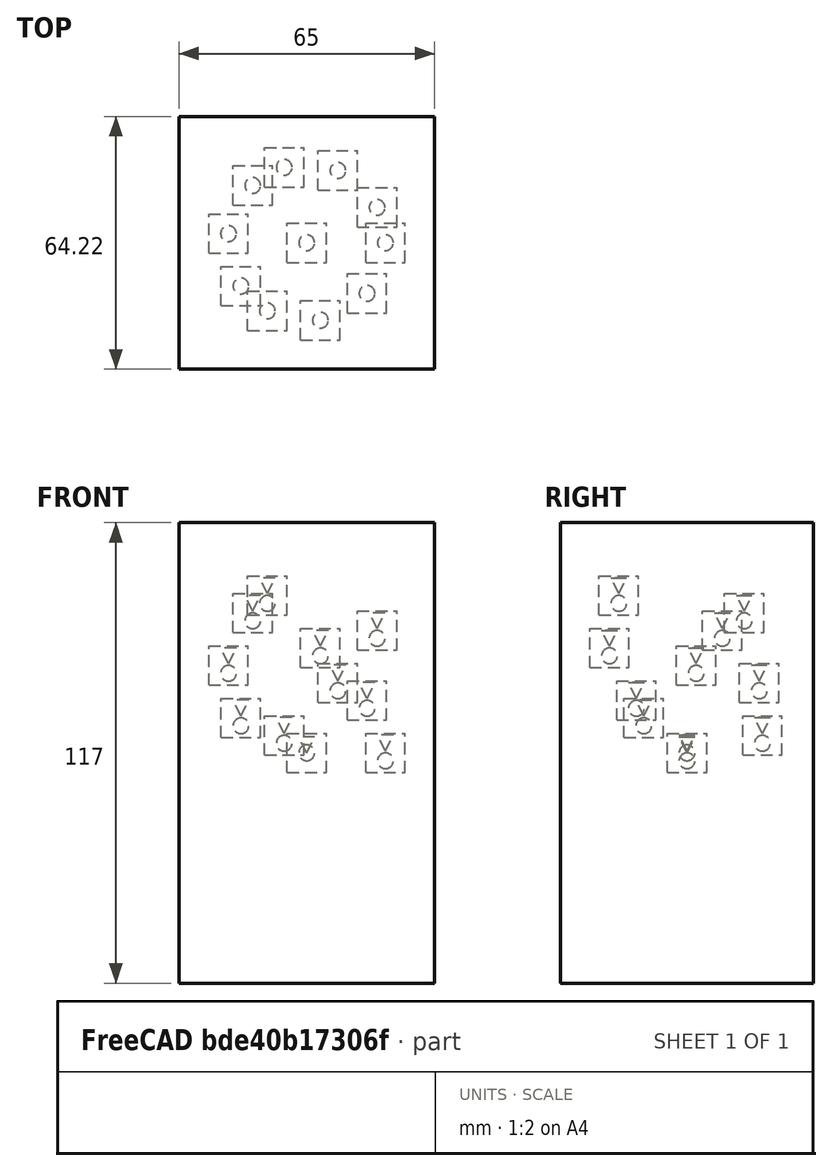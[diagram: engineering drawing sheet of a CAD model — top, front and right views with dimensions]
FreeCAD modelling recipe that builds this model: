
FCSTD DOCUMENT  (FreeCAD 1.0R39109 (Git))
Label: pathArray-of-part
License: All rights reserved
objects: App::DocumentObjectGroupPython×1251, App::Part×5, Part::FeaturePython×4, Part::Helix×1, Part::Cone×1
note: 6 computed .brp shape members not serialized (recipe doc carries the construction recipe); baked Part::Feature solids carry a one-line shape summary decoded from their .brp

FEATURE [App::DocumentObjectGroupPython] HALFPI  # scripted group (container) (typed FeaturePython)
  name = HALFPI
  value = pi/2.
FEATURE [App::DocumentObjectGroupPython] PI  # scripted group (container) (typed FeaturePython)
  name = PI
  value = 1.*pi
FEATURE [App::DocumentObjectGroupPython] TWOPI  # scripted group (container) (typed FeaturePython)
  name = TWOPI
  value = 2.*pi
FEATURE [App::DocumentObjectGroupPython] Constants  # scripted group (container) (typed FeaturePython)
  Group = -> [HALFPI,PI,TWOPI]
FEATURE [App::DocumentObjectGroupPython] Variables  # scripted group (container) (typed FeaturePython)
FEATURE [App::DocumentObjectGroupPython] Quantities  # scripted group (container) (typed FeaturePython)
FEATURE [App::DocumentObjectGroupPython] Isotopes  # scripted group (container) (typed FeaturePython)
FEATURE [App::DocumentObjectGroupPython] Elements  # scripted group (container) (typed FeaturePython)
FEATURE [App::DocumentObjectGroupPython] Matrix  # scripted group (container) (typed FeaturePython)
FEATURE [App::DocumentObjectGroupPython] Surfaces  # scripted group (container) (typed FeaturePython)
FEATURE [App::DocumentObjectGroupPython] Opticals  # scripted group (container) (typed FeaturePython)
  Group = -> [Matrix,Surfaces]
FEATURE [App::DocumentObjectGroupPython] G4Isotopes  # scripted group (container) (typed FeaturePython)
FEATURE [App::DocumentObjectGroupPython] H_element  # scripted group (container) (typed FeaturePython)
  Z = 1
  atom_value = 1.008
  formula = H
  name = H_element
FEATURE [App::DocumentObjectGroupPython] He_element  # scripted group (container) (typed FeaturePython)
  Z = 2
  atom_value = 4.0026
  formula = He
  name = He_element
FEATURE [App::DocumentObjectGroupPython] Li_element  # scripted group (container) (typed FeaturePython)
  Z = 3
  atom_value = 6.94
  formula = Li
  name = Li_element
FEATURE [App::DocumentObjectGroupPython] Be_element  # scripted group (container) (typed FeaturePython)
  Z = 4
  atom_value = 9.01218
  formula = Be
  name = Be_element
FEATURE [App::DocumentObjectGroupPython] B_element  # scripted group (container) (typed FeaturePython)
  Z = 5
  atom_value = 10.81
  formula = B
  name = B_element
FEATURE [App::DocumentObjectGroupPython] C_element  # scripted group (container) (typed FeaturePython)
  Z = 6
  atom_value = 12.011
  formula = C
  name = C_element
FEATURE [App::DocumentObjectGroupPython] N_element  # scripted group (container) (typed FeaturePython)
  Z = 7
  atom_value = 14.007
  formula = N
  name = N_element
FEATURE [App::DocumentObjectGroupPython] O_element  # scripted group (container) (typed FeaturePython)
  Z = 8
  atom_value = 15.999
  formula = O
  name = O_element
FEATURE [App::DocumentObjectGroupPython] F_element  # scripted group (container) (typed FeaturePython)
  Z = 9
  atom_value = 18.9984
  formula = F
  name = F_element
FEATURE [App::DocumentObjectGroupPython] Ne_element  # scripted group (container) (typed FeaturePython)
  Z = 10
  atom_value = 20.1797
  formula = Ne
  name = Ne_element
FEATURE [App::DocumentObjectGroupPython] Na_element  # scripted group (container) (typed FeaturePython)
  Z = 11
  atom_value = 22.9898
  formula = Na
  name = Na_element
FEATURE [App::DocumentObjectGroupPython] Mg_element  # scripted group (container) (typed FeaturePython)
  Z = 12
  atom_value = 24.305
  formula = Mg
  name = Mg_element
FEATURE [App::DocumentObjectGroupPython] Al_element  # scripted group (container) (typed FeaturePython)
  Z = 13
  atom_value = 26.9815
  formula = Al
  name = Al_element
FEATURE [App::DocumentObjectGroupPython] Si_element  # scripted group (container) (typed FeaturePython)
  Z = 14
  atom_value = 28.085
  formula = Si
  name = Si_element
FEATURE [App::DocumentObjectGroupPython] P_element  # scripted group (container) (typed FeaturePython)
  Z = 15
  atom_value = 30.9738
  formula = P
  name = P_element
FEATURE [App::DocumentObjectGroupPython] S_element  # scripted group (container) (typed FeaturePython)
  Z = 16
  atom_value = 32.06
  formula = S
  name = S_element
FEATURE [App::DocumentObjectGroupPython] Cl_element  # scripted group (container) (typed FeaturePython)
  Z = 17
  atom_value = 35.45
  formula = Cl
  name = Cl_element
FEATURE [App::DocumentObjectGroupPython] Ar_element  # scripted group (container) (typed FeaturePython)
  Z = 18
  atom_value = 39.95
  formula = Ar
  name = Ar_element
FEATURE [App::DocumentObjectGroupPython] K_element  # scripted group (container) (typed FeaturePython)
  Z = 19
  atom_value = 39.0983
  formula = K
  name = K_element
FEATURE [App::DocumentObjectGroupPython] Ca_element  # scripted group (container) (typed FeaturePython)
  Z = 20
  atom_value = 40.078
  formula = Ca
  name = Ca_element
FEATURE [App::DocumentObjectGroupPython] Sc_element  # scripted group (container) (typed FeaturePython)
  Z = 21
  atom_value = 44.9559
  formula = Sc
  name = Sc_element
FEATURE [App::DocumentObjectGroupPython] Ti_element  # scripted group (container) (typed FeaturePython)
  Z = 22
  atom_value = 47.867
  formula = Ti
  name = Ti_element
FEATURE [App::DocumentObjectGroupPython] V_element  # scripted group (container) (typed FeaturePython)
  Z = 23
  atom_value = 50.9415
  formula = V
  name = V_element
FEATURE [App::DocumentObjectGroupPython] Cr_element  # scripted group (container) (typed FeaturePython)
  Z = 24
  atom_value = 51.9961
  formula = Cr
  name = Cr_element
FEATURE [App::DocumentObjectGroupPython] Mn_element  # scripted group (container) (typed FeaturePython)
  Z = 25
  atom_value = 54.938
  formula = Mn
  name = Mn_element
FEATURE [App::DocumentObjectGroupPython] Fe_element  # scripted group (container) (typed FeaturePython)
  Z = 26
  atom_value = 55.845
  formula = Fe
  name = Fe_element
FEATURE [App::DocumentObjectGroupPython] Co_element  # scripted group (container) (typed FeaturePython)
  Z = 27
  atom_value = 58.9332
  formula = Co
  name = Co_element
FEATURE [App::DocumentObjectGroupPython] Ni_element  # scripted group (container) (typed FeaturePython)
  Z = 28
  atom_value = 58.6934
  formula = Ni
  name = Ni_element
FEATURE [App::DocumentObjectGroupPython] Cu_element  # scripted group (container) (typed FeaturePython)
  Z = 29
  atom_value = 63.546
  formula = Cu
  name = Cu_element
FEATURE [App::DocumentObjectGroupPython] Zn_element  # scripted group (container) (typed FeaturePython)
  Z = 30
  atom_value = 65.38
  formula = Zn
  name = Zn_element
FEATURE [App::DocumentObjectGroupPython] Ga_element  # scripted group (container) (typed FeaturePython)
  Z = 31
  atom_value = 69.723
  formula = Ga
  name = Ga_element
FEATURE [App::DocumentObjectGroupPython] Ge_element  # scripted group (container) (typed FeaturePython)
  Z = 32
  atom_value = 72.63
  formula = Ge
  name = Ge_element
FEATURE [App::DocumentObjectGroupPython] As_element  # scripted group (container) (typed FeaturePython)
  Z = 33
  atom_value = 74.9216
  formula = As
  name = As_element
FEATURE [App::DocumentObjectGroupPython] Se_element  # scripted group (container) (typed FeaturePython)
  Z = 34
  atom_value = 78.971
  formula = Se
  name = Se_element
FEATURE [App::DocumentObjectGroupPython] Br_element  # scripted group (container) (typed FeaturePython)
  Z = 35
  atom_value = 79.904
  formula = Br
  name = Br_element
FEATURE [App::DocumentObjectGroupPython] Kr_element  # scripted group (container) (typed FeaturePython)
  Z = 36
  atom_value = 83.798
  formula = Kr
  name = Kr_element
FEATURE [App::DocumentObjectGroupPython] Rb_element  # scripted group (container) (typed FeaturePython)
  Z = 37
  atom_value = 85.4678
  formula = Rb
  name = Rb_element
FEATURE [App::DocumentObjectGroupPython] Sr_element  # scripted group (container) (typed FeaturePython)
  Z = 38
  atom_value = 87.62
  formula = Sr
  name = Sr_element
FEATURE [App::DocumentObjectGroupPython] Y_element  # scripted group (container) (typed FeaturePython)
  Z = 39
  atom_value = 88.9058
  formula = Y
  name = Y_element
FEATURE [App::DocumentObjectGroupPython] Zr_element  # scripted group (container) (typed FeaturePython)
  Z = 40
  atom_value = 91.224
  formula = Zr
  name = Zr_element
FEATURE [App::DocumentObjectGroupPython] Nb_element  # scripted group (container) (typed FeaturePython)
  Z = 41
  atom_value = 92.9064
  formula = Nb
  name = Nb_element
FEATURE [App::DocumentObjectGroupPython] Mo_element  # scripted group (container) (typed FeaturePython)
  Z = 42
  atom_value = 95.95
  formula = Mo
  name = Mo_element
FEATURE [App::DocumentObjectGroupPython] Tc_element  # scripted group (container) (typed FeaturePython)
  Z = 43
  atom_value = 97
  formula = Tc
  name = Tc_element
FEATURE [App::DocumentObjectGroupPython] Ru_element  # scripted group (container) (typed FeaturePython)
  Z = 44
  atom_value = 101.07
  formula = Ru
  name = Ru_element
FEATURE [App::DocumentObjectGroupPython] Rh_element  # scripted group (container) (typed FeaturePython)
  Z = 45
  atom_value = 102.905
  formula = Rh
  name = Rh_element
FEATURE [App::DocumentObjectGroupPython] Pd_element  # scripted group (container) (typed FeaturePython)
  Z = 46
  atom_value = 106.42
  formula = Pd
  name = Pd_element
FEATURE [App::DocumentObjectGroupPython] Ag_element  # scripted group (container) (typed FeaturePython)
  Z = 47
  atom_value = 107.868
  formula = Ag
  name = Ag_element
FEATURE [App::DocumentObjectGroupPython] Cd_element  # scripted group (container) (typed FeaturePython)
  Z = 48
  atom_value = 112.414
  formula = Cd
  name = Cd_element
FEATURE [App::DocumentObjectGroupPython] In_element  # scripted group (container) (typed FeaturePython)
  Z = 49
  atom_value = 114.818
  formula = In
  name = In_element
FEATURE [App::DocumentObjectGroupPython] Sn_element  # scripted group (container) (typed FeaturePython)
  Z = 50
  atom_value = 118.71
  formula = Sn
  name = Sn_element
FEATURE [App::DocumentObjectGroupPython] Sb_element  # scripted group (container) (typed FeaturePython)
  Z = 51
  atom_value = 121.76
  formula = Sb
  name = Sb_element
FEATURE [App::DocumentObjectGroupPython] Te_element  # scripted group (container) (typed FeaturePython)
  Z = 52
  atom_value = 127.6
  formula = Te
  name = Te_element
FEATURE [App::DocumentObjectGroupPython] I_element  # scripted group (container) (typed FeaturePython)
  Z = 53
  atom_value = 126.904
  formula = I
  name = I_element
FEATURE [App::DocumentObjectGroupPython] Xe_element  # scripted group (container) (typed FeaturePython)
  Z = 54
  atom_value = 131.293
  formula = Xe
  name = Xe_element
FEATURE [App::DocumentObjectGroupPython] Cs_element  # scripted group (container) (typed FeaturePython)
  Z = 55
  atom_value = 132.905
  formula = Cs
  name = Cs_element
FEATURE [App::DocumentObjectGroupPython] Ba_element  # scripted group (container) (typed FeaturePython)
  Z = 56
  atom_value = 137.327
  formula = Ba
  name = Ba_element
FEATURE [App::DocumentObjectGroupPython] La_element  # scripted group (container) (typed FeaturePython)
  Z = 57
  atom_value = 138.905
  formula = La
  name = La_element
FEATURE [App::DocumentObjectGroupPython] Ce_element  # scripted group (container) (typed FeaturePython)
  Z = 58
  atom_value = 140.116
  formula = Ce
  name = Ce_element
FEATURE [App::DocumentObjectGroupPython] Pr_element  # scripted group (container) (typed FeaturePython)
  Z = 59
  atom_value = 140.908
  formula = Pr
  name = Pr_element
FEATURE [App::DocumentObjectGroupPython] Nd_element  # scripted group (container) (typed FeaturePython)
  Z = 60
  atom_value = 144.242
  formula = Nd
  name = Nd_element
FEATURE [App::DocumentObjectGroupPython] Pm_element  # scripted group (container) (typed FeaturePython)
  Z = 61
  atom_value = 145
  formula = Pm
  name = Pm_element
FEATURE [App::DocumentObjectGroupPython] Sm_element  # scripted group (container) (typed FeaturePython)
  Z = 62
  atom_value = 150.36
  formula = Sm
  name = Sm_element
FEATURE [App::DocumentObjectGroupPython] Eu_element  # scripted group (container) (typed FeaturePython)
  Z = 63
  atom_value = 151.964
  formula = Eu
  name = Eu_element
FEATURE [App::DocumentObjectGroupPython] Gd_element  # scripted group (container) (typed FeaturePython)
  Z = 64
  atom_value = 157.25
  formula = Gd
  name = Gd_element
FEATURE [App::DocumentObjectGroupPython] Tb_element  # scripted group (container) (typed FeaturePython)
  Z = 65
  atom_value = 158.925
  formula = Tb
  name = Tb_element
FEATURE [App::DocumentObjectGroupPython] Dy_element  # scripted group (container) (typed FeaturePython)
  Z = 66
  atom_value = 162.5
  formula = Dy
  name = Dy_element
FEATURE [App::DocumentObjectGroupPython] Ho_element  # scripted group (container) (typed FeaturePython)
  Z = 67
  atom_value = 164.93
  formula = Ho
  name = Ho_element
FEATURE [App::DocumentObjectGroupPython] Er_element  # scripted group (container) (typed FeaturePython)
  Z = 68
  atom_value = 167.259
  formula = Er
  name = Er_element
FEATURE [App::DocumentObjectGroupPython] Tm_element  # scripted group (container) (typed FeaturePython)
  Z = 69
  atom_value = 168.934
  formula = Tm
  name = Tm_element
FEATURE [App::DocumentObjectGroupPython] Yb_element  # scripted group (container) (typed FeaturePython)
  Z = 70
  atom_value = 173.045
  formula = Yb
  name = Yb_element
FEATURE [App::DocumentObjectGroupPython] Lu_element  # scripted group (container) (typed FeaturePython)
  Z = 71
  atom_value = 174.967
  formula = Lu
  name = Lu_element
FEATURE [App::DocumentObjectGroupPython] Hf_element  # scripted group (container) (typed FeaturePython)
  Z = 72
  atom_value = 178.49
  formula = Hf
  name = Hf_element
FEATURE [App::DocumentObjectGroupPython] Ta_element  # scripted group (container) (typed FeaturePython)
  Z = 73
  atom_value = 180.948
  formula = Ta
  name = Ta_element
FEATURE [App::DocumentObjectGroupPython] W_element  # scripted group (container) (typed FeaturePython)
  Z = 74
  atom_value = 183.84
  formula = W
  name = W_element
FEATURE [App::DocumentObjectGroupPython] Re_element  # scripted group (container) (typed FeaturePython)
  Z = 75
  atom_value = 186.207
  formula = Re
  name = Re_element
FEATURE [App::DocumentObjectGroupPython] Os_element  # scripted group (container) (typed FeaturePython)
  Z = 76
  atom_value = 190.23
  formula = Os
  name = Os_element
FEATURE [App::DocumentObjectGroupPython] Ir_element  # scripted group (container) (typed FeaturePython)
  Z = 77
  atom_value = 192.217
  formula = Ir
  name = Ir_element
FEATURE [App::DocumentObjectGroupPython] Pt_element  # scripted group (container) (typed FeaturePython)
  Z = 78
  atom_value = 195.084
  formula = Pt
  name = Pt_element
FEATURE [App::DocumentObjectGroupPython] Au_element  # scripted group (container) (typed FeaturePython)
  Z = 79
  atom_value = 196.967
  formula = Au
  name = Au_element
FEATURE [App::DocumentObjectGroupPython] Hg_element  # scripted group (container) (typed FeaturePython)
  Z = 80
  atom_value = 200.592
  formula = Hg
  name = Hg_element
FEATURE [App::DocumentObjectGroupPython] Tl_element  # scripted group (container) (typed FeaturePython)
  Z = 81
  atom_value = 204.38
  formula = Tl
  name = Tl_element
FEATURE [App::DocumentObjectGroupPython] Pb_element  # scripted group (container) (typed FeaturePython)
  Z = 82
  atom_value = 207.2
  formula = Pb
  name = Pb_element
FEATURE [App::DocumentObjectGroupPython] Bi_element  # scripted group (container) (typed FeaturePython)
  Z = 83
  atom_value = 208.98
  formula = Bi
  name = Bi_element
FEATURE [App::DocumentObjectGroupPython] Po_element  # scripted group (container) (typed FeaturePython)
  Z = 84
  atom_value = 209
  formula = Po
  name = Po_element
FEATURE [App::DocumentObjectGroupPython] At_element  # scripted group (container) (typed FeaturePython)
  Z = 85
  atom_value = 210
  formula = At
  name = At_element
FEATURE [App::DocumentObjectGroupPython] Rn_element  # scripted group (container) (typed FeaturePython)
  Z = 86
  atom_value = 222
  formula = Rn
  name = Rn_element
FEATURE [App::DocumentObjectGroupPython] Fr_element  # scripted group (container) (typed FeaturePython)
  Z = 87
  atom_value = 223
  formula = Fr
  name = Fr_element
FEATURE [App::DocumentObjectGroupPython] Ra_element  # scripted group (container) (typed FeaturePython)
  Z = 88
  atom_value = 226
  formula = Ra
  name = Ra_element
FEATURE [App::DocumentObjectGroupPython] Ac_element  # scripted group (container) (typed FeaturePython)
  Z = 89
  atom_value = 227
  formula = Ac
  name = Ac_element
FEATURE [App::DocumentObjectGroupPython] Th_element  # scripted group (container) (typed FeaturePython)
  Z = 90
  atom_value = 232.038
  formula = Th
  name = Th_element
FEATURE [App::DocumentObjectGroupPython] Pa_element  # scripted group (container) (typed FeaturePython)
  Z = 91
  atom_value = 231.036
  formula = Pa
  name = Pa_element
FEATURE [App::DocumentObjectGroupPython] U_element  # scripted group (container) (typed FeaturePython)
  Z = 92
  atom_value = 238.029
  formula = U
  name = U_element
FEATURE [App::DocumentObjectGroupPython] Np_element  # scripted group (container) (typed FeaturePython)
  Z = 93
  atom_value = 237
  formula = Np
  name = Np_element
FEATURE [App::DocumentObjectGroupPython] Pu_element  # scripted group (container) (typed FeaturePython)
  Z = 94
  atom_value = 244
  formula = Pu
  name = Pu_element
FEATURE [App::DocumentObjectGroupPython] Am_element  # scripted group (container) (typed FeaturePython)
  Z = 95
  atom_value = 243
  formula = Am
  name = Am_element
FEATURE [App::DocumentObjectGroupPython] Cm_element  # scripted group (container) (typed FeaturePython)
  Z = 96
  atom_value = 247
  formula = Cm
  name = Cm_element
FEATURE [App::DocumentObjectGroupPython] Bk_element  # scripted group (container) (typed FeaturePython)
  Z = 97
  atom_value = 247
  formula = Bk
  name = Bk_element
FEATURE [App::DocumentObjectGroupPython] Cf_element  # scripted group (container) (typed FeaturePython)
  Z = 98
  atom_value = 251
  formula = Cf
  name = Cf_element
FEATURE [App::DocumentObjectGroupPython] G4Elements  # scripted group (container) (typed FeaturePython)
  Group = -> [H_element,He_element,Li_element,Be_element,B_element,C_element,N_element,O_element,F_element,Ne_element,Na_element,Mg_element,Al_element,Si_element,P_element,S_element,Cl_element,Ar_element,K_element,Ca_element,Sc_element,Ti_element,V_element,Cr_element,Mn_element,Fe_element,Co_element,Ni_element,Cu_element,Zn_element,Ga_element,Ge_element,As_element,Se_element,Br_element,Kr_element,Rb_element,+61 more]
FEATURE [App::DocumentObjectGroupPython] H_element001  label="H_element : 0.101"  # scripted group (container) (typed FeaturePython)
  n = 0.101327
FEATURE [App::DocumentObjectGroupPython] C_element001  label="C_element : 0.775"  # scripted group (container) (typed FeaturePython)
  n = 0.7755
FEATURE [App::DocumentObjectGroupPython] N_element001  label="N_element : 0.035"  # scripted group (container) (typed FeaturePython)
  n = 0.035057
FEATURE [App::DocumentObjectGroupPython] O_element001  label="O_element : 0.052"  # scripted group (container) (typed FeaturePython)
  n = 0.0523159
FEATURE [App::DocumentObjectGroupPython] F_element001  label="F_element : 0.017"  # scripted group (container) (typed FeaturePython)
  n = 0.017422
FEATURE [App::DocumentObjectGroupPython] Ca_element001  label="Ca_element : 0.018"  # scripted group (container) (typed FeaturePython)
  n = 0.018378
FEATURE [App::DocumentObjectGroupPython] G4_A_150_TISSUE  label="G4_A-150_TISSUE"  # scripted group (container) (typed FeaturePython)
  Dunit = g/cm3
  Dvalue = 1.127
  Group = -> [H_element001,C_element001,N_element001,O_element001,F_element001,Ca_element001]
  conduct = 2
  density = 1
  expand = 3
  formula = G4_A-150_TISSUE
  name = G4_A-150_TISSUE
  specific = 4
FEATURE [App::DocumentObjectGroupPython] C_element002  label="C_element : 3"  # scripted group (container) (typed FeaturePython)
  n = 3
  ref = C_element
FEATURE [App::DocumentObjectGroupPython] H_element002  label="H_element : 6"  # scripted group (container) (typed FeaturePython)
  n = 6
  ref = H_element
FEATURE [App::DocumentObjectGroupPython] O_element002  label="O_element : 1"  # scripted group (container) (typed FeaturePython)
  n = 1
  ref = O_element
FEATURE [App::DocumentObjectGroupPython] G4_ACETONE  # scripted group (container) (typed FeaturePython)
  Dunit = g/cm3
  Dvalue = 0.7899
  Group = -> [C_element002,H_element002,O_element002]
  conduct = 2
  density = 1
  expand = 3
  formula = G4_ACETONE
  name = G4_ACETONE
  specific = 4
FEATURE [App::DocumentObjectGroupPython] C_element003  label="C_element : 2"  # scripted group (container) (typed FeaturePython)
  n = 2
  ref = C_element
FEATURE [App::DocumentObjectGroupPython] H_element003  label="H_element : 2"  # scripted group (container) (typed FeaturePython)
  n = 2
  ref = H_element
FEATURE [App::DocumentObjectGroupPython] G4_ACETYLENE  # scripted group (container) (typed FeaturePython)
  Dunit = g/cm3
  Dvalue = 0.0010967
  Group = -> [C_element003,H_element003]
  conduct = 2
  density = 1
  expand = 3
  formula = G4_ACETYLENE
  name = G4_ACETYLENE
  specific = 4
FEATURE [App::DocumentObjectGroupPython] C_element004  label="C_element : 5"  # scripted group (container) (typed FeaturePython)
  n = 5
  ref = C_element
FEATURE [App::DocumentObjectGroupPython] H_element004  label="H_element : 5"  # scripted group (container) (typed FeaturePython)
  n = 5
  ref = H_element
FEATURE [App::DocumentObjectGroupPython] N_element002  label="N_element : 5"  # scripted group (container) (typed FeaturePython)
  n = 5
  ref = N_element
FEATURE [App::DocumentObjectGroupPython] G4_ADENINE  # scripted group (container) (typed FeaturePython)
  Dunit = g/cm3
  Dvalue = 1.6
  Group = -> [C_element004,H_element004,N_element002]
  conduct = 2
  density = 1
  expand = 3
  formula = G4_ADENINE
  name = G4_ADENINE
  specific = 4
FEATURE [App::DocumentObjectGroupPython] H_element005  label="H_element : 0.114"  # scripted group (container) (typed FeaturePython)
  n = 0.114
FEATURE [App::DocumentObjectGroupPython] C_element005  label="C_element : 0.598"  # scripted group (container) (typed FeaturePython)
  n = 0.598
FEATURE [App::DocumentObjectGroupPython] N_element003  label="N_element : 0.007"  # scripted group (container) (typed FeaturePython)
  n = 0.007
FEATURE [App::DocumentObjectGroupPython] O_element003  label="O_element : 0.278"  # scripted group (container) (typed FeaturePython)
  n = 0.278
FEATURE [App::DocumentObjectGroupPython] Na_element001  label="Na_element : 0.001"  # scripted group (container) (typed FeaturePython)
  n = 0.001
FEATURE [App::DocumentObjectGroupPython] S_element001  label="S_element : 0.001"  # scripted group (container) (typed FeaturePython)
  n = 0.001
FEATURE [App::DocumentObjectGroupPython] Cl_element001  label="Cl_element : 0.001"  # scripted group (container) (typed FeaturePython)
  n = 0.001
FEATURE [App::DocumentObjectGroupPython] G4_ADIPOSE_TISSUE_ICRP  # scripted group (container) (typed FeaturePython)
  Dunit = g/cm3
  Dvalue = 0.95
  Group = -> [H_element005,C_element005,N_element003,O_element003,Na_element001,S_element001,Cl_element001]
  conduct = 2
  density = 1
  expand = 3
  formula = G4_ADIPOSE_TISSUE_ICRP
  name = G4_ADIPOSE_TISSUE_ICRP
  specific = 4
FEATURE [App::DocumentObjectGroupPython] C_element006  label="C_element : 0.000"  # scripted group (container) (typed FeaturePython)
  n = 0.000124
FEATURE [App::DocumentObjectGroupPython] N_element004  label="N_element : 0.755"  # scripted group (container) (typed FeaturePython)
  n = 0.755268
FEATURE [App::DocumentObjectGroupPython] O_element004  label="O_element : 0.232"  # scripted group (container) (typed FeaturePython)
  n = 0.231781
FEATURE [App::DocumentObjectGroupPython] Ar_element001  label="Ar_element : 0.013"  # scripted group (container) (typed FeaturePython)
  n = 0.012827
FEATURE [App::DocumentObjectGroupPython] G4_AIR  # scripted group (container) (typed FeaturePython)
  Dunit = g/cm3
  Dvalue = 0.00120479
  Group = -> [C_element006,N_element004,O_element004,Ar_element001]
  conduct = 2
  density = 1
  expand = 3
  formula = G4_AIR
  name = G4_AIR
  specific = 4
FEATURE [App::DocumentObjectGroupPython] C_element007  label="C_element : 006"  # scripted group (container) (typed FeaturePython)
  n = 3
  ref = C_element
FEATURE [App::DocumentObjectGroupPython] H_element006  label="H_element : 7"  # scripted group (container) (typed FeaturePython)
  n = 7
  ref = H_element
FEATURE [App::DocumentObjectGroupPython] N_element005  label="N_element : 1"  # scripted group (container) (typed FeaturePython)
  n = 1
  ref = N_element
FEATURE [App::DocumentObjectGroupPython] O_element005  label="O_element : 2"  # scripted group (container) (typed FeaturePython)
  n = 2
  ref = O_element
FEATURE [App::DocumentObjectGroupPython] G4_ALANINE  # scripted group (container) (typed FeaturePython)
  Dunit = g/cm3
  Dvalue = 1.42
  Group = -> [C_element007,H_element006,N_element005,O_element005]
  conduct = 2
  density = 1
  expand = 3
  formula = G4_ALANINE
  name = G4_ALANINE
  specific = 4
FEATURE [App::DocumentObjectGroupPython] Al_element001  label="Al_element : 2"  # scripted group (container) (typed FeaturePython)
  n = 2
  ref = Al_element
FEATURE [App::DocumentObjectGroupPython] O_element006  label="O_element : 3"  # scripted group (container) (typed FeaturePython)
  n = 3
  ref = O_element
FEATURE [App::DocumentObjectGroupPython] G4_ALUMINUM_OXIDE  # scripted group (container) (typed FeaturePython)
  Dunit = g/cm3
  Dvalue = 3.97
  Group = -> [Al_element001,O_element006]
  conduct = 2
  density = 1
  expand = 3
  formula = G4_ALUMINUM_OXIDE
  name = G4_ALUMINUM_OXIDE
  specific = 4
FEATURE [App::DocumentObjectGroupPython] H_element007  label="H_element : 0.106"  # scripted group (container) (typed FeaturePython)
  n = 0.10593
FEATURE [App::DocumentObjectGroupPython] C_element008  label="C_element : 0.789"  # scripted group (container) (typed FeaturePython)
  n = 0.788974
FEATURE [App::DocumentObjectGroupPython] O_element007  label="O_element : 0.105"  # scripted group (container) (typed FeaturePython)
  n = 0.105096
FEATURE [App::DocumentObjectGroupPython] G4_AMBER  # scripted group (container) (typed FeaturePython)
  Dunit = g/cm3
  Dvalue = 1.1
  Group = -> [H_element007,C_element008,O_element007]
  conduct = 2
  density = 1
  expand = 3
  formula = G4_AMBER
  name = G4_AMBER
  specific = 4
FEATURE [App::DocumentObjectGroupPython] N_element006  label="N_element : 006"  # scripted group (container) (typed FeaturePython)
  n = 1
  ref = N_element
FEATURE [App::DocumentObjectGroupPython] H_element008  label="H_element : 3"  # scripted group (container) (typed FeaturePython)
  n = 3
  ref = H_element
FEATURE [App::DocumentObjectGroupPython] G4_AMMONIA  # scripted group (container) (typed FeaturePython)
  Dunit = g/cm3
  Dvalue = 0.000826019
  Group = -> [N_element006,H_element008]
  conduct = 2
  density = 1
  expand = 3
  formula = G4_AMMONIA
  name = G4_AMMONIA
  specific = 4
FEATURE [App::DocumentObjectGroupPython] C_element009  label="C_element : 6"  # scripted group (container) (typed FeaturePython)
  n = 6
  ref = C_element
FEATURE [App::DocumentObjectGroupPython] H_element009  label="H_element : 008"  # scripted group (container) (typed FeaturePython)
  n = 7
  ref = H_element
FEATURE [App::DocumentObjectGroupPython] N_element007  label="N_element : 007"  # scripted group (container) (typed FeaturePython)
  n = 1
  ref = N_element
FEATURE [App::DocumentObjectGroupPython] G4_ANILINE  # scripted group (container) (typed FeaturePython)
  Dunit = g/cm3
  Dvalue = 1.0235
  Group = -> [C_element009,H_element009,N_element007]
  conduct = 2
  density = 1
  expand = 3
  formula = G4_ANILINE
  name = G4_ANILINE
  specific = 4
FEATURE [App::DocumentObjectGroupPython] C_element010  label="C_element : 14"  # scripted group (container) (typed FeaturePython)
  n = 14
  ref = C_element
FEATURE [App::DocumentObjectGroupPython] H_element010  label="H_element : 10"  # scripted group (container) (typed FeaturePython)
  n = 10
  ref = H_element
FEATURE [App::DocumentObjectGroupPython] G4_ANTHRACENE  # scripted group (container) (typed FeaturePython)
  Dunit = g/cm3
  Dvalue = 1.283
  Group = -> [C_element010,H_element010]
  conduct = 2
  density = 1
  expand = 3
  formula = G4_ANTHRACENE
  name = G4_ANTHRACENE
  specific = 4
FEATURE [App::DocumentObjectGroupPython] H_element011  label="H_element : 0.065"  # scripted group (container) (typed FeaturePython)
  n = 0.0654709
FEATURE [App::DocumentObjectGroupPython] C_element011  label="C_element : 0.537"  # scripted group (container) (typed FeaturePython)
  n = 0.536944
FEATURE [App::DocumentObjectGroupPython] N_element008  label="N_element : 0.021"  # scripted group (container) (typed FeaturePython)
  n = 0.0215
FEATURE [App::DocumentObjectGroupPython] O_element008  label="O_element : 0.032"  # scripted group (container) (typed FeaturePython)
  n = 0.032085
FEATURE [App::DocumentObjectGroupPython] F_element002  label="F_element : 0.167"  # scripted group (container) (typed FeaturePython)
  n = 0.167411
FEATURE [App::DocumentObjectGroupPython] Ca_element002  label="Ca_element : 0.177"  # scripted group (container) (typed FeaturePython)
  n = 0.176589
FEATURE [App::DocumentObjectGroupPython] G4_B_100_BONE  label="G4_B-100_BONE"  # scripted group (container) (typed FeaturePython)
  Dunit = g/cm3
  Dvalue = 1.45
  Group = -> [H_element011,C_element011,N_element008,O_element008,F_element002,Ca_element002]
  conduct = 2
  density = 1
  expand = 3
  formula = G4_B-100_BONE
  name = G4_B-100_BONE
  specific = 4
FEATURE [App::DocumentObjectGroupPython] H_element012  label="H_element : 0.057"  # scripted group (container) (typed FeaturePython)
  n = 0.057441
FEATURE [App::DocumentObjectGroupPython] C_element012  label="C_element : 0.790"  # scripted group (container) (typed FeaturePython)
  n = 0.774591
FEATURE [App::DocumentObjectGroupPython] O_element009  label="O_element : 0.168"  # scripted group (container) (typed FeaturePython)
  n = 0.167968
FEATURE [App::DocumentObjectGroupPython] G4_BAKELITE  # scripted group (container) (typed FeaturePython)
  Dunit = g/cm3
  Dvalue = 1.25
  Group = -> [H_element012,C_element012,O_element009]
  conduct = 2
  density = 1
  expand = 3
  formula = G4_BAKELITE
  name = G4_BAKELITE
  specific = 4
FEATURE [App::DocumentObjectGroupPython] Ba_element001  label="Ba_element : 1"  # scripted group (container) (typed FeaturePython)
  n = 1
  ref = Ba_element
FEATURE [App::DocumentObjectGroupPython] F_element003  label="F_element : 2"  # scripted group (container) (typed FeaturePython)
  n = 2
  ref = F_element
FEATURE [App::DocumentObjectGroupPython] G4_BARIUM_FLUORIDE  # scripted group (container) (typed FeaturePython)
  Dunit = g/cm3
  Dvalue = 4.89
  Group = -> [Ba_element001,F_element003]
  conduct = 2
  density = 1
  expand = 3
  formula = G4_BARIUM_FLUORIDE
  name = G4_BARIUM_FLUORIDE
  specific = 4
FEATURE [App::DocumentObjectGroupPython] Ba_element002  label="Ba_element : 002"  # scripted group (container) (typed FeaturePython)
  n = 1
  ref = Ba_element
FEATURE [App::DocumentObjectGroupPython] S_element002  label="S_element : 1"  # scripted group (container) (typed FeaturePython)
  n = 1
  ref = S_element
FEATURE [App::DocumentObjectGroupPython] O_element010  label="O_element : 4"  # scripted group (container) (typed FeaturePython)
  n = 4
  ref = O_element
FEATURE [App::DocumentObjectGroupPython] G4_BARIUM_SULFATE  # scripted group (container) (typed FeaturePython)
  Dunit = g/cm3
  Dvalue = 4.5
  Group = -> [Ba_element002,S_element002,O_element010]
  conduct = 2
  density = 1
  expand = 3
  formula = G4_BARIUM_SULFATE
  name = G4_BARIUM_SULFATE
  specific = 4
FEATURE [App::DocumentObjectGroupPython] C_element013  label="C_element : 007"  # scripted group (container) (typed FeaturePython)
  n = 6
  ref = C_element
FEATURE [App::DocumentObjectGroupPython] H_element013  label="H_element : 009"  # scripted group (container) (typed FeaturePython)
  n = 6
  ref = H_element
FEATURE [App::DocumentObjectGroupPython] G4_BENZENE  # scripted group (container) (typed FeaturePython)
  Dunit = g/cm3
  Dvalue = 0.87865
  Group = -> [C_element013,H_element013]
  conduct = 2
  density = 1
  expand = 3
  formula = G4_BENZENE
  name = G4_BENZENE
  specific = 4
FEATURE [App::DocumentObjectGroupPython] Be_element001  label="Be_element : 1"  # scripted group (container) (typed FeaturePython)
  n = 1
  ref = Be_element
FEATURE [App::DocumentObjectGroupPython] O_element011  label="O_element : 005"  # scripted group (container) (typed FeaturePython)
  n = 1
  ref = O_element
FEATURE [App::DocumentObjectGroupPython] G4_BERYLLIUM_OXIDE  # scripted group (container) (typed FeaturePython)
  Dunit = g/cm3
  Dvalue = 3.01
  Group = -> [Be_element001,O_element011]
  conduct = 2
  density = 1
  expand = 3
  formula = G4_BERYLLIUM_OXIDE
  name = G4_BERYLLIUM_OXIDE
  specific = 4
FEATURE [App::DocumentObjectGroupPython] Bi_element001  label="Bi_element : 4"  # scripted group (container) (typed FeaturePython)
  n = 4
  ref = Bi_element
FEATURE [App::DocumentObjectGroupPython] Ge_element001  label="Ge_element : 3"  # scripted group (container) (typed FeaturePython)
  n = 3
  ref = Ge_element
FEATURE [App::DocumentObjectGroupPython] O_element012  label="O_element : 12"  # scripted group (container) (typed FeaturePython)
  n = 12
  ref = O_element
FEATURE [App::DocumentObjectGroupPython] G4_BGO  # scripted group (container) (typed FeaturePython)
  Dunit = g/cm3
  Dvalue = 7.13
  Group = -> [Bi_element001,Ge_element001,O_element012]
  conduct = 2
  density = 1
  expand = 3
  formula = G4_BGO
  name = G4_BGO
  specific = 4
FEATURE [App::DocumentObjectGroupPython] H_element014  label="H_element : 0.102"  # scripted group (container) (typed FeaturePython)
  n = 0.102
FEATURE [App::DocumentObjectGroupPython] C_element014  label="C_element : 0.110"  # scripted group (container) (typed FeaturePython)
  n = 0.11
FEATURE [App::DocumentObjectGroupPython] N_element009  label="N_element : 0.033"  # scripted group (container) (typed FeaturePython)
  n = 0.033
FEATURE [App::DocumentObjectGroupPython] O_element013  label="O_element : 0.745"  # scripted group (container) (typed FeaturePython)
  n = 0.745
FEATURE [App::DocumentObjectGroupPython] Na_element002  label="Na_element : 0.002"  # scripted group (container) (typed FeaturePython)
  n = 0.001
FEATURE [App::DocumentObjectGroupPython] P_element001  label="P_element : 0.001"  # scripted group (container) (typed FeaturePython)
  n = 0.001
FEATURE [App::DocumentObjectGroupPython] S_element003  label="S_element : 0.002"  # scripted group (container) (typed FeaturePython)
  n = 0.002
FEATURE [App::DocumentObjectGroupPython] Cl_element002  label="Cl_element : 0.003"  # scripted group (container) (typed FeaturePython)
  n = 0.003
FEATURE [App::DocumentObjectGroupPython] K_element001  label="K_element : 0.002"  # scripted group (container) (typed FeaturePython)
  n = 0.002
FEATURE [App::DocumentObjectGroupPython] Fe_element001  label="Fe_element : 0.001"  # scripted group (container) (typed FeaturePython)
  n = 0.001
FEATURE [App::DocumentObjectGroupPython] G4_BLOOD_ICRP  # scripted group (container) (typed FeaturePython)
  Dunit = g/cm3
  Dvalue = 1.06
  Group = -> [H_element014,C_element014,N_element009,O_element013,Na_element002,P_element001,S_element003,Cl_element002,K_element001,Fe_element001]
  conduct = 2
  density = 1
  expand = 3
  formula = G4_BLOOD_ICRP
  name = G4_BLOOD_ICRP
  specific = 4
FEATURE [App::DocumentObjectGroupPython] H_element015  label="H_element : 0.064"  # scripted group (container) (typed FeaturePython)
  n = 0.064
FEATURE [App::DocumentObjectGroupPython] C_element015  label="C_element : 0.278"  # scripted group (container) (typed FeaturePython)
  n = 0.278
FEATURE [App::DocumentObjectGroupPython] N_element010  label="N_element : 0.027"  # scripted group (container) (typed FeaturePython)
  n = 0.027
FEATURE [App::DocumentObjectGroupPython] O_element014  label="O_element : 0.410"  # scripted group (container) (typed FeaturePython)
  n = 0.41
FEATURE [App::DocumentObjectGroupPython] Mg_element001  label="Mg_element : 0.002"  # scripted group (container) (typed FeaturePython)
  n = 0.002
FEATURE [App::DocumentObjectGroupPython] P_element002  label="P_element : 0.070"  # scripted group (container) (typed FeaturePython)
  n = 0.07
FEATURE [App::DocumentObjectGroupPython] S_element004  label="S_element : 0.003"  # scripted group (container) (typed FeaturePython)
  n = 0.002
FEATURE [App::DocumentObjectGroupPython] Ca_element003  label="Ca_element : 0.147"  # scripted group (container) (typed FeaturePython)
  n = 0.147
FEATURE [App::DocumentObjectGroupPython] G4_BONE_COMPACT_ICRU  # scripted group (container) (typed FeaturePython)
  Dunit = g/cm3
  Dvalue = 1.85
  Group = -> [H_element015,C_element015,N_element010,O_element014,Mg_element001,P_element002,S_element004,Ca_element003]
  conduct = 2
  density = 1
  expand = 3
  formula = G4_BONE_COMPACT_ICRU
  name = G4_BONE_COMPACT_ICRU
  specific = 4
FEATURE [App::DocumentObjectGroupPython] H_element016  label="H_element : 0.034"  # scripted group (container) (typed FeaturePython)
  n = 0.034
FEATURE [App::DocumentObjectGroupPython] C_element016  label="C_element : 0.155"  # scripted group (container) (typed FeaturePython)
  n = 0.155
FEATURE [App::DocumentObjectGroupPython] N_element011  label="N_element : 0.042"  # scripted group (container) (typed FeaturePython)
  n = 0.042
FEATURE [App::DocumentObjectGroupPython] O_element015  label="O_element : 0.435"  # scripted group (container) (typed FeaturePython)
  n = 0.435
FEATURE [App::DocumentObjectGroupPython] Na_element003  label="Na_element : 0.003"  # scripted group (container) (typed FeaturePython)
  n = 0.001
FEATURE [App::DocumentObjectGroupPython] Mg_element002  label="Mg_element : 0.003"  # scripted group (container) (typed FeaturePython)
  n = 0.002
FEATURE [App::DocumentObjectGroupPython] P_element003  label="P_element : 0.103"  # scripted group (container) (typed FeaturePython)
  n = 0.103
FEATURE [App::DocumentObjectGroupPython] S_element005  label="S_element : 0.004"  # scripted group (container) (typed FeaturePython)
  n = 0.003
FEATURE [App::DocumentObjectGroupPython] Ca_element004  label="Ca_element : 0.225"  # scripted group (container) (typed FeaturePython)
  n = 0.225
FEATURE [App::DocumentObjectGroupPython] G4_BONE_CORTICAL_ICRP  # scripted group (container) (typed FeaturePython)
  Dunit = g/cm3
  Dvalue = 1.92
  Group = -> [H_element016,C_element016,N_element011,O_element015,Na_element003,Mg_element002,P_element003,S_element005,Ca_element004]
  conduct = 2
  density = 1
  expand = 3
  formula = G4_BONE_CORTICAL_ICRP
  name = G4_BONE_CORTICAL_ICRP
  specific = 4
FEATURE [App::DocumentObjectGroupPython] B_element001  label="B_element : 4"  # scripted group (container) (typed FeaturePython)
  n = 4
  ref = B_element
FEATURE [App::DocumentObjectGroupPython] C_element017  label="C_element : 1"  # scripted group (container) (typed FeaturePython)
  n = 1
  ref = C_element
FEATURE [App::DocumentObjectGroupPython] G4_BORON_CARBIDE  # scripted group (container) (typed FeaturePython)
  Dunit = g/cm3
  Dvalue = 2.52
  Group = -> [B_element001,C_element017]
  conduct = 2
  density = 1
  expand = 3
  formula = G4_BORON_CARBIDE
  name = G4_BORON_CARBIDE
  specific = 4
FEATURE [App::DocumentObjectGroupPython] B_element002  label="B_element : 2"  # scripted group (container) (typed FeaturePython)
  n = 2
  ref = B_element
FEATURE [App::DocumentObjectGroupPython] O_element016  label="O_element : 006"  # scripted group (container) (typed FeaturePython)
  n = 3
  ref = O_element
FEATURE [App::DocumentObjectGroupPython] G4_BORON_OXIDE  # scripted group (container) (typed FeaturePython)
  Dunit = g/cm3
  Dvalue = 1.812
  Group = -> [B_element002,O_element016]
  conduct = 2
  density = 1
  expand = 3
  formula = G4_BORON_OXIDE
  name = G4_BORON_OXIDE
  specific = 4
FEATURE [App::DocumentObjectGroupPython] H_element017  label="H_element : 0.107"  # scripted group (container) (typed FeaturePython)
  n = 0.107
FEATURE [App::DocumentObjectGroupPython] C_element018  label="C_element : 0.145"  # scripted group (container) (typed FeaturePython)
  n = 0.145
FEATURE [App::DocumentObjectGroupPython] N_element012  label="N_element : 0.022"  # scripted group (container) (typed FeaturePython)
  n = 0.022
FEATURE [App::DocumentObjectGroupPython] O_element017  label="O_element : 0.712"  # scripted group (container) (typed FeaturePython)
  n = 0.712
FEATURE [App::DocumentObjectGroupPython] Na_element004  label="Na_element : 0.004"  # scripted group (container) (typed FeaturePython)
  n = 0.002
FEATURE [App::DocumentObjectGroupPython] P_element004  label="P_element : 0.004"  # scripted group (container) (typed FeaturePython)
  n = 0.004
FEATURE [App::DocumentObjectGroupPython] S_element006  label="S_element : 0.005"  # scripted group (container) (typed FeaturePython)
  n = 0.002
FEATURE [App::DocumentObjectGroupPython] Cl_element003  label="Cl_element : 0.004"  # scripted group (container) (typed FeaturePython)
  n = 0.003
FEATURE [App::DocumentObjectGroupPython] K_element002  label="K_element : 0.003"  # scripted group (container) (typed FeaturePython)
  n = 0.003
FEATURE [App::DocumentObjectGroupPython] G4_BRAIN_ICRP  # scripted group (container) (typed FeaturePython)
  Dunit = g/cm3
  Dvalue = 1.04
  Group = -> [H_element017,C_element018,N_element012,O_element017,Na_element004,P_element004,S_element006,Cl_element003,K_element002]
  conduct = 2
  density = 1
  expand = 3
  formula = G4_BRAIN_ICRP
  name = G4_BRAIN_ICRP
  specific = 4
FEATURE [App::DocumentObjectGroupPython] C_element019  label="C_element : 4"  # scripted group (container) (typed FeaturePython)
  n = 4
  ref = C_element
FEATURE [App::DocumentObjectGroupPython] H_element018  label="H_element : 010"  # scripted group (container) (typed FeaturePython)
  n = 10
  ref = H_element
FEATURE [App::DocumentObjectGroupPython] G4_BUTANE  # scripted group (container) (typed FeaturePython)
  Dunit = g/cm3
  Dvalue = 0.00249343
  Group = -> [C_element019,H_element018]
  conduct = 2
  density = 1
  expand = 3
  formula = G4_BUTANE
  name = G4_BUTANE
  specific = 4
FEATURE [App::DocumentObjectGroupPython] C_element020  label="C_element : 008"  # scripted group (container) (typed FeaturePython)
  n = 4
  ref = C_element
FEATURE [App::DocumentObjectGroupPython] H_element019  label="H_element : 011"  # scripted group (container) (typed FeaturePython)
  n = 10
  ref = H_element
FEATURE [App::DocumentObjectGroupPython] O_element018  label="O_element : 007"  # scripted group (container) (typed FeaturePython)
  n = 1
  ref = O_element
FEATURE [App::DocumentObjectGroupPython] G4_N_BUTYL_ALCOHOL  label="G4_N-BUTYL_ALCOHOL"  # scripted group (container) (typed FeaturePython)
  Dunit = g/cm3
  Dvalue = 0.8098
  Group = -> [C_element020,H_element019,O_element018]
  conduct = 2
  density = 1
  expand = 3
  formula = G4_N-BUTYL_ALCOHOL
  name = G4_N-BUTYL_ALCOHOL
  specific = 4
FEATURE [App::DocumentObjectGroupPython] H_element020  label="H_element : 0.025"  # scripted group (container) (typed FeaturePython)
  n = 0.02468
FEATURE [App::DocumentObjectGroupPython] C_element021  label="C_element : 0.502"  # scripted group (container) (typed FeaturePython)
  n = 0.501611
FEATURE [App::DocumentObjectGroupPython] O_element019  label="O_element : 0.005"  # scripted group (container) (typed FeaturePython)
  n = 0.004527
FEATURE [App::DocumentObjectGroupPython] F_element004  label="F_element : 0.465"  # scripted group (container) (typed FeaturePython)
  n = 0.465209
FEATURE [App::DocumentObjectGroupPython] Si_element001  label="Si_element : 0.004"  # scripted group (container) (typed FeaturePython)
  n = 0.003973
FEATURE [App::DocumentObjectGroupPython] G4_C_552  label="G4_C-552"  # scripted group (container) (typed FeaturePython)
  Dunit = g/cm3
  Dvalue = 1.76
  Group = -> [H_element020,C_element021,O_element019,F_element004,Si_element001]
  conduct = 2
  density = 1
  expand = 3
  formula = G4_C-552
  name = G4_C-552
  specific = 4
FEATURE [App::DocumentObjectGroupPython] Cd_element001  label="Cd_element : 1"  # scripted group (container) (typed FeaturePython)
  n = 1
  ref = Cd_element
FEATURE [App::DocumentObjectGroupPython] Te_element001  label="Te_element : 1"  # scripted group (container) (typed FeaturePython)
  n = 1
  ref = Te_element
FEATURE [App::DocumentObjectGroupPython] G4_CADMIUM_TELLURIDE  # scripted group (container) (typed FeaturePython)
  Dunit = g/cm3
  Dvalue = 6.2
  Group = -> [Cd_element001,Te_element001]
  conduct = 2
  density = 1
  expand = 3
  formula = G4_CADMIUM_TELLURIDE
  name = G4_CADMIUM_TELLURIDE
  specific = 4
FEATURE [App::DocumentObjectGroupPython] Cd_element002  label="Cd_element : 002"  # scripted group (container) (typed FeaturePython)
  n = 1
  ref = Cd_element
FEATURE [App::DocumentObjectGroupPython] W_element001  label="W_element : 1"  # scripted group (container) (typed FeaturePython)
  n = 1
  ref = W_element
FEATURE [App::DocumentObjectGroupPython] O_element020  label="O_element : 008"  # scripted group (container) (typed FeaturePython)
  n = 4
  ref = O_element
FEATURE [App::DocumentObjectGroupPython] G4_CADMIUM_TUNGSTATE  # scripted group (container) (typed FeaturePython)
  Dunit = g/cm3
  Dvalue = 7.9
  Group = -> [Cd_element002,W_element001,O_element020]
  conduct = 2
  density = 1
  expand = 3
  formula = G4_CADMIUM_TUNGSTATE
  name = G4_CADMIUM_TUNGSTATE
  specific = 4
FEATURE [App::DocumentObjectGroupPython] Ca_element005  label="Ca_element : 1"  # scripted group (container) (typed FeaturePython)
  n = 1
  ref = Ca_element
FEATURE [App::DocumentObjectGroupPython] C_element022  label="C_element : 009"  # scripted group (container) (typed FeaturePython)
  n = 1
  ref = C_element
FEATURE [App::DocumentObjectGroupPython] O_element021  label="O_element : 009"  # scripted group (container) (typed FeaturePython)
  n = 3
  ref = O_element
FEATURE [App::DocumentObjectGroupPython] G4_CALCIUM_CARBONATE  # scripted group (container) (typed FeaturePython)
  Dunit = g/cm3
  Dvalue = 2.8
  Group = -> [Ca_element005,C_element022,O_element021]
  conduct = 2
  density = 1
  expand = 3
  formula = G4_CALCIUM_CARBONATE
  name = G4_CALCIUM_CARBONATE
  specific = 4
FEATURE [App::DocumentObjectGroupPython] Ca_element006  label="Ca_element : 002"  # scripted group (container) (typed FeaturePython)
  n = 1
  ref = Ca_element
FEATURE [App::DocumentObjectGroupPython] F_element005  label="F_element : 003"  # scripted group (container) (typed FeaturePython)
  n = 2
  ref = F_element
FEATURE [App::DocumentObjectGroupPython] G4_CALCIUM_FLUORIDE  # scripted group (container) (typed FeaturePython)
  Dunit = g/cm3
  Dvalue = 3.18
  Group = -> [Ca_element006,F_element005]
  conduct = 2
  density = 1
  expand = 3
  formula = G4_CALCIUM_FLUORIDE
  name = G4_CALCIUM_FLUORIDE
  specific = 4
FEATURE [App::DocumentObjectGroupPython] Ca_element007  label="Ca_element : 003"  # scripted group (container) (typed FeaturePython)
  n = 1
  ref = Ca_element
FEATURE [App::DocumentObjectGroupPython] O_element022  label="O_element : 010"  # scripted group (container) (typed FeaturePython)
  n = 1
  ref = O_element
FEATURE [App::DocumentObjectGroupPython] G4_CALCIUM_OXIDE  # scripted group (container) (typed FeaturePython)
  Dunit = g/cm3
  Dvalue = 3.3
  Group = -> [Ca_element007,O_element022]
  conduct = 2
  density = 1
  expand = 3
  formula = G4_CALCIUM_OXIDE
  name = G4_CALCIUM_OXIDE
  specific = 4
FEATURE [App::DocumentObjectGroupPython] Ca_element008  label="Ca_element : 004"  # scripted group (container) (typed FeaturePython)
  n = 1
  ref = Ca_element
FEATURE [App::DocumentObjectGroupPython] S_element007  label="S_element : 002"  # scripted group (container) (typed FeaturePython)
  n = 1
  ref = S_element
FEATURE [App::DocumentObjectGroupPython] O_element023  label="O_element : 011"  # scripted group (container) (typed FeaturePython)
  n = 4
  ref = O_element
FEATURE [App::DocumentObjectGroupPython] G4_CALCIUM_SULFATE  # scripted group (container) (typed FeaturePython)
  Dunit = g/cm3
  Dvalue = 2.96
  Group = -> [Ca_element008,S_element007,O_element023]
  conduct = 2
  density = 1
  expand = 3
  formula = G4_CALCIUM_SULFATE
  name = G4_CALCIUM_SULFATE
  specific = 4
FEATURE [App::DocumentObjectGroupPython] Ca_element009  label="Ca_element : 005"  # scripted group (container) (typed FeaturePython)
  n = 1
  ref = Ca_element
FEATURE [App::DocumentObjectGroupPython] W_element002  label="W_element : 002"  # scripted group (container) (typed FeaturePython)
  n = 1
  ref = W_element
FEATURE [App::DocumentObjectGroupPython] O_element024  label="O_element : 012"  # scripted group (container) (typed FeaturePython)
  n = 4
  ref = O_element
FEATURE [App::DocumentObjectGroupPython] G4_CALCIUM_TUNGSTATE  # scripted group (container) (typed FeaturePython)
  Dunit = g/cm3
  Dvalue = 6.062
  Group = -> [Ca_element009,W_element002,O_element024]
  conduct = 2
  density = 1
  expand = 3
  formula = G4_CALCIUM_TUNGSTATE
  name = G4_CALCIUM_TUNGSTATE
  specific = 4
FEATURE [App::DocumentObjectGroupPython] C_element023  label="C_element : 010"  # scripted group (container) (typed FeaturePython)
  n = 1
  ref = C_element
FEATURE [App::DocumentObjectGroupPython] O_element025  label="O_element : 013"  # scripted group (container) (typed FeaturePython)
  n = 2
  ref = O_element
FEATURE [App::DocumentObjectGroupPython] G4_CARBON_DIOXIDE  # scripted group (container) (typed FeaturePython)
  Dunit = g/cm3
  Dvalue = 0.00184212
  Group = -> [C_element023,O_element025]
  conduct = 2
  density = 1
  expand = 3
  formula = G4_CARBON_DIOXIDE
  name = G4_CARBON_DIOXIDE
  specific = 4
FEATURE [App::DocumentObjectGroupPython] C_element024  label="C_element : 011"  # scripted group (container) (typed FeaturePython)
  n = 1
  ref = C_element
FEATURE [App::DocumentObjectGroupPython] Cl_element004  label="Cl_element : 4"  # scripted group (container) (typed FeaturePython)
  n = 4
  ref = Cl_element
FEATURE [App::DocumentObjectGroupPython] G4_CARBON_TETRACHLORIDE  # scripted group (container) (typed FeaturePython)
  Dunit = g/cm3
  Dvalue = 1.594
  Group = -> [C_element024,Cl_element004]
  conduct = 2
  density = 1
  expand = 3
  formula = G4_CARBON_TETRACHLORIDE
  name = G4_CARBON_TETRACHLORIDE
  specific = 4
FEATURE [App::DocumentObjectGroupPython] C_element025  label="C_element : 012"  # scripted group (container) (typed FeaturePython)
  n = 6
  ref = C_element
FEATURE [App::DocumentObjectGroupPython] H_element021  label="H_element : 012"  # scripted group (container) (typed FeaturePython)
  n = 10
  ref = H_element
FEATURE [App::DocumentObjectGroupPython] O_element026  label="O_element : 5"  # scripted group (container) (typed FeaturePython)
  n = 5
  ref = O_element
FEATURE [App::DocumentObjectGroupPython] G4_CELLULOSE_CELLOPHANE  # scripted group (container) (typed FeaturePython)
  Dunit = g/cm3
  Dvalue = 1.42
  Group = -> [C_element025,H_element021,O_element026]
  conduct = 2
  density = 1
  expand = 3
  formula = G4_CELLULOSE_CELLOPHANE
  name = G4_CELLULOSE_CELLOPHANE
  specific = 4
FEATURE [App::DocumentObjectGroupPython] H_element022  label="H_element : 0.067"  # scripted group (container) (typed FeaturePython)
  n = 0.067125
FEATURE [App::DocumentObjectGroupPython] C_element026  label="C_element : 0.545"  # scripted group (container) (typed FeaturePython)
  n = 0.545403
FEATURE [App::DocumentObjectGroupPython] O_element027  label="O_element : 0.387"  # scripted group (container) (typed FeaturePython)
  n = 0.387472
FEATURE [App::DocumentObjectGroupPython] G4_CELLULOSE_BUTYRATE  # scripted group (container) (typed FeaturePython)
  Dunit = g/cm3
  Dvalue = 1.2
  Group = -> [H_element022,C_element026,O_element027]
  conduct = 2
  density = 1
  expand = 3
  formula = G4_CELLULOSE_BUTYRATE
  name = G4_CELLULOSE_BUTYRATE
  specific = 4
FEATURE [App::DocumentObjectGroupPython] H_element023  label="H_element : 0.029"  # scripted group (container) (typed FeaturePython)
  n = 0.029216
FEATURE [App::DocumentObjectGroupPython] C_element027  label="C_element : 0.271"  # scripted group (container) (typed FeaturePython)
  n = 0.271296
FEATURE [App::DocumentObjectGroupPython] N_element013  label="N_element : 0.121"  # scripted group (container) (typed FeaturePython)
  n = 0.121276
FEATURE [App::DocumentObjectGroupPython] O_element028  label="O_element : 0.578"  # scripted group (container) (typed FeaturePython)
  n = 0.578212
FEATURE [App::DocumentObjectGroupPython] G4_CELLULOSE_NITRATE  # scripted group (container) (typed FeaturePython)
  Dunit = g/cm3
  Dvalue = 1.49
  Group = -> [H_element023,C_element027,N_element013,O_element028]
  conduct = 2
  density = 1
  expand = 3
  formula = G4_CELLULOSE_NITRATE
  name = G4_CELLULOSE_NITRATE
  specific = 4
FEATURE [App::DocumentObjectGroupPython] H_element024  label="H_element : 0.108"  # scripted group (container) (typed FeaturePython)
  n = 0.107596
FEATURE [App::DocumentObjectGroupPython] N_element014  label="N_element : 0.001"  # scripted group (container) (typed FeaturePython)
  n = 0.0008
FEATURE [App::DocumentObjectGroupPython] O_element029  label="O_element : 0.875"  # scripted group (container) (typed FeaturePython)
  n = 0.874976
FEATURE [App::DocumentObjectGroupPython] S_element008  label="S_element : 0.015"  # scripted group (container) (typed FeaturePython)
  n = 0.014627
FEATURE [App::DocumentObjectGroupPython] Ce_element001  label="Ce_element : 0.002"  # scripted group (container) (typed FeaturePython)
  n = 0.002001
FEATURE [App::DocumentObjectGroupPython] G4_CERIC_SULFATE  # scripted group (container) (typed FeaturePython)
  Dunit = g/cm3
  Dvalue = 1.03
  Group = -> [H_element024,N_element014,O_element029,S_element008,Ce_element001]
  conduct = 2
  density = 1
  expand = 3
  formula = G4_CERIC_SULFATE
  name = G4_CERIC_SULFATE
  specific = 4
FEATURE [App::DocumentObjectGroupPython] Cs_element001  label="Cs_element : 1"  # scripted group (container) (typed FeaturePython)
  n = 1
  ref = Cs_element
FEATURE [App::DocumentObjectGroupPython] F_element006  label="F_element : 1"  # scripted group (container) (typed FeaturePython)
  n = 1
  ref = F_element
FEATURE [App::DocumentObjectGroupPython] G4_CESIUM_FLUORIDE  # scripted group (container) (typed FeaturePython)
  Dunit = g/cm3
  Dvalue = 4.115
  Group = -> [Cs_element001,F_element006]
  conduct = 2
  density = 1
  expand = 3
  formula = G4_CESIUM_FLUORIDE
  name = G4_CESIUM_FLUORIDE
  specific = 4
FEATURE [App::DocumentObjectGroupPython] Cs_element002  label="Cs_element : 002"  # scripted group (container) (typed FeaturePython)
  n = 1
  ref = Cs_element
FEATURE [App::DocumentObjectGroupPython] I_element001  label="I_element : 1"  # scripted group (container) (typed FeaturePython)
  n = 1
  ref = I_element
FEATURE [App::DocumentObjectGroupPython] G4_CESIUM_IODIDE  # scripted group (container) (typed FeaturePython)
  Dunit = g/cm3
  Dvalue = 4.51
  Group = -> [Cs_element002,I_element001]
  conduct = 2
  density = 1
  expand = 3
  formula = G4_CESIUM_IODIDE
  name = G4_CESIUM_IODIDE
  specific = 4
FEATURE [App::DocumentObjectGroupPython] C_element028  label="C_element : 013"  # scripted group (container) (typed FeaturePython)
  n = 6
  ref = C_element
FEATURE [App::DocumentObjectGroupPython] H_element025  label="H_element : 013"  # scripted group (container) (typed FeaturePython)
  n = 5
  ref = H_element
FEATURE [App::DocumentObjectGroupPython] Cl_element005  label="Cl_element : 1"  # scripted group (container) (typed FeaturePython)
  n = 1
  ref = Cl_element
FEATURE [App::DocumentObjectGroupPython] G4_CHLOROBENZENE  # scripted group (container) (typed FeaturePython)
  Dunit = g/cm3
  Dvalue = 1.1058
  Group = -> [C_element028,H_element025,Cl_element005]
  conduct = 2
  density = 1
  expand = 3
  formula = G4_CHLOROBENZENE
  name = G4_CHLOROBENZENE
  specific = 4
FEATURE [App::DocumentObjectGroupPython] C_element029  label="C_element : 014"  # scripted group (container) (typed FeaturePython)
  n = 1
  ref = C_element
FEATURE [App::DocumentObjectGroupPython] H_element026  label="H_element : 1"  # scripted group (container) (typed FeaturePython)
  n = 1
  ref = H_element
FEATURE [App::DocumentObjectGroupPython] Cl_element006  label="Cl_element : 3"  # scripted group (container) (typed FeaturePython)
  n = 3
  ref = Cl_element
FEATURE [App::DocumentObjectGroupPython] G4_CHLOROFORM  # scripted group (container) (typed FeaturePython)
  Dunit = g/cm3
  Dvalue = 1.4832
  Group = -> [C_element029,H_element026,Cl_element006]
  conduct = 2
  density = 1
  expand = 3
  formula = G4_CHLOROFORM
  name = G4_CHLOROFORM
  specific = 4
FEATURE [App::DocumentObjectGroupPython] H_element027  label="H_element : 0.010"  # scripted group (container) (typed FeaturePython)
  n = 0.01
FEATURE [App::DocumentObjectGroupPython] C_element030  label="C_element : 0.001"  # scripted group (container) (typed FeaturePython)
  n = 0.001
FEATURE [App::DocumentObjectGroupPython] O_element030  label="O_element : 0.529"  # scripted group (container) (typed FeaturePython)
  n = 0.529107
FEATURE [App::DocumentObjectGroupPython] Na_element005  label="Na_element : 0.016"  # scripted group (container) (typed FeaturePython)
  n = 0.016
FEATURE [App::DocumentObjectGroupPython] Mg_element003  label="Mg_element : 0.004"  # scripted group (container) (typed FeaturePython)
  n = 0.002
FEATURE [App::DocumentObjectGroupPython] Al_element002  label="Al_element : 0.034"  # scripted group (container) (typed FeaturePython)
  n = 0.033872
FEATURE [App::DocumentObjectGroupPython] Si_element002  label="Si_element : 0.337"  # scripted group (container) (typed FeaturePython)
  n = 0.337021
FEATURE [App::DocumentObjectGroupPython] K_element003  label="K_element : 0.013"  # scripted group (container) (typed FeaturePython)
  n = 0.013
FEATURE [App::DocumentObjectGroupPython] Ca_element010  label="Ca_element : 0.044"  # scripted group (container) (typed FeaturePython)
  n = 0.044
FEATURE [App::DocumentObjectGroupPython] Fe_element002  label="Fe_element : 0.014"  # scripted group (container) (typed FeaturePython)
  n = 0.014
FEATURE [App::DocumentObjectGroupPython] G4_CONCRETE  # scripted group (container) (typed FeaturePython)
  Dunit = g/cm3
  Dvalue = 2.3
  Group = -> [H_element027,C_element030,O_element030,Na_element005,Mg_element003,Al_element002,Si_element002,K_element003,Ca_element010,Fe_element002]
  conduct = 2
  density = 1
  expand = 3
  formula = G4_CONCRETE
  name = G4_CONCRETE
  specific = 4
FEATURE [App::DocumentObjectGroupPython] C_element031  label="C_element : 015"  # scripted group (container) (typed FeaturePython)
  n = 6
  ref = C_element
FEATURE [App::DocumentObjectGroupPython] H_element028  label="H_element : 12"  # scripted group (container) (typed FeaturePython)
  n = 12
  ref = H_element
FEATURE [App::DocumentObjectGroupPython] G4_CYCLOHEXANE  # scripted group (container) (typed FeaturePython)
  Dunit = g/cm3
  Dvalue = 0.779
  Group = -> [C_element031,H_element028]
  conduct = 2
  density = 1
  expand = 3
  formula = G4_CYCLOHEXANE
  name = G4_CYCLOHEXANE
  specific = 4
FEATURE [App::DocumentObjectGroupPython] C_element032  label="C_element : 016"  # scripted group (container) (typed FeaturePython)
  n = 6
  ref = C_element
FEATURE [App::DocumentObjectGroupPython] H_element029  label="H_element : 4"  # scripted group (container) (typed FeaturePython)
  n = 4
  ref = H_element
FEATURE [App::DocumentObjectGroupPython] Cl_element007  label="Cl_element : 2"  # scripted group (container) (typed FeaturePython)
  n = 2
  ref = Cl_element
FEATURE [App::DocumentObjectGroupPython] G4_1_2_DICHLOROBENZENE  label="G4_1.2-DICHLOROBENZENE"  # scripted group (container) (typed FeaturePython)
  Dunit = g/cm3
  Dvalue = 1.3048
  Group = -> [C_element032,H_element029,Cl_element007]
  conduct = 2
  density = 1
  expand = 3
  formula = G4_1.2-DICHLOROBENZENE
  name = G4_1.2-DICHLOROBENZENE
  specific = 4
FEATURE [App::DocumentObjectGroupPython] C_element033  label="C_element : 017"  # scripted group (container) (typed FeaturePython)
  n = 4
  ref = C_element
FEATURE [App::DocumentObjectGroupPython] H_element030  label="H_element : 8"  # scripted group (container) (typed FeaturePython)
  n = 8
  ref = H_element
FEATURE [App::DocumentObjectGroupPython] O_element031  label="O_element : 014"  # scripted group (container) (typed FeaturePython)
  n = 1
  ref = O_element
FEATURE [App::DocumentObjectGroupPython] Cl_element008  label="Cl_element : 005"  # scripted group (container) (typed FeaturePython)
  n = 2
  ref = Cl_element
FEATURE [App::DocumentObjectGroupPython] G4_DICHLORODIETHYL_ETHER  # scripted group (container) (typed FeaturePython)
  Dunit = g/cm3
  Dvalue = 1.2199
  Group = -> [C_element033,H_element030,O_element031,Cl_element008]
  conduct = 2
  density = 1
  expand = 3
  formula = G4_DICHLORODIETHYL_ETHER
  name = G4_DICHLORODIETHYL_ETHER
  specific = 4
FEATURE [App::DocumentObjectGroupPython] C_element034  label="C_element : 018"  # scripted group (container) (typed FeaturePython)
  n = 2
  ref = C_element
FEATURE [App::DocumentObjectGroupPython] H_element031  label="H_element : 014"  # scripted group (container) (typed FeaturePython)
  n = 4
  ref = H_element
FEATURE [App::DocumentObjectGroupPython] Cl_element009  label="Cl_element : 006"  # scripted group (container) (typed FeaturePython)
  n = 2
  ref = Cl_element
FEATURE [App::DocumentObjectGroupPython] G4_1_2_DICHLOROETHANE  label="G4_1.2-DICHLOROETHANE"  # scripted group (container) (typed FeaturePython)
  Dunit = g/cm3
  Dvalue = 1.2351
  Group = -> [C_element034,H_element031,Cl_element009]
  conduct = 2
  density = 1
  expand = 3
  formula = G4_1.2-DICHLOROETHANE
  name = G4_1.2-DICHLOROETHANE
  specific = 4
FEATURE [App::DocumentObjectGroupPython] C_element035  label="C_element : 019"  # scripted group (container) (typed FeaturePython)
  n = 4
  ref = C_element
FEATURE [App::DocumentObjectGroupPython] H_element032  label="H_element : 015"  # scripted group (container) (typed FeaturePython)
  n = 10
  ref = H_element
FEATURE [App::DocumentObjectGroupPython] O_element032  label="O_element : 015"  # scripted group (container) (typed FeaturePython)
  n = 1
  ref = O_element
FEATURE [App::DocumentObjectGroupPython] G4_DIETHYL_ETHER  # scripted group (container) (typed FeaturePython)
  Dunit = g/cm3
  Dvalue = 0.71378
  Group = -> [C_element035,H_element032,O_element032]
  conduct = 2
  density = 1
  expand = 3
  formula = G4_DIETHYL_ETHER
  name = G4_DIETHYL_ETHER
  specific = 4
FEATURE [App::DocumentObjectGroupPython] C_element036  label="C_element : 020"  # scripted group (container) (typed FeaturePython)
  n = 3
  ref = C_element
FEATURE [App::DocumentObjectGroupPython] H_element033  label="H_element : 016"  # scripted group (container) (typed FeaturePython)
  n = 7
  ref = H_element
FEATURE [App::DocumentObjectGroupPython] N_element015  label="N_element : 008"  # scripted group (container) (typed FeaturePython)
  n = 1
  ref = N_element
FEATURE [App::DocumentObjectGroupPython] O_element033  label="O_element : 016"  # scripted group (container) (typed FeaturePython)
  n = 1
  ref = O_element
FEATURE [App::DocumentObjectGroupPython] G4_N_N_DIMETHYL_FORMAMIDE  label="G4_N.N-DIMETHYL_FORMAMIDE"  # scripted group (container) (typed FeaturePython)
  Dunit = g/cm3
  Dvalue = 0.9487
  Group = -> [C_element036,H_element033,N_element015,O_element033]
  conduct = 2
  density = 1
  expand = 3
  formula = G4_N.N-DIMETHYL_FORMAMIDE
  name = G4_N.N-DIMETHYL_FORMAMIDE
  specific = 4
FEATURE [App::DocumentObjectGroupPython] C_element037  label="C_element : 021"  # scripted group (container) (typed FeaturePython)
  n = 2
  ref = C_element
FEATURE [App::DocumentObjectGroupPython] H_element034  label="H_element : 017"  # scripted group (container) (typed FeaturePython)
  n = 6
  ref = H_element
FEATURE [App::DocumentObjectGroupPython] O_element034  label="O_element : 017"  # scripted group (container) (typed FeaturePython)
  n = 1
  ref = O_element
FEATURE [App::DocumentObjectGroupPython] S_element009  label="S_element : 003"  # scripted group (container) (typed FeaturePython)
  n = 1
  ref = S_element
FEATURE [App::DocumentObjectGroupPython] G4_DIMETHYL_SULFOXIDE  # scripted group (container) (typed FeaturePython)
  Dunit = g/cm3
  Dvalue = 1.1014
  Group = -> [C_element037,H_element034,O_element034,S_element009]
  conduct = 2
  density = 1
  expand = 3
  formula = G4_DIMETHYL_SULFOXIDE
  name = G4_DIMETHYL_SULFOXIDE
  specific = 4
FEATURE [App::DocumentObjectGroupPython] C_element038  label="C_element : 022"  # scripted group (container) (typed FeaturePython)
  n = 2
  ref = C_element
FEATURE [App::DocumentObjectGroupPython] H_element035  label="H_element : 018"  # scripted group (container) (typed FeaturePython)
  n = 6
  ref = H_element
FEATURE [App::DocumentObjectGroupPython] G4_ETHANE  # scripted group (container) (typed FeaturePython)
  Dunit = g/cm3
  Dvalue = 0.00125324
  Group = -> [C_element038,H_element035]
  conduct = 2
  density = 1
  expand = 3
  formula = G4_ETHANE
  name = G4_ETHANE
  specific = 4
FEATURE [App::DocumentObjectGroupPython] C_element039  label="C_element : 023"  # scripted group (container) (typed FeaturePython)
  n = 2
  ref = C_element
FEATURE [App::DocumentObjectGroupPython] H_element036  label="H_element : 019"  # scripted group (container) (typed FeaturePython)
  n = 6
  ref = H_element
FEATURE [App::DocumentObjectGroupPython] O_element035  label="O_element : 018"  # scripted group (container) (typed FeaturePython)
  n = 1
  ref = O_element
FEATURE [App::DocumentObjectGroupPython] G4_ETHYL_ALCOHOL  # scripted group (container) (typed FeaturePython)
  Dunit = g/cm3
  Dvalue = 0.7893
  Group = -> [C_element039,H_element036,O_element035]
  conduct = 2
  density = 1
  expand = 3
  formula = G4_ETHYL_ALCOHOL
  name = G4_ETHYL_ALCOHOL
  specific = 4
FEATURE [App::DocumentObjectGroupPython] H_element037  label="H_element : 0.090"  # scripted group (container) (typed FeaturePython)
  n = 0.090027
FEATURE [App::DocumentObjectGroupPython] C_element040  label="C_element : 0.585"  # scripted group (container) (typed FeaturePython)
  n = 0.585182
FEATURE [App::DocumentObjectGroupPython] O_element036  label="O_element : 0.325"  # scripted group (container) (typed FeaturePython)
  n = 0.324791
FEATURE [App::DocumentObjectGroupPython] G4_ETHYL_CELLULOSE  # scripted group (container) (typed FeaturePython)
  Dunit = g/cm3
  Dvalue = 1.13
  Group = -> [H_element037,C_element040,O_element036]
  conduct = 2
  density = 1
  expand = 3
  formula = G4_ETHYL_CELLULOSE
  name = G4_ETHYL_CELLULOSE
  specific = 4
FEATURE [App::DocumentObjectGroupPython] C_element041  label="C_element : 024"  # scripted group (container) (typed FeaturePython)
  n = 2
  ref = C_element
FEATURE [App::DocumentObjectGroupPython] H_element038  label="H_element : 020"  # scripted group (container) (typed FeaturePython)
  n = 4
  ref = H_element
FEATURE [App::DocumentObjectGroupPython] G4_ETHYLENE  # scripted group (container) (typed FeaturePython)
  Dunit = g/cm3
  Dvalue = 0.00117497
  Group = -> [C_element041,H_element038]
  conduct = 2
  density = 1
  expand = 3
  formula = G4_ETHYLENE
  name = G4_ETHYLENE
  specific = 4
FEATURE [App::DocumentObjectGroupPython] H_element039  label="H_element : 0.096"  # scripted group (container) (typed FeaturePython)
  n = 0.096
FEATURE [App::DocumentObjectGroupPython] C_element042  label="C_element : 0.195"  # scripted group (container) (typed FeaturePython)
  n = 0.195
FEATURE [App::DocumentObjectGroupPython] N_element016  label="N_element : 0.057"  # scripted group (container) (typed FeaturePython)
  n = 0.057
FEATURE [App::DocumentObjectGroupPython] O_element037  label="O_element : 0.646"  # scripted group (container) (typed FeaturePython)
  n = 0.646
FEATURE [App::DocumentObjectGroupPython] Na_element006  label="Na_element : 0.017"  # scripted group (container) (typed FeaturePython)
  n = 0.001
FEATURE [App::DocumentObjectGroupPython] P_element005  label="P_element : 0.104"  # scripted group (container) (typed FeaturePython)
  n = 0.001
FEATURE [App::DocumentObjectGroupPython] S_element010  label="S_element : 0.016"  # scripted group (container) (typed FeaturePython)
  n = 0.003
FEATURE [App::DocumentObjectGroupPython] Cl_element010  label="Cl_element : 0.005"  # scripted group (container) (typed FeaturePython)
  n = 0.001
FEATURE [App::DocumentObjectGroupPython] G4_EYE_LENS_ICRP  # scripted group (container) (typed FeaturePython)
  Dunit = g/cm3
  Dvalue = 1.07
  Group = -> [H_element039,C_element042,N_element016,O_element037,Na_element006,P_element005,S_element010,Cl_element010]
  conduct = 2
  density = 1
  expand = 3
  formula = G4_EYE_LENS_ICRP
  name = G4_EYE_LENS_ICRP
  specific = 4
FEATURE [App::DocumentObjectGroupPython] Fe_element003  label="Fe_element : 2"  # scripted group (container) (typed FeaturePython)
  n = 2
  ref = Fe_element
FEATURE [App::DocumentObjectGroupPython] O_element038  label="O_element : 019"  # scripted group (container) (typed FeaturePython)
  n = 3
  ref = O_element
FEATURE [App::DocumentObjectGroupPython] G4_FERRIC_OXIDE  # scripted group (container) (typed FeaturePython)
  Dunit = g/cm3
  Dvalue = 5.2
  Group = -> [Fe_element003,O_element038]
  conduct = 2
  density = 1
  expand = 3
  formula = G4_FERRIC_OXIDE
  name = G4_FERRIC_OXIDE
  specific = 4
FEATURE [App::DocumentObjectGroupPython] Fe_element004  label="Fe_element : 1"  # scripted group (container) (typed FeaturePython)
  n = 1
  ref = Fe_element
FEATURE [App::DocumentObjectGroupPython] B_element003  label="B_element : 1"  # scripted group (container) (typed FeaturePython)
  n = 1
  ref = B_element
FEATURE [App::DocumentObjectGroupPython] G4_FERROBORIDE  # scripted group (container) (typed FeaturePython)
  Dunit = g/cm3
  Dvalue = 7.15
  Group = -> [Fe_element004,B_element003]
  conduct = 2
  density = 1
  expand = 3
  formula = G4_FERROBORIDE
  name = G4_FERROBORIDE
  specific = 4
FEATURE [App::DocumentObjectGroupPython] Fe_element005  label="Fe_element : 003"  # scripted group (container) (typed FeaturePython)
  n = 1
  ref = Fe_element
FEATURE [App::DocumentObjectGroupPython] O_element039  label="O_element : 020"  # scripted group (container) (typed FeaturePython)
  n = 1
  ref = O_element
FEATURE [App::DocumentObjectGroupPython] G4_FERROUS_OXIDE  # scripted group (container) (typed FeaturePython)
  Dunit = g/cm3
  Dvalue = 5.7
  Group = -> [Fe_element005,O_element039]
  conduct = 2
  density = 1
  expand = 3
  formula = G4_FERROUS_OXIDE
  name = G4_FERROUS_OXIDE
  specific = 4
FEATURE [App::DocumentObjectGroupPython] H_element040  label="H_element : 0.115"  # scripted group (container) (typed FeaturePython)
  n = 0.108259
FEATURE [App::DocumentObjectGroupPython] N_element017  label="N_element : 0.000"  # scripted group (container) (typed FeaturePython)
  n = 2.7e-05
FEATURE [App::DocumentObjectGroupPython] O_element040  label="O_element : 0.879"  # scripted group (container) (typed FeaturePython)
  n = 0.878636
FEATURE [App::DocumentObjectGroupPython] Na_element007  label="Na_element : 0.000"  # scripted group (container) (typed FeaturePython)
  n = 2.2e-05
FEATURE [App::DocumentObjectGroupPython] S_element011  label="S_element : 0.013"  # scripted group (container) (typed FeaturePython)
  n = 0.012968
FEATURE [App::DocumentObjectGroupPython] Cl_element011  label="Cl_element : 0.000"  # scripted group (container) (typed FeaturePython)
  n = 3.4e-05
FEATURE [App::DocumentObjectGroupPython] Fe_element006  label="Fe_element : 0.000"  # scripted group (container) (typed FeaturePython)
  n = 5.4e-05
FEATURE [App::DocumentObjectGroupPython] G4_FERROUS_SULFATE  # scripted group (container) (typed FeaturePython)
  Dunit = g/cm3
  Dvalue = 1.024
  Group = -> [H_element040,N_element017,O_element040,Na_element007,S_element011,Cl_element011,Fe_element006]
  conduct = 2
  density = 1
  expand = 3
  formula = G4_FERROUS_SULFATE
  name = G4_FERROUS_SULFATE
  specific = 4
FEATURE [App::DocumentObjectGroupPython] C_element043  label="C_element : 0.099"  # scripted group (container) (typed FeaturePython)
  n = 0.099335
FEATURE [App::DocumentObjectGroupPython] F_element007  label="F_element : 0.314"  # scripted group (container) (typed FeaturePython)
  n = 0.314247
FEATURE [App::DocumentObjectGroupPython] Cl_element012  label="Cl_element : 0.586"  # scripted group (container) (typed FeaturePython)
  n = 0.586418
FEATURE [App::DocumentObjectGroupPython] G4_FREON_12  label="G4_FREON-12"  # scripted group (container) (typed FeaturePython)
  Dunit = g/cm3
  Dvalue = 1.12
  Group = -> [C_element043,F_element007,Cl_element012]
  conduct = 2
  density = 1
  expand = 3
  formula = G4_FREON-12
  name = G4_FREON-12
  specific = 4
FEATURE [App::DocumentObjectGroupPython] C_element044  label="C_element : 0.057"  # scripted group (container) (typed FeaturePython)
  n = 0.057245
FEATURE [App::DocumentObjectGroupPython] F_element008  label="F_element : 0.181"  # scripted group (container) (typed FeaturePython)
  n = 0.181096
FEATURE [App::DocumentObjectGroupPython] Br_element001  label="Br_element : 0.762"  # scripted group (container) (typed FeaturePython)
  n = 0.761659
FEATURE [App::DocumentObjectGroupPython] G4_FREON_12B2  label="G4_FREON-12B2"  # scripted group (container) (typed FeaturePython)
  Dunit = g/cm3
  Dvalue = 1.8
  Group = -> [C_element044,F_element008,Br_element001]
  conduct = 2
  density = 1
  expand = 3
  formula = G4_FREON-12B2
  name = G4_FREON-12B2
  specific = 4
FEATURE [App::DocumentObjectGroupPython] C_element045  label="C_element : 0.115"  # scripted group (container) (typed FeaturePython)
  n = 0.114983
FEATURE [App::DocumentObjectGroupPython] F_element009  label="F_element : 0.546"  # scripted group (container) (typed FeaturePython)
  n = 0.545621
FEATURE [App::DocumentObjectGroupPython] Cl_element013  label="Cl_element : 0.339"  # scripted group (container) (typed FeaturePython)
  n = 0.339396
FEATURE [App::DocumentObjectGroupPython] G4_FREON_13  label="G4_FREON-13"  # scripted group (container) (typed FeaturePython)
  Dunit = g/cm3
  Dvalue = 0.95
  Group = -> [C_element045,F_element009,Cl_element013]
  conduct = 2
  density = 1
  expand = 3
  formula = G4_FREON-13
  name = G4_FREON-13
  specific = 4
FEATURE [App::DocumentObjectGroupPython] C_element046  label="C_element : 025"  # scripted group (container) (typed FeaturePython)
  n = 1
  ref = C_element
FEATURE [App::DocumentObjectGroupPython] F_element010  label="F_element : 3"  # scripted group (container) (typed FeaturePython)
  n = 3
  ref = F_element
FEATURE [App::DocumentObjectGroupPython] Br_element002  label="Br_element : 1"  # scripted group (container) (typed FeaturePython)
  n = 1
  ref = Br_element
FEATURE [App::DocumentObjectGroupPython] G4_FREON_13B1  label="G4_FREON-13B1"  # scripted group (container) (typed FeaturePython)
  Dunit = g/cm3
  Dvalue = 1.5
  Group = -> [C_element046,F_element010,Br_element002]
  conduct = 2
  density = 1
  expand = 3
  formula = G4_FREON-13B1
  name = G4_FREON-13B1
  specific = 4
FEATURE [App::DocumentObjectGroupPython] C_element047  label="C_element : 0.061"  # scripted group (container) (typed FeaturePython)
  n = 0.061309
FEATURE [App::DocumentObjectGroupPython] F_element011  label="F_element : 0.291"  # scripted group (container) (typed FeaturePython)
  n = 0.290924
FEATURE [App::DocumentObjectGroupPython] I_element002  label="I_element : 0.648"  # scripted group (container) (typed FeaturePython)
  n = 0.647767
FEATURE [App::DocumentObjectGroupPython] G4_FREON_13I1  label="G4_FREON-13I1"  # scripted group (container) (typed FeaturePython)
  Dunit = g/cm3
  Dvalue = 1.8
  Group = -> [C_element047,F_element011,I_element002]
  conduct = 2
  density = 1
  expand = 3
  formula = G4_FREON-13I1
  name = G4_FREON-13I1
  specific = 4
FEATURE [App::DocumentObjectGroupPython] Gd_element001  label="Gd_element : 2"  # scripted group (container) (typed FeaturePython)
  n = 2
  ref = Gd_element
FEATURE [App::DocumentObjectGroupPython] O_element041  label="O_element : 021"  # scripted group (container) (typed FeaturePython)
  n = 2
  ref = O_element
FEATURE [App::DocumentObjectGroupPython] S_element012  label="S_element : 004"  # scripted group (container) (typed FeaturePython)
  n = 1
  ref = S_element
FEATURE [App::DocumentObjectGroupPython] G4_GADOLINIUM_OXYSULFIDE  # scripted group (container) (typed FeaturePython)
  Dunit = g/cm3
  Dvalue = 7.44
  Group = -> [Gd_element001,O_element041,S_element012]
  conduct = 2
  density = 1
  expand = 3
  formula = G4_GADOLINIUM_OXYSULFIDE
  name = G4_GADOLINIUM_OXYSULFIDE
  specific = 4
FEATURE [App::DocumentObjectGroupPython] Ga_element001  label="Ga_element : 1"  # scripted group (container) (typed FeaturePython)
  n = 1
  ref = Ga_element
FEATURE [App::DocumentObjectGroupPython] As_element001  label="As_element : 1"  # scripted group (container) (typed FeaturePython)
  n = 1
  ref = As_element
FEATURE [App::DocumentObjectGroupPython] G4_GALLIUM_ARSENIDE  # scripted group (container) (typed FeaturePython)
  Dunit = g/cm3
  Dvalue = 5.31
  Group = -> [Ga_element001,As_element001]
  conduct = 2
  density = 1
  expand = 3
  formula = G4_GALLIUM_ARSENIDE
  name = G4_GALLIUM_ARSENIDE
  specific = 4
FEATURE [App::DocumentObjectGroupPython] H_element041  label="H_element : 0.081"  # scripted group (container) (typed FeaturePython)
  n = 0.08118
FEATURE [App::DocumentObjectGroupPython] C_element048  label="C_element : 0.416"  # scripted group (container) (typed FeaturePython)
  n = 0.41606
FEATURE [App::DocumentObjectGroupPython] N_element018  label="N_element : 0.111"  # scripted group (container) (typed FeaturePython)
  n = 0.11124
FEATURE [App::DocumentObjectGroupPython] O_element042  label="O_element : 0.381"  # scripted group (container) (typed FeaturePython)
  n = 0.38064
FEATURE [App::DocumentObjectGroupPython] S_element013  label="S_element : 0.011"  # scripted group (container) (typed FeaturePython)
  n = 0.01088
FEATURE [App::DocumentObjectGroupPython] G4_GEL_PHOTO_EMULSION  # scripted group (container) (typed FeaturePython)
  Dunit = g/cm3
  Dvalue = 1.2914
  Group = -> [H_element041,C_element048,N_element018,O_element042,S_element013]
  conduct = 2
  density = 1
  expand = 3
  formula = G4_GEL_PHOTO_EMULSION
  name = G4_GEL_PHOTO_EMULSION
  specific = 4
FEATURE [App::DocumentObjectGroupPython] B_element004  label="B_element : 0.040"  # scripted group (container) (typed FeaturePython)
  n = 0.0400639
FEATURE [App::DocumentObjectGroupPython] O_element043  label="O_element : 0.540"  # scripted group (container) (typed FeaturePython)
  n = 0.539561
FEATURE [App::DocumentObjectGroupPython] Na_element008  label="Na_element : 0.028"  # scripted group (container) (typed FeaturePython)
  n = 0.0281909
FEATURE [App::DocumentObjectGroupPython] Al_element003  label="Al_element : 0.012"  # scripted group (container) (typed FeaturePython)
  n = 0.011644
FEATURE [App::DocumentObjectGroupPython] Si_element003  label="Si_element : 0.377"  # scripted group (container) (typed FeaturePython)
  n = 0.377219
FEATURE [App::DocumentObjectGroupPython] K_element004  label="K_element : 0.014"  # scripted group (container) (typed FeaturePython)
  n = 0.00332099
FEATURE [App::DocumentObjectGroupPython] G4_Pyrex_Glass  # scripted group (container) (typed FeaturePython)
  Dunit = g/cm3
  Dvalue = 2.23
  Group = -> [B_element004,O_element043,Na_element008,Al_element003,Si_element003,K_element004]
  conduct = 2
  density = 1
  expand = 3
  formula = G4_Pyrex_Glass
  name = G4_Pyrex_Glass
  specific = 4
FEATURE [App::DocumentObjectGroupPython] O_element044  label="O_element : 0.156"  # scripted group (container) (typed FeaturePython)
  n = 0.156453
FEATURE [App::DocumentObjectGroupPython] Si_element004  label="Si_element : 0.081"  # scripted group (container) (typed FeaturePython)
  n = 0.080866
FEATURE [App::DocumentObjectGroupPython] Ti_element001  label="Ti_element : 0.008"  # scripted group (container) (typed FeaturePython)
  n = 0.008092
FEATURE [App::DocumentObjectGroupPython] As_element002  label="As_element : 0.003"  # scripted group (container) (typed FeaturePython)
  n = 0.002651
FEATURE [App::DocumentObjectGroupPython] Pb_element001  label="Pb_element : 0.752"  # scripted group (container) (typed FeaturePython)
  n = 0.751938
FEATURE [App::DocumentObjectGroupPython] G4_GLASS_LEAD  # scripted group (container) (typed FeaturePython)
  Dunit = g/cm3
  Dvalue = 6.22
  Group = -> [O_element044,Si_element004,Ti_element001,As_element002,Pb_element001]
  conduct = 2
  density = 1
  expand = 3
  formula = G4_GLASS_LEAD
  name = G4_GLASS_LEAD
  specific = 4
FEATURE [App::DocumentObjectGroupPython] O_element045  label="O_element : 0.460"  # scripted group (container) (typed FeaturePython)
  n = 0.4598
FEATURE [App::DocumentObjectGroupPython] Na_element009  label="Na_element : 0.096"  # scripted group (container) (typed FeaturePython)
  n = 0.0964411
FEATURE [App::DocumentObjectGroupPython] Si_element005  label="Si_element : 0.378"  # scripted group (container) (typed FeaturePython)
  n = 0.336553
FEATURE [App::DocumentObjectGroupPython] Ca_element011  label="Ca_element : 0.107"  # scripted group (container) (typed FeaturePython)
  n = 0.107205
FEATURE [App::DocumentObjectGroupPython] G4_GLASS_PLATE  # scripted group (container) (typed FeaturePython)
  Dunit = g/cm3
  Dvalue = 2.4
  Group = -> [O_element045,Na_element009,Si_element005,Ca_element011]
  conduct = 2
  density = 1
  expand = 3
  formula = G4_GLASS_PLATE
  name = G4_GLASS_PLATE
  specific = 4
FEATURE [App::DocumentObjectGroupPython] C_element049  label="C_element : 026"  # scripted group (container) (typed FeaturePython)
  n = 5
  ref = C_element
FEATURE [App::DocumentObjectGroupPython] H_element042  label="H_element : 021"  # scripted group (container) (typed FeaturePython)
  n = 10
  ref = H_element
FEATURE [App::DocumentObjectGroupPython] N_element019  label="N_element : 2"  # scripted group (container) (typed FeaturePython)
  n = 2
  ref = N_element
FEATURE [App::DocumentObjectGroupPython] O_element046  label="O_element : 022"  # scripted group (container) (typed FeaturePython)
  n = 3
  ref = O_element
FEATURE [App::DocumentObjectGroupPython] G4_GLUTAMINE  # scripted group (container) (typed FeaturePython)
  Dunit = g/cm3
  Dvalue = 1.46
  Group = -> [C_element049,H_element042,N_element019,O_element046]
  conduct = 2
  density = 1
  expand = 3
  formula = G4_GLUTAMINE
  name = G4_GLUTAMINE
  specific = 4
FEATURE [App::DocumentObjectGroupPython] C_element050  label="C_element : 027"  # scripted group (container) (typed FeaturePython)
  n = 3
  ref = C_element
FEATURE [App::DocumentObjectGroupPython] H_element043  label="H_element : 022"  # scripted group (container) (typed FeaturePython)
  n = 8
  ref = H_element
FEATURE [App::DocumentObjectGroupPython] O_element047  label="O_element : 023"  # scripted group (container) (typed FeaturePython)
  n = 3
  ref = O_element
FEATURE [App::DocumentObjectGroupPython] G4_GLYCEROL  # scripted group (container) (typed FeaturePython)
  Dunit = g/cm3
  Dvalue = 1.2613
  Group = -> [C_element050,H_element043,O_element047]
  conduct = 2
  density = 1
  expand = 3
  formula = G4_GLYCEROL
  name = G4_GLYCEROL
  specific = 4
FEATURE [App::DocumentObjectGroupPython] C_element051  label="C_element : 028"  # scripted group (container) (typed FeaturePython)
  n = 5
  ref = C_element
FEATURE [App::DocumentObjectGroupPython] H_element044  label="H_element : 023"  # scripted group (container) (typed FeaturePython)
  n = 5
  ref = H_element
FEATURE [App::DocumentObjectGroupPython] N_element020  label="N_element : 009"  # scripted group (container) (typed FeaturePython)
  n = 5
  ref = N_element
FEATURE [App::DocumentObjectGroupPython] O_element048  label="O_element : 024"  # scripted group (container) (typed FeaturePython)
  n = 1
  ref = O_element
FEATURE [App::DocumentObjectGroupPython] G4_GUANINE  # scripted group (container) (typed FeaturePython)
  Dunit = g/cm3
  Dvalue = 2.2
  Group = -> [C_element051,H_element044,N_element020,O_element048]
  conduct = 2
  density = 1
  expand = 3
  formula = G4_GUANINE
  name = G4_GUANINE
  specific = 4
FEATURE [App::DocumentObjectGroupPython] Ca_element012  label="Ca_element : 006"  # scripted group (container) (typed FeaturePython)
  n = 1
  ref = Ca_element
FEATURE [App::DocumentObjectGroupPython] S_element014  label="S_element : 005"  # scripted group (container) (typed FeaturePython)
  n = 1
  ref = S_element
FEATURE [App::DocumentObjectGroupPython] O_element049  label="O_element : 6"  # scripted group (container) (typed FeaturePython)
  n = 6
  ref = O_element
FEATURE [App::DocumentObjectGroupPython] H_element045  label="H_element : 024"  # scripted group (container) (typed FeaturePython)
  n = 4
  ref = H_element
FEATURE [App::DocumentObjectGroupPython] G4_GYPSUM  # scripted group (container) (typed FeaturePython)
  Dunit = g/cm3
  Dvalue = 2.32
  Group = -> [Ca_element012,S_element014,O_element049,H_element045]
  conduct = 2
  density = 1
  expand = 3
  formula = G4_GYPSUM
  name = G4_GYPSUM
  specific = 4
FEATURE [App::DocumentObjectGroupPython] C_element052  label="C_element : 7"  # scripted group (container) (typed FeaturePython)
  n = 7
  ref = C_element
FEATURE [App::DocumentObjectGroupPython] H_element046  label="H_element : 16"  # scripted group (container) (typed FeaturePython)
  n = 16
  ref = H_element
FEATURE [App::DocumentObjectGroupPython] G4_N_HEPTANE  label="G4_N-HEPTANE"  # scripted group (container) (typed FeaturePython)
  Dunit = g/cm3
  Dvalue = 0.68376
  Group = -> [C_element052,H_element046]
  conduct = 2
  density = 1
  expand = 3
  formula = G4_N-HEPTANE
  name = G4_N-HEPTANE
  specific = 4
FEATURE [App::DocumentObjectGroupPython] C_element053  label="C_element : 029"  # scripted group (container) (typed FeaturePython)
  n = 6
  ref = C_element
FEATURE [App::DocumentObjectGroupPython] H_element047  label="H_element : 14"  # scripted group (container) (typed FeaturePython)
  n = 14
  ref = H_element
FEATURE [App::DocumentObjectGroupPython] G4_N_HEXANE  label="G4_N-HEXANE"  # scripted group (container) (typed FeaturePython)
  Dunit = g/cm3
  Dvalue = 0.6603
  Group = -> [C_element053,H_element047]
  conduct = 2
  density = 1
  expand = 3
  formula = G4_N-HEXANE
  name = G4_N-HEXANE
  specific = 4
FEATURE [App::DocumentObjectGroupPython] C_element054  label="C_element : 22"  # scripted group (container) (typed FeaturePython)
  n = 22
  ref = C_element
FEATURE [App::DocumentObjectGroupPython] H_element048  label="H_element : 025"  # scripted group (container) (typed FeaturePython)
  n = 10
  ref = H_element
FEATURE [App::DocumentObjectGroupPython] N_element021  label="N_element : 010"  # scripted group (container) (typed FeaturePython)
  n = 2
  ref = N_element
FEATURE [App::DocumentObjectGroupPython] O_element050  label="O_element : 025"  # scripted group (container) (typed FeaturePython)
  n = 5
  ref = O_element
FEATURE [App::DocumentObjectGroupPython] G4_KAPTON  # scripted group (container) (typed FeaturePython)
  Dunit = g/cm3
  Dvalue = 1.42
  Group = -> [C_element054,H_element048,N_element021,O_element050]
  conduct = 2
  density = 1
  expand = 3
  formula = G4_KAPTON
  name = G4_KAPTON
  specific = 4
FEATURE [App::DocumentObjectGroupPython] La_element001  label="La_element : 1"  # scripted group (container) (typed FeaturePython)
  n = 1
  ref = La_element
FEATURE [App::DocumentObjectGroupPython] Br_element003  label="Br_element : 002"  # scripted group (container) (typed FeaturePython)
  n = 1
  ref = Br_element
FEATURE [App::DocumentObjectGroupPython] O_element051  label="O_element : 026"  # scripted group (container) (typed FeaturePython)
  n = 1
  ref = O_element
FEATURE [App::DocumentObjectGroupPython] G4_LANTHANUM_OXYBROMIDE  # scripted group (container) (typed FeaturePython)
  Dunit = g/cm3
  Dvalue = 6.28
  Group = -> [La_element001,Br_element003,O_element051]
  conduct = 2
  density = 1
  expand = 3
  formula = G4_LANTHANUM_OXYBROMIDE
  name = G4_LANTHANUM_OXYBROMIDE
  specific = 4
FEATURE [App::DocumentObjectGroupPython] La_element002  label="La_element : 2"  # scripted group (container) (typed FeaturePython)
  n = 2
  ref = La_element
FEATURE [App::DocumentObjectGroupPython] O_element052  label="O_element : 027"  # scripted group (container) (typed FeaturePython)
  n = 2
  ref = O_element
FEATURE [App::DocumentObjectGroupPython] S_element015  label="S_element : 006"  # scripted group (container) (typed FeaturePython)
  n = 1
  ref = S_element
FEATURE [App::DocumentObjectGroupPython] G4_LANTHANUM_OXYSULFIDE  # scripted group (container) (typed FeaturePython)
  Dunit = g/cm3
  Dvalue = 5.86
  Group = -> [La_element002,O_element052,S_element015]
  conduct = 2
  density = 1
  expand = 3
  formula = G4_LANTHANUM_OXYSULFIDE
  name = G4_LANTHANUM_OXYSULFIDE
  specific = 4
FEATURE [App::DocumentObjectGroupPython] O_element053  label="O_element : 0.072"  # scripted group (container) (typed FeaturePython)
  n = 0.071682
FEATURE [App::DocumentObjectGroupPython] Pb_element002  label="Pb_element : 0.928"  # scripted group (container) (typed FeaturePython)
  n = 0.928318
FEATURE [App::DocumentObjectGroupPython] G4_LEAD_OXIDE  # scripted group (container) (typed FeaturePython)
  Dunit = g/cm3
  Dvalue = 9.53
  Group = -> [O_element053,Pb_element002]
  conduct = 2
  density = 1
  expand = 3
  formula = G4_LEAD_OXIDE
  name = G4_LEAD_OXIDE
  specific = 4
FEATURE [App::DocumentObjectGroupPython] Li_element001  label="Li_element : 1"  # scripted group (container) (typed FeaturePython)
  n = 1
  ref = Li_element
FEATURE [App::DocumentObjectGroupPython] N_element022  label="N_element : 011"  # scripted group (container) (typed FeaturePython)
  n = 1
  ref = N_element
FEATURE [App::DocumentObjectGroupPython] H_element049  label="H_element : 026"  # scripted group (container) (typed FeaturePython)
  n = 2
  ref = H_element
FEATURE [App::DocumentObjectGroupPython] G4_LITHIUM_AMIDE  # scripted group (container) (typed FeaturePython)
  Dunit = g/cm3
  Dvalue = 1.178
  Group = -> [Li_element001,N_element022,H_element049]
  conduct = 2
  density = 1
  expand = 3
  formula = G4_LITHIUM_AMIDE
  name = G4_LITHIUM_AMIDE
  specific = 4
FEATURE [App::DocumentObjectGroupPython] Li_element002  label="Li_element : 2"  # scripted group (container) (typed FeaturePython)
  n = 2
  ref = Li_element
FEATURE [App::DocumentObjectGroupPython] C_element055  label="C_element : 030"  # scripted group (container) (typed FeaturePython)
  n = 1
  ref = C_element
FEATURE [App::DocumentObjectGroupPython] O_element054  label="O_element : 028"  # scripted group (container) (typed FeaturePython)
  n = 3
  ref = O_element
FEATURE [App::DocumentObjectGroupPython] G4_LITHIUM_CARBONATE  # scripted group (container) (typed FeaturePython)
  Dunit = g/cm3
  Dvalue = 2.11
  Group = -> [Li_element002,C_element055,O_element054]
  conduct = 2
  density = 1
  expand = 3
  formula = G4_LITHIUM_CARBONATE
  name = G4_LITHIUM_CARBONATE
  specific = 4
FEATURE [App::DocumentObjectGroupPython] Li_element003  label="Li_element : 003"  # scripted group (container) (typed FeaturePython)
  n = 1
  ref = Li_element
FEATURE [App::DocumentObjectGroupPython] F_element012  label="F_element : 004"  # scripted group (container) (typed FeaturePython)
  n = 1
  ref = F_element
FEATURE [App::DocumentObjectGroupPython] G4_LITHIUM_FLUORIDE  # scripted group (container) (typed FeaturePython)
  Dunit = g/cm3
  Dvalue = 2.635
  Group = -> [Li_element003,F_element012]
  conduct = 2
  density = 1
  expand = 3
  formula = G4_LITHIUM_FLUORIDE
  name = G4_LITHIUM_FLUORIDE
  specific = 4
FEATURE [App::DocumentObjectGroupPython] Li_element004  label="Li_element : 004"  # scripted group (container) (typed FeaturePython)
  n = 1
  ref = Li_element
FEATURE [App::DocumentObjectGroupPython] H_element050  label="H_element : 027"  # scripted group (container) (typed FeaturePython)
  n = 1
  ref = H_element
FEATURE [App::DocumentObjectGroupPython] G4_LITHIUM_HYDRIDE  # scripted group (container) (typed FeaturePython)
  Dunit = g/cm3
  Dvalue = 0.82
  Group = -> [Li_element004,H_element050]
  conduct = 2
  density = 1
  expand = 3
  formula = G4_LITHIUM_HYDRIDE
  name = G4_LITHIUM_HYDRIDE
  specific = 4
FEATURE [App::DocumentObjectGroupPython] Li_element005  label="Li_element : 005"  # scripted group (container) (typed FeaturePython)
  n = 1
  ref = Li_element
FEATURE [App::DocumentObjectGroupPython] I_element003  label="I_element : 002"  # scripted group (container) (typed FeaturePython)
  n = 1
  ref = I_element
FEATURE [App::DocumentObjectGroupPython] G4_LITHIUM_IODIDE  # scripted group (container) (typed FeaturePython)
  Dunit = g/cm3
  Dvalue = 3.494
  Group = -> [Li_element005,I_element003]
  conduct = 2
  density = 1
  expand = 3
  formula = G4_LITHIUM_IODIDE
  name = G4_LITHIUM_IODIDE
  specific = 4
FEATURE [App::DocumentObjectGroupPython] Li_element006  label="Li_element : 006"  # scripted group (container) (typed FeaturePython)
  n = 2
  ref = Li_element
FEATURE [App::DocumentObjectGroupPython] O_element055  label="O_element : 029"  # scripted group (container) (typed FeaturePython)
  n = 1
  ref = O_element
FEATURE [App::DocumentObjectGroupPython] G4_LITHIUM_OXIDE  # scripted group (container) (typed FeaturePython)
  Dunit = g/cm3
  Dvalue = 2.013
  Group = -> [Li_element006,O_element055]
  conduct = 2
  density = 1
  expand = 3
  formula = G4_LITHIUM_OXIDE
  name = G4_LITHIUM_OXIDE
  specific = 4
FEATURE [App::DocumentObjectGroupPython] Li_element007  label="Li_element : 007"  # scripted group (container) (typed FeaturePython)
  n = 2
  ref = Li_element
FEATURE [App::DocumentObjectGroupPython] B_element005  label="B_element : 005"  # scripted group (container) (typed FeaturePython)
  n = 4
  ref = B_element
FEATURE [App::DocumentObjectGroupPython] O_element056  label="O_element : 7"  # scripted group (container) (typed FeaturePython)
  n = 7
  ref = O_element
FEATURE [App::DocumentObjectGroupPython] G4_LITHIUM_TETRABORATE  # scripted group (container) (typed FeaturePython)
  Dunit = g/cm3
  Dvalue = 2.44
  Group = -> [Li_element007,B_element005,O_element056]
  conduct = 2
  density = 1
  expand = 3
  formula = G4_LITHIUM_TETRABORATE
  name = G4_LITHIUM_TETRABORATE
  specific = 4
FEATURE [App::DocumentObjectGroupPython] H_element051  label="H_element : 0.105"  # scripted group (container) (typed FeaturePython)
  n = 0.105
FEATURE [App::DocumentObjectGroupPython] C_element056  label="C_element : 0.083"  # scripted group (container) (typed FeaturePython)
  n = 0.083
FEATURE [App::DocumentObjectGroupPython] N_element023  label="N_element : 0.023"  # scripted group (container) (typed FeaturePython)
  n = 0.023
FEATURE [App::DocumentObjectGroupPython] O_element057  label="O_element : 0.779"  # scripted group (container) (typed FeaturePython)
  n = 0.779
FEATURE [App::DocumentObjectGroupPython] Na_element010  label="Na_element : 0.097"  # scripted group (container) (typed FeaturePython)
  n = 0.002
FEATURE [App::DocumentObjectGroupPython] P_element006  label="P_element : 0.105"  # scripted group (container) (typed FeaturePython)
  n = 0.001
FEATURE [App::DocumentObjectGroupPython] S_element016  label="S_element : 0.017"  # scripted group (container) (typed FeaturePython)
  n = 0.002
FEATURE [App::DocumentObjectGroupPython] Cl_element014  label="Cl_element : 0.587"  # scripted group (container) (typed FeaturePython)
  n = 0.003
FEATURE [App::DocumentObjectGroupPython] K_element005  label="K_element : 0.015"  # scripted group (container) (typed FeaturePython)
  n = 0.002
FEATURE [App::DocumentObjectGroupPython] G4_LUNG_ICRP  # scripted group (container) (typed FeaturePython)
  Dunit = g/cm3
  Dvalue = 1.04
  Group = -> [H_element051,C_element056,N_element023,O_element057,Na_element010,P_element006,S_element016,Cl_element014,K_element005]
  conduct = 2
  density = 1
  expand = 3
  formula = G4_LUNG_ICRP
  name = G4_LUNG_ICRP
  specific = 4
FEATURE [App::DocumentObjectGroupPython] H_element052  label="H_element : 0.116"  # scripted group (container) (typed FeaturePython)
  n = 0.114318
FEATURE [App::DocumentObjectGroupPython] C_element057  label="C_element : 0.656"  # scripted group (container) (typed FeaturePython)
  n = 0.655824
FEATURE [App::DocumentObjectGroupPython] O_element058  label="O_element : 0.092"  # scripted group (container) (typed FeaturePython)
  n = 0.0921831
FEATURE [App::DocumentObjectGroupPython] Mg_element004  label="Mg_element : 0.135"  # scripted group (container) (typed FeaturePython)
  n = 0.134792
FEATURE [App::DocumentObjectGroupPython] Ca_element013  label="Ca_element : 0.003"  # scripted group (container) (typed FeaturePython)
  n = 0.002883
FEATURE [App::DocumentObjectGroupPython] G4_M3_WAX  # scripted group (container) (typed FeaturePython)
  Dunit = g/cm3
  Dvalue = 1.05
  Group = -> [H_element052,C_element057,O_element058,Mg_element004,Ca_element013]
  conduct = 2
  density = 1
  expand = 3
  formula = G4_M3_WAX
  name = G4_M3_WAX
  specific = 4
FEATURE [App::DocumentObjectGroupPython] Mg_element005  label="Mg_element : 1"  # scripted group (container) (typed FeaturePython)
  n = 1
  ref = Mg_element
FEATURE [App::DocumentObjectGroupPython] C_element058  label="C_element : 031"  # scripted group (container) (typed FeaturePython)
  n = 1
  ref = C_element
FEATURE [App::DocumentObjectGroupPython] O_element059  label="O_element : 030"  # scripted group (container) (typed FeaturePython)
  n = 3
  ref = O_element
FEATURE [App::DocumentObjectGroupPython] G4_MAGNESIUM_CARBONATE  # scripted group (container) (typed FeaturePython)
  Dunit = g/cm3
  Dvalue = 2.958
  Group = -> [Mg_element005,C_element058,O_element059]
  conduct = 2
  density = 1
  expand = 3
  formula = G4_MAGNESIUM_CARBONATE
  name = G4_MAGNESIUM_CARBONATE
  specific = 4
FEATURE [App::DocumentObjectGroupPython] Mg_element006  label="Mg_element : 002"  # scripted group (container) (typed FeaturePython)
  n = 1
  ref = Mg_element
FEATURE [App::DocumentObjectGroupPython] F_element013  label="F_element : 005"  # scripted group (container) (typed FeaturePython)
  n = 2
  ref = F_element
FEATURE [App::DocumentObjectGroupPython] G4_MAGNESIUM_FLUORIDE  # scripted group (container) (typed FeaturePython)
  Dunit = g/cm3
  Dvalue = 3
  Group = -> [Mg_element006,F_element013]
  conduct = 2
  density = 1
  expand = 3
  formula = G4_MAGNESIUM_FLUORIDE
  name = G4_MAGNESIUM_FLUORIDE
  specific = 4
FEATURE [App::DocumentObjectGroupPython] Mg_element007  label="Mg_element : 003"  # scripted group (container) (typed FeaturePython)
  n = 1
  ref = Mg_element
FEATURE [App::DocumentObjectGroupPython] O_element060  label="O_element : 031"  # scripted group (container) (typed FeaturePython)
  n = 1
  ref = O_element
FEATURE [App::DocumentObjectGroupPython] G4_MAGNESIUM_OXIDE  # scripted group (container) (typed FeaturePython)
  Dunit = g/cm3
  Dvalue = 3.58
  Group = -> [Mg_element007,O_element060]
  conduct = 2
  density = 1
  expand = 3
  formula = G4_MAGNESIUM_OXIDE
  name = G4_MAGNESIUM_OXIDE
  specific = 4
FEATURE [App::DocumentObjectGroupPython] Mg_element008  label="Mg_element : 004"  # scripted group (container) (typed FeaturePython)
  n = 1
  ref = Mg_element
FEATURE [App::DocumentObjectGroupPython] B_element006  label="B_element : 006"  # scripted group (container) (typed FeaturePython)
  n = 4
  ref = B_element
FEATURE [App::DocumentObjectGroupPython] O_element061  label="O_element : 032"  # scripted group (container) (typed FeaturePython)
  n = 7
  ref = O_element
FEATURE [App::DocumentObjectGroupPython] G4_MAGNESIUM_TETRABORATE  # scripted group (container) (typed FeaturePython)
  Dunit = g/cm3
  Dvalue = 2.53
  Group = -> [Mg_element008,B_element006,O_element061]
  conduct = 2
  density = 1
  expand = 3
  formula = G4_MAGNESIUM_TETRABORATE
  name = G4_MAGNESIUM_TETRABORATE
  specific = 4
FEATURE [App::DocumentObjectGroupPython] Hg_element001  label="Hg_element : 1"  # scripted group (container) (typed FeaturePython)
  n = 1
  ref = Hg_element
FEATURE [App::DocumentObjectGroupPython] I_element004  label="I_element : 2"  # scripted group (container) (typed FeaturePython)
  n = 2
  ref = I_element
FEATURE [App::DocumentObjectGroupPython] G4_MERCURIC_IODIDE  # scripted group (container) (typed FeaturePython)
  Dunit = g/cm3
  Dvalue = 6.36
  Group = -> [Hg_element001,I_element004]
  conduct = 2
  density = 1
  expand = 3
  formula = G4_MERCURIC_IODIDE
  name = G4_MERCURIC_IODIDE
  specific = 4
FEATURE [App::DocumentObjectGroupPython] C_element059  label="C_element : 032"  # scripted group (container) (typed FeaturePython)
  n = 1
  ref = C_element
FEATURE [App::DocumentObjectGroupPython] H_element053  label="H_element : 028"  # scripted group (container) (typed FeaturePython)
  n = 4
  ref = H_element
FEATURE [App::DocumentObjectGroupPython] G4_METHANE  # scripted group (container) (typed FeaturePython)
  Dunit = g/cm3
  Dvalue = 0.000667151
  Group = -> [C_element059,H_element053]
  conduct = 2
  density = 1
  expand = 3
  formula = G4_METHANE
  name = G4_METHANE
  specific = 4
FEATURE [App::DocumentObjectGroupPython] C_element060  label="C_element : 033"  # scripted group (container) (typed FeaturePython)
  n = 1
  ref = C_element
FEATURE [App::DocumentObjectGroupPython] H_element054  label="H_element : 029"  # scripted group (container) (typed FeaturePython)
  n = 4
  ref = H_element
FEATURE [App::DocumentObjectGroupPython] O_element062  label="O_element : 033"  # scripted group (container) (typed FeaturePython)
  n = 1
  ref = O_element
FEATURE [App::DocumentObjectGroupPython] G4_METHANOL  # scripted group (container) (typed FeaturePython)
  Dunit = g/cm3
  Dvalue = 0.7914
  Group = -> [C_element060,H_element054,O_element062]
  conduct = 2
  density = 1
  expand = 3
  formula = G4_METHANOL
  name = G4_METHANOL
  specific = 4
FEATURE [App::DocumentObjectGroupPython] H_element055  label="H_element : 0.134"  # scripted group (container) (typed FeaturePython)
  n = 0.13404
FEATURE [App::DocumentObjectGroupPython] C_element061  label="C_element : 0.778"  # scripted group (container) (typed FeaturePython)
  n = 0.77796
FEATURE [App::DocumentObjectGroupPython] O_element063  label="O_element : 0.035"  # scripted group (container) (typed FeaturePython)
  n = 0.03502
FEATURE [App::DocumentObjectGroupPython] Mg_element009  label="Mg_element : 0.039"  # scripted group (container) (typed FeaturePython)
  n = 0.038594
FEATURE [App::DocumentObjectGroupPython] Ti_element002  label="Ti_element : 0.014"  # scripted group (container) (typed FeaturePython)
  n = 0.014386
FEATURE [App::DocumentObjectGroupPython] G4_MIX_D_WAX  # scripted group (container) (typed FeaturePython)
  Dunit = g/cm3
  Dvalue = 0.99
  Group = -> [H_element055,C_element061,O_element063,Mg_element009,Ti_element002]
  conduct = 2
  density = 1
  expand = 3
  formula = G4_MIX_D_WAX
  name = G4_MIX_D_WAX
  specific = 4
FEATURE [App::DocumentObjectGroupPython] H_element056  label="H_element : 0.135"  # scripted group (container) (typed FeaturePython)
  n = 0.081192
FEATURE [App::DocumentObjectGroupPython] C_element062  label="C_element : 0.583"  # scripted group (container) (typed FeaturePython)
  n = 0.583442
FEATURE [App::DocumentObjectGroupPython] N_element024  label="N_element : 0.018"  # scripted group (container) (typed FeaturePython)
  n = 0.017798
FEATURE [App::DocumentObjectGroupPython] O_element064  label="O_element : 0.186"  # scripted group (container) (typed FeaturePython)
  n = 0.186381
FEATURE [App::DocumentObjectGroupPython] Mg_element010  label="Mg_element : 0.130"  # scripted group (container) (typed FeaturePython)
  n = 0.130287
FEATURE [App::DocumentObjectGroupPython] Cl_element015  label="Cl_element : 0.588"  # scripted group (container) (typed FeaturePython)
  n = 0.0009
FEATURE [App::DocumentObjectGroupPython] G4_MS20_TISSUE  # scripted group (container) (typed FeaturePython)
  Dunit = g/cm3
  Dvalue = 1
  Group = -> [H_element056,C_element062,N_element024,O_element064,Mg_element010,Cl_element015]
  conduct = 2
  density = 1
  expand = 3
  formula = G4_MS20_TISSUE
  name = G4_MS20_TISSUE
  specific = 4
FEATURE [App::DocumentObjectGroupPython] H_element057  label="H_element : 0.136"  # scripted group (container) (typed FeaturePython)
  n = 0.102
FEATURE [App::DocumentObjectGroupPython] C_element063  label="C_element : 0.143"  # scripted group (container) (typed FeaturePython)
  n = 0.143
FEATURE [App::DocumentObjectGroupPython] N_element025  label="N_element : 0.034"  # scripted group (container) (typed FeaturePython)
  n = 0.034
FEATURE [App::DocumentObjectGroupPython] O_element065  label="O_element : 0.710"  # scripted group (container) (typed FeaturePython)
  n = 0.71
FEATURE [App::DocumentObjectGroupPython] Na_element011  label="Na_element : 0.098"  # scripted group (container) (typed FeaturePython)
  n = 0.001
FEATURE [App::DocumentObjectGroupPython] P_element007  label="P_element : 0.002"  # scripted group (container) (typed FeaturePython)
  n = 0.002
FEATURE [App::DocumentObjectGroupPython] S_element017  label="S_element : 0.018"  # scripted group (container) (typed FeaturePython)
  n = 0.003
FEATURE [App::DocumentObjectGroupPython] Cl_element016  label="Cl_element : 0.589"  # scripted group (container) (typed FeaturePython)
  n = 0.001
FEATURE [App::DocumentObjectGroupPython] K_element006  label="K_element : 0.004"  # scripted group (container) (typed FeaturePython)
  n = 0.004
FEATURE [App::DocumentObjectGroupPython] G4_MUSCLE_SKELETAL_ICRP  # scripted group (container) (typed FeaturePython)
  Dunit = g/cm3
  Dvalue = 1.05
  Group = -> [H_element057,C_element063,N_element025,O_element065,Na_element011,P_element007,S_element017,Cl_element016,K_element006]
  conduct = 2
  density = 1
  expand = 3
  formula = G4_MUSCLE_SKELETAL_ICRP
  name = G4_MUSCLE_SKELETAL_ICRP
  specific = 4
FEATURE [App::DocumentObjectGroupPython] H_element058  label="H_element : 0.137"  # scripted group (container) (typed FeaturePython)
  n = 0.102102
FEATURE [App::DocumentObjectGroupPython] C_element064  label="C_element : 0.123"  # scripted group (container) (typed FeaturePython)
  n = 0.123123
FEATURE [App::DocumentObjectGroupPython] N_element026  label="N_element : 0.756"  # scripted group (container) (typed FeaturePython)
  n = 0.035035
FEATURE [App::DocumentObjectGroupPython] O_element066  label="O_element : 0.730"  # scripted group (container) (typed FeaturePython)
  n = 0.72973
FEATURE [App::DocumentObjectGroupPython] Na_element012  label="Na_element : 0.099"  # scripted group (container) (typed FeaturePython)
  n = 0.001001
FEATURE [App::DocumentObjectGroupPython] P_element008  label="P_element : 0.106"  # scripted group (container) (typed FeaturePython)
  n = 0.002002
FEATURE [App::DocumentObjectGroupPython] S_element018  label="S_element : 0.019"  # scripted group (container) (typed FeaturePython)
  n = 0.004004
FEATURE [App::DocumentObjectGroupPython] K_element007  label="K_element : 0.016"  # scripted group (container) (typed FeaturePython)
  n = 0.003003
FEATURE [App::DocumentObjectGroupPython] G4_MUSCLE_STRIATED_ICRU  # scripted group (container) (typed FeaturePython)
  Dunit = g/cm3
  Dvalue = 1.04
  Group = -> [H_element058,C_element064,N_element026,O_element066,Na_element012,P_element008,S_element018,K_element007]
  conduct = 2
  density = 1
  expand = 3
  formula = G4_MUSCLE_STRIATED_ICRU
  name = G4_MUSCLE_STRIATED_ICRU
  specific = 4
FEATURE [App::DocumentObjectGroupPython] H_element059  label="H_element : 0.098"  # scripted group (container) (typed FeaturePython)
  n = 0.0982341
FEATURE [App::DocumentObjectGroupPython] C_element065  label="C_element : 0.156"  # scripted group (container) (typed FeaturePython)
  n = 0.156214
FEATURE [App::DocumentObjectGroupPython] N_element027  label="N_element : 0.757"  # scripted group (container) (typed FeaturePython)
  n = 0.035451
FEATURE [App::DocumentObjectGroupPython] O_element067  label="O_element : 0.880"  # scripted group (container) (typed FeaturePython)
  n = 0.710101
FEATURE [App::DocumentObjectGroupPython] G4_MUSCLE_WITH_SUCROSE  # scripted group (container) (typed FeaturePython)
  Dunit = g/cm3
  Dvalue = 1.11
  Group = -> [H_element059,C_element065,N_element027,O_element067]
  conduct = 2
  density = 1
  expand = 3
  formula = G4_MUSCLE_WITH_SUCROSE
  name = G4_MUSCLE_WITH_SUCROSE
  specific = 4
FEATURE [App::DocumentObjectGroupPython] H_element060  label="H_element : 0.138"  # scripted group (container) (typed FeaturePython)
  n = 0.101969
FEATURE [App::DocumentObjectGroupPython] C_element066  label="C_element : 0.120"  # scripted group (container) (typed FeaturePython)
  n = 0.120058
FEATURE [App::DocumentObjectGroupPython] N_element028  label="N_element : 0.758"  # scripted group (container) (typed FeaturePython)
  n = 0.035451
FEATURE [App::DocumentObjectGroupPython] O_element068  label="O_element : 0.743"  # scripted group (container) (typed FeaturePython)
  n = 0.742522
FEATURE [App::DocumentObjectGroupPython] G4_MUSCLE_WITHOUT_SUCROSE  # scripted group (container) (typed FeaturePython)
  Dunit = g/cm3
  Dvalue = 1.07
  Group = -> [H_element060,C_element066,N_element028,O_element068]
  conduct = 2
  density = 1
  expand = 3
  formula = G4_MUSCLE_WITHOUT_SUCROSE
  name = G4_MUSCLE_WITHOUT_SUCROSE
  specific = 4
FEATURE [App::DocumentObjectGroupPython] C_element067  label="C_element : 10"  # scripted group (container) (typed FeaturePython)
  n = 10
  ref = C_element
FEATURE [App::DocumentObjectGroupPython] H_element061  label="H_element : 030"  # scripted group (container) (typed FeaturePython)
  n = 8
  ref = H_element
FEATURE [App::DocumentObjectGroupPython] G4_NAPHTHALENE  # scripted group (container) (typed FeaturePython)
  Dunit = g/cm3
  Dvalue = 1.145
  Group = -> [C_element067,H_element061]
  conduct = 2
  density = 1
  expand = 3
  formula = G4_NAPHTHALENE
  name = G4_NAPHTHALENE
  specific = 4
FEATURE [App::DocumentObjectGroupPython] C_element068  label="C_element : 034"  # scripted group (container) (typed FeaturePython)
  n = 6
  ref = C_element
FEATURE [App::DocumentObjectGroupPython] H_element062  label="H_element : 031"  # scripted group (container) (typed FeaturePython)
  n = 5
  ref = H_element
FEATURE [App::DocumentObjectGroupPython] N_element029  label="N_element : 012"  # scripted group (container) (typed FeaturePython)
  n = 1
  ref = N_element
FEATURE [App::DocumentObjectGroupPython] O_element069  label="O_element : 034"  # scripted group (container) (typed FeaturePython)
  n = 2
  ref = O_element
FEATURE [App::DocumentObjectGroupPython] G4_NITROBENZENE  # scripted group (container) (typed FeaturePython)
  Dunit = g/cm3
  Dvalue = 1.19867
  Group = -> [C_element068,H_element062,N_element029,O_element069]
  conduct = 2
  density = 1
  expand = 3
  formula = G4_NITROBENZENE
  name = G4_NITROBENZENE
  specific = 4
FEATURE [App::DocumentObjectGroupPython] N_element030  label="N_element : 013"  # scripted group (container) (typed FeaturePython)
  n = 2
  ref = N_element
FEATURE [App::DocumentObjectGroupPython] O_element070  label="O_element : 035"  # scripted group (container) (typed FeaturePython)
  n = 1
  ref = O_element
FEATURE [App::DocumentObjectGroupPython] G4_NITROUS_OXIDE  # scripted group (container) (typed FeaturePython)
  Dunit = g/cm3
  Dvalue = 0.00183094
  Group = -> [N_element030,O_element070]
  conduct = 2
  density = 1
  expand = 3
  formula = G4_NITROUS_OXIDE
  name = G4_NITROUS_OXIDE
  specific = 4
FEATURE [App::DocumentObjectGroupPython] H_element063  label="H_element : 0.104"  # scripted group (container) (typed FeaturePython)
  n = 0.103509
FEATURE [App::DocumentObjectGroupPython] C_element069  label="C_element : 0.648"  # scripted group (container) (typed FeaturePython)
  n = 0.648416
FEATURE [App::DocumentObjectGroupPython] N_element031  label="N_element : 0.100"  # scripted group (container) (typed FeaturePython)
  n = 0.0995361
FEATURE [App::DocumentObjectGroupPython] O_element071  label="O_element : 0.149"  # scripted group (container) (typed FeaturePython)
  n = 0.148539
FEATURE [App::DocumentObjectGroupPython] G4_NYLON_8062  label="G4_NYLON-8062"  # scripted group (container) (typed FeaturePython)
  Dunit = g/cm3
  Dvalue = 1.08
  Group = -> [H_element063,C_element069,N_element031,O_element071]
  conduct = 2
  density = 1
  expand = 3
  formula = G4_NYLON-8062
  name = G4_NYLON-8062
  specific = 4
FEATURE [App::DocumentObjectGroupPython] C_element070  label="C_element : 035"  # scripted group (container) (typed FeaturePython)
  n = 6
  ref = C_element
FEATURE [App::DocumentObjectGroupPython] H_element064  label="H_element : 11"  # scripted group (container) (typed FeaturePython)
  n = 11
  ref = H_element
FEATURE [App::DocumentObjectGroupPython] N_element032  label="N_element : 014"  # scripted group (container) (typed FeaturePython)
  n = 1
  ref = N_element
FEATURE [App::DocumentObjectGroupPython] O_element072  label="O_element : 036"  # scripted group (container) (typed FeaturePython)
  n = 1
  ref = O_element
FEATURE [App::DocumentObjectGroupPython] G4_NYLON_6_6  label="G4_NYLON-6-6"  # scripted group (container) (typed FeaturePython)
  Dunit = g/cm3
  Dvalue = 1.14
  Group = -> [C_element070,H_element064,N_element032,O_element072]
  conduct = 2
  density = 1
  expand = 3
  formula = G4_NYLON-6-6
  name = G4_NYLON-6-6
  specific = 4
FEATURE [App::DocumentObjectGroupPython] H_element065  label="H_element : 0.139"  # scripted group (container) (typed FeaturePython)
  n = 0.107062
FEATURE [App::DocumentObjectGroupPython] C_element071  label="C_element : 0.680"  # scripted group (container) (typed FeaturePython)
  n = 0.680449
FEATURE [App::DocumentObjectGroupPython] N_element033  label="N_element : 0.099"  # scripted group (container) (typed FeaturePython)
  n = 0.099189
FEATURE [App::DocumentObjectGroupPython] O_element073  label="O_element : 0.113"  # scripted group (container) (typed FeaturePython)
  n = 0.1133
FEATURE [App::DocumentObjectGroupPython] G4_NYLON_6_10  label="G4_NYLON-6-10"  # scripted group (container) (typed FeaturePython)
  Dunit = g/cm3
  Dvalue = 1.14
  Group = -> [H_element065,C_element071,N_element033,O_element073]
  conduct = 2
  density = 1
  expand = 3
  formula = G4_NYLON-6-10
  name = G4_NYLON-6-10
  specific = 4
FEATURE [App::DocumentObjectGroupPython] H_element066  label="H_element : 0.140"  # scripted group (container) (typed FeaturePython)
  n = 0.115476
FEATURE [App::DocumentObjectGroupPython] C_element072  label="C_element : 0.721"  # scripted group (container) (typed FeaturePython)
  n = 0.720818
FEATURE [App::DocumentObjectGroupPython] N_element034  label="N_element : 0.076"  # scripted group (container) (typed FeaturePython)
  n = 0.0764169
FEATURE [App::DocumentObjectGroupPython] O_element074  label="O_element : 0.087"  # scripted group (container) (typed FeaturePython)
  n = 0.0872889
FEATURE [App::DocumentObjectGroupPython] G4_NYLON_11_RILSAN  label="G4_NYLON-11_RILSAN"  # scripted group (container) (typed FeaturePython)
  Dunit = g/cm3
  Dvalue = 1.425
  Group = -> [H_element066,C_element072,N_element034,O_element074]
  conduct = 2
  density = 1
  expand = 3
  formula = G4_NYLON-11_RILSAN
  name = G4_NYLON-11_RILSAN
  specific = 4
FEATURE [App::DocumentObjectGroupPython] C_element073  label="C_element : 8"  # scripted group (container) (typed FeaturePython)
  n = 8
  ref = C_element
FEATURE [App::DocumentObjectGroupPython] H_element067  label="H_element : 18"  # scripted group (container) (typed FeaturePython)
  n = 18
  ref = H_element
FEATURE [App::DocumentObjectGroupPython] G4_OCTANE  # scripted group (container) (typed FeaturePython)
  Dunit = g/cm3
  Dvalue = 0.7026
  Group = -> [C_element073,H_element067]
  conduct = 2
  density = 1
  expand = 3
  formula = G4_OCTANE
  name = G4_OCTANE
  specific = 4
FEATURE [App::DocumentObjectGroupPython] C_element074  label="C_element : 25"  # scripted group (container) (typed FeaturePython)
  n = 25
  ref = C_element
FEATURE [App::DocumentObjectGroupPython] H_element068  label="H_element : 52"  # scripted group (container) (typed FeaturePython)
  n = 52
  ref = H_element
FEATURE [App::DocumentObjectGroupPython] G4_PARAFFIN  # scripted group (container) (typed FeaturePython)
  Dunit = g/cm3
  Dvalue = 0.93
  Group = -> [C_element074,H_element068]
  conduct = 2
  density = 1
  expand = 3
  formula = G4_PARAFFIN
  name = G4_PARAFFIN
  specific = 4
FEATURE [App::DocumentObjectGroupPython] C_element075  label="C_element : 036"  # scripted group (container) (typed FeaturePython)
  n = 5
  ref = C_element
FEATURE [App::DocumentObjectGroupPython] H_element069  label="H_element : 032"  # scripted group (container) (typed FeaturePython)
  n = 12
  ref = H_element
FEATURE [App::DocumentObjectGroupPython] G4_N_PENTANE  label="G4_N-PENTANE"  # scripted group (container) (typed FeaturePython)
  Dunit = g/cm3
  Dvalue = 0.6262
  Group = -> [C_element075,H_element069]
  conduct = 2
  density = 1
  expand = 3
  formula = G4_N-PENTANE
  name = G4_N-PENTANE
  specific = 4
FEATURE [App::DocumentObjectGroupPython] H_element070  label="H_element : 0.014"  # scripted group (container) (typed FeaturePython)
  n = 0.0141
FEATURE [App::DocumentObjectGroupPython] C_element076  label="C_element : 0.072"  # scripted group (container) (typed FeaturePython)
  n = 0.072261
FEATURE [App::DocumentObjectGroupPython] N_element035  label="N_element : 0.019"  # scripted group (container) (typed FeaturePython)
  n = 0.01932
FEATURE [App::DocumentObjectGroupPython] O_element075  label="O_element : 0.066"  # scripted group (container) (typed FeaturePython)
  n = 0.066101
FEATURE [App::DocumentObjectGroupPython] S_element019  label="S_element : 0.020"  # scripted group (container) (typed FeaturePython)
  n = 0.00189
FEATURE [App::DocumentObjectGroupPython] Br_element004  label="Br_element : 0.349"  # scripted group (container) (typed FeaturePython)
  n = 0.349103
FEATURE [App::DocumentObjectGroupPython] Ag_element001  label="Ag_element : 0.474"  # scripted group (container) (typed FeaturePython)
  n = 0.474105
FEATURE [App::DocumentObjectGroupPython] I_element005  label="I_element : 0.003"  # scripted group (container) (typed FeaturePython)
  n = 0.00312
FEATURE [App::DocumentObjectGroupPython] G4_PHOTO_EMULSION  # scripted group (container) (typed FeaturePython)
  Dunit = g/cm3
  Dvalue = 3.815
  Group = -> [H_element070,C_element076,N_element035,O_element075,S_element019,Br_element004,Ag_element001,I_element005]
  conduct = 2
  density = 1
  expand = 3
  formula = G4_PHOTO_EMULSION
  name = G4_PHOTO_EMULSION
  specific = 4
FEATURE [App::DocumentObjectGroupPython] C_element077  label="C_element : 9"  # scripted group (container) (typed FeaturePython)
  n = 9
  ref = C_element
FEATURE [App::DocumentObjectGroupPython] H_element071  label="H_element : 033"  # scripted group (container) (typed FeaturePython)
  n = 10
  ref = H_element
FEATURE [App::DocumentObjectGroupPython] G4_PLASTIC_SC_VINYLTOLUENE  # scripted group (container) (typed FeaturePython)
  Dunit = g/cm3
  Dvalue = 1.032
  Group = -> [C_element077,H_element071]
  conduct = 2
  density = 1
  expand = 3
  formula = G4_PLASTIC_SC_VINYLTOLUENE
  name = G4_PLASTIC_SC_VINYLTOLUENE
  specific = 4
FEATURE [App::DocumentObjectGroupPython] Pu_element001  label="Pu_element : 1"  # scripted group (container) (typed FeaturePython)
  n = 1
  ref = Pu_element
FEATURE [App::DocumentObjectGroupPython] O_element076  label="O_element : 037"  # scripted group (container) (typed FeaturePython)
  n = 2
  ref = O_element
FEATURE [App::DocumentObjectGroupPython] G4_PLUTONIUM_DIOXIDE  # scripted group (container) (typed FeaturePython)
  Dunit = g/cm3
  Dvalue = 11.46
  Group = -> [Pu_element001,O_element076]
  conduct = 2
  density = 1
  expand = 3
  formula = G4_PLUTONIUM_DIOXIDE
  name = G4_PLUTONIUM_DIOXIDE
  specific = 4
FEATURE [App::DocumentObjectGroupPython] C_element078  label="C_element : 037"  # scripted group (container) (typed FeaturePython)
  n = 3
  ref = C_element
FEATURE [App::DocumentObjectGroupPython] H_element072  label="H_element : 034"  # scripted group (container) (typed FeaturePython)
  n = 3
  ref = H_element
FEATURE [App::DocumentObjectGroupPython] N_element036  label="N_element : 015"  # scripted group (container) (typed FeaturePython)
  n = 1
  ref = N_element
FEATURE [App::DocumentObjectGroupPython] G4_POLYACRYLONITRILE  # scripted group (container) (typed FeaturePython)
  Dunit = g/cm3
  Dvalue = 1.17
  Group = -> [C_element078,H_element072,N_element036]
  conduct = 2
  density = 1
  expand = 3
  formula = G4_POLYACRYLONITRILE
  name = G4_POLYACRYLONITRILE
  specific = 4
FEATURE [App::DocumentObjectGroupPython] C_element079  label="C_element : 16"  # scripted group (container) (typed FeaturePython)
  n = 16
  ref = C_element
FEATURE [App::DocumentObjectGroupPython] H_element073  label="H_element : 035"  # scripted group (container) (typed FeaturePython)
  n = 14
  ref = H_element
FEATURE [App::DocumentObjectGroupPython] O_element077  label="O_element : 038"  # scripted group (container) (typed FeaturePython)
  n = 3
  ref = O_element
FEATURE [App::DocumentObjectGroupPython] G4_POLYCARBONATE  # scripted group (container) (typed FeaturePython)
  Dunit = g/cm3
  Dvalue = 1.2
  Group = -> [C_element079,H_element073,O_element077]
  conduct = 2
  density = 1
  expand = 3
  formula = G4_POLYCARBONATE
  name = G4_POLYCARBONATE
  specific = 4
FEATURE [App::DocumentObjectGroupPython] C_element080  label="C_element : 038"  # scripted group (container) (typed FeaturePython)
  n = 8
  ref = C_element
FEATURE [App::DocumentObjectGroupPython] H_element074  label="H_element : 036"  # scripted group (container) (typed FeaturePython)
  n = 7
  ref = H_element
FEATURE [App::DocumentObjectGroupPython] Cl_element017  label="Cl_element : 007"  # scripted group (container) (typed FeaturePython)
  n = 1
  ref = Cl_element
FEATURE [App::DocumentObjectGroupPython] G4_POLYCHLOROSTYRENE  # scripted group (container) (typed FeaturePython)
  Dunit = g/cm3
  Dvalue = 1.3
  Group = -> [C_element080,H_element074,Cl_element017]
  conduct = 2
  density = 1
  expand = 3
  formula = G4_POLYCHLOROSTYRENE
  name = G4_POLYCHLOROSTYRENE
  specific = 4
FEATURE [App::DocumentObjectGroupPython] C_element081  label="C_element : 039"  # scripted group (container) (typed FeaturePython)
  n = 1
  ref = C_element
FEATURE [App::DocumentObjectGroupPython] H_element075  label="H_element : 037"  # scripted group (container) (typed FeaturePython)
  n = 2
  ref = H_element
FEATURE [App::DocumentObjectGroupPython] G4_POLYETHYLENE  # scripted group (container) (typed FeaturePython)
  Dunit = g/cm3
  Dvalue = 0.94
  Group = -> [C_element081,H_element075]
  conduct = 2
  density = 1
  expand = 3
  formula = G4_POLYETHYLENE
  name = G4_POLYETHYLENE
  specific = 4
FEATURE [App::DocumentObjectGroupPython] C_element082  label="C_element : 040"  # scripted group (container) (typed FeaturePython)
  n = 10
  ref = C_element
FEATURE [App::DocumentObjectGroupPython] H_element076  label="H_element : 038"  # scripted group (container) (typed FeaturePython)
  n = 8
  ref = H_element
FEATURE [App::DocumentObjectGroupPython] O_element078  label="O_element : 039"  # scripted group (container) (typed FeaturePython)
  n = 4
  ref = O_element
FEATURE [App::DocumentObjectGroupPython] G4_MYLAR  # scripted group (container) (typed FeaturePython)
  Dunit = g/cm3
  Dvalue = 1.4
  Group = -> [C_element082,H_element076,O_element078]
  conduct = 2
  density = 1
  expand = 3
  formula = G4_MYLAR
  name = G4_MYLAR
  specific = 4
FEATURE [App::DocumentObjectGroupPython] C_element083  label="C_element : 041"  # scripted group (container) (typed FeaturePython)
  n = 5
  ref = C_element
FEATURE [App::DocumentObjectGroupPython] H_element077  label="H_element : 039"  # scripted group (container) (typed FeaturePython)
  n = 8
  ref = H_element
FEATURE [App::DocumentObjectGroupPython] O_element079  label="O_element : 040"  # scripted group (container) (typed FeaturePython)
  n = 2
  ref = O_element
FEATURE [App::DocumentObjectGroupPython] G4_PLEXIGLASS  # scripted group (container) (typed FeaturePython)
  Dunit = g/cm3
  Dvalue = 1.19
  Group = -> [C_element083,H_element077,O_element079]
  conduct = 2
  density = 1
  expand = 3
  formula = G4_PLEXIGLASS
  name = G4_PLEXIGLASS
  specific = 4
FEATURE [App::DocumentObjectGroupPython] C_element084  label="C_element : 042"  # scripted group (container) (typed FeaturePython)
  n = 1
  ref = C_element
FEATURE [App::DocumentObjectGroupPython] H_element078  label="H_element : 040"  # scripted group (container) (typed FeaturePython)
  n = 2
  ref = H_element
FEATURE [App::DocumentObjectGroupPython] O_element080  label="O_element : 041"  # scripted group (container) (typed FeaturePython)
  n = 1
  ref = O_element
FEATURE [App::DocumentObjectGroupPython] G4_POLYOXYMETHYLENE  # scripted group (container) (typed FeaturePython)
  Dunit = g/cm3
  Dvalue = 1.425
  Group = -> [C_element084,H_element078,O_element080]
  conduct = 2
  density = 1
  expand = 3
  formula = G4_POLYOXYMETHYLENE
  name = G4_POLYOXYMETHYLENE
  specific = 4
FEATURE [App::DocumentObjectGroupPython] C_element085  label="C_element : 043"  # scripted group (container) (typed FeaturePython)
  n = 2
  ref = C_element
FEATURE [App::DocumentObjectGroupPython] H_element079  label="H_element : 041"  # scripted group (container) (typed FeaturePython)
  n = 4
  ref = H_element
FEATURE [App::DocumentObjectGroupPython] G4_POLYPROPYLENE  # scripted group (container) (typed FeaturePython)
  Dunit = g/cm3
  Dvalue = 0.9
  Group = -> [C_element085,H_element079]
  conduct = 2
  density = 1
  expand = 3
  formula = G4_POLYPROPYLENE
  name = G4_POLYPROPYLENE
  specific = 4
FEATURE [App::DocumentObjectGroupPython] C_element086  label="C_element : 044"  # scripted group (container) (typed FeaturePython)
  n = 8
  ref = C_element
FEATURE [App::DocumentObjectGroupPython] H_element080  label="H_element : 042"  # scripted group (container) (typed FeaturePython)
  n = 8
  ref = H_element
FEATURE [App::DocumentObjectGroupPython] G4_POLYSTYRENE  # scripted group (container) (typed FeaturePython)
  Dunit = g/cm3
  Dvalue = 1.06
  Group = -> [C_element086,H_element080]
  conduct = 2
  density = 1
  expand = 3
  formula = G4_POLYSTYRENE
  name = G4_POLYSTYRENE
  specific = 4
FEATURE [App::DocumentObjectGroupPython] C_element087  label="C_element : 045"  # scripted group (container) (typed FeaturePython)
  n = 2
  ref = C_element
FEATURE [App::DocumentObjectGroupPython] F_element014  label="F_element : 4"  # scripted group (container) (typed FeaturePython)
  n = 4
  ref = F_element
FEATURE [App::DocumentObjectGroupPython] G4_TEFLON  # scripted group (container) (typed FeaturePython)
  Dunit = g/cm3
  Dvalue = 2.2
  Group = -> [C_element087,F_element014]
  conduct = 2
  density = 1
  expand = 3
  formula = G4_TEFLON
  name = G4_TEFLON
  specific = 4
FEATURE [App::DocumentObjectGroupPython] C_element088  label="C_element : 046"  # scripted group (container) (typed FeaturePython)
  n = 2
  ref = C_element
FEATURE [App::DocumentObjectGroupPython] F_element015  label="F_element : 006"  # scripted group (container) (typed FeaturePython)
  n = 3
  ref = F_element
FEATURE [App::DocumentObjectGroupPython] Cl_element018  label="Cl_element : 008"  # scripted group (container) (typed FeaturePython)
  n = 1
  ref = Cl_element
FEATURE [App::DocumentObjectGroupPython] G4_POLYTRIFLUOROCHLOROETHYLENE  # scripted group (container) (typed FeaturePython)
  Dunit = g/cm3
  Dvalue = 2.1
  Group = -> [C_element088,F_element015,Cl_element018]
  conduct = 2
  density = 1
  expand = 3
  formula = G4_POLYTRIFLUOROCHLOROETHYLENE
  name = G4_POLYTRIFLUOROCHLOROETHYLENE
  specific = 4
FEATURE [App::DocumentObjectGroupPython] C_element089  label="C_element : 047"  # scripted group (container) (typed FeaturePython)
  n = 4
  ref = C_element
FEATURE [App::DocumentObjectGroupPython] H_element081  label="H_element : 043"  # scripted group (container) (typed FeaturePython)
  n = 6
  ref = H_element
FEATURE [App::DocumentObjectGroupPython] O_element081  label="O_element : 042"  # scripted group (container) (typed FeaturePython)
  n = 2
  ref = O_element
FEATURE [App::DocumentObjectGroupPython] G4_POLYVINYL_ACETATE  # scripted group (container) (typed FeaturePython)
  Dunit = g/cm3
  Dvalue = 1.19
  Group = -> [C_element089,H_element081,O_element081]
  conduct = 2
  density = 1
  expand = 3
  formula = G4_POLYVINYL_ACETATE
  name = G4_POLYVINYL_ACETATE
  specific = 4
FEATURE [App::DocumentObjectGroupPython] C_element090  label="C_element : 048"  # scripted group (container) (typed FeaturePython)
  n = 2
  ref = C_element
FEATURE [App::DocumentObjectGroupPython] H_element082  label="H_element : 044"  # scripted group (container) (typed FeaturePython)
  n = 4
  ref = H_element
FEATURE [App::DocumentObjectGroupPython] O_element082  label="O_element : 043"  # scripted group (container) (typed FeaturePython)
  n = 1
  ref = O_element
FEATURE [App::DocumentObjectGroupPython] G4_POLYVINYL_ALCOHOL  # scripted group (container) (typed FeaturePython)
  Dunit = g/cm3
  Dvalue = 1.3
  Group = -> [C_element090,H_element082,O_element082]
  conduct = 2
  density = 1
  expand = 3
  formula = G4_POLYVINYL_ALCOHOL
  name = G4_POLYVINYL_ALCOHOL
  specific = 4
FEATURE [App::DocumentObjectGroupPython] C_element091  label="C_element : 049"  # scripted group (container) (typed FeaturePython)
  n = 8
  ref = C_element
FEATURE [App::DocumentObjectGroupPython] H_element083  label="H_element : 045"  # scripted group (container) (typed FeaturePython)
  n = 14
  ref = H_element
FEATURE [App::DocumentObjectGroupPython] O_element083  label="O_element : 044"  # scripted group (container) (typed FeaturePython)
  n = 2
  ref = O_element
FEATURE [App::DocumentObjectGroupPython] G4_POLYVINYL_BUTYRAL  # scripted group (container) (typed FeaturePython)
  Dunit = g/cm3
  Dvalue = 1.12
  Group = -> [C_element091,H_element083,O_element083]
  conduct = 2
  density = 1
  expand = 3
  formula = G4_POLYVINYL_BUTYRAL
  name = G4_POLYVINYL_BUTYRAL
  specific = 4
FEATURE [App::DocumentObjectGroupPython] C_element092  label="C_element : 050"  # scripted group (container) (typed FeaturePython)
  n = 2
  ref = C_element
FEATURE [App::DocumentObjectGroupPython] H_element084  label="H_element : 046"  # scripted group (container) (typed FeaturePython)
  n = 3
  ref = H_element
FEATURE [App::DocumentObjectGroupPython] Cl_element019  label="Cl_element : 009"  # scripted group (container) (typed FeaturePython)
  n = 1
  ref = Cl_element
FEATURE [App::DocumentObjectGroupPython] G4_POLYVINYL_CHLORIDE  # scripted group (container) (typed FeaturePython)
  Dunit = g/cm3
  Dvalue = 1.3
  Group = -> [C_element092,H_element084,Cl_element019]
  conduct = 2
  density = 1
  expand = 3
  formula = G4_POLYVINYL_CHLORIDE
  name = G4_POLYVINYL_CHLORIDE
  specific = 4
FEATURE [App::DocumentObjectGroupPython] C_element093  label="C_element : 051"  # scripted group (container) (typed FeaturePython)
  n = 2
  ref = C_element
FEATURE [App::DocumentObjectGroupPython] H_element085  label="H_element : 047"  # scripted group (container) (typed FeaturePython)
  n = 2
  ref = H_element
FEATURE [App::DocumentObjectGroupPython] Cl_element020  label="Cl_element : 010"  # scripted group (container) (typed FeaturePython)
  n = 2
  ref = Cl_element
FEATURE [App::DocumentObjectGroupPython] G4_POLYVINYLIDENE_CHLORIDE  # scripted group (container) (typed FeaturePython)
  Dunit = g/cm3
  Dvalue = 1.7
  Group = -> [C_element093,H_element085,Cl_element020]
  conduct = 2
  density = 1
  expand = 3
  formula = G4_POLYVINYLIDENE_CHLORIDE
  name = G4_POLYVINYLIDENE_CHLORIDE
  specific = 4
FEATURE [App::DocumentObjectGroupPython] C_element094  label="C_element : 052"  # scripted group (container) (typed FeaturePython)
  n = 2
  ref = C_element
FEATURE [App::DocumentObjectGroupPython] H_element086  label="H_element : 048"  # scripted group (container) (typed FeaturePython)
  n = 2
  ref = H_element
FEATURE [App::DocumentObjectGroupPython] F_element016  label="F_element : 007"  # scripted group (container) (typed FeaturePython)
  n = 2
  ref = F_element
FEATURE [App::DocumentObjectGroupPython] G4_POLYVINYLIDENE_FLUORIDE  # scripted group (container) (typed FeaturePython)
  Dunit = g/cm3
  Dvalue = 1.76
  Group = -> [C_element094,H_element086,F_element016]
  conduct = 2
  density = 1
  expand = 3
  formula = G4_POLYVINYLIDENE_FLUORIDE
  name = G4_POLYVINYLIDENE_FLUORIDE
  specific = 4
FEATURE [App::DocumentObjectGroupPython] C_element095  label="C_element : 053"  # scripted group (container) (typed FeaturePython)
  n = 6
  ref = C_element
FEATURE [App::DocumentObjectGroupPython] H_element087  label="H_element : 9"  # scripted group (container) (typed FeaturePython)
  n = 9
  ref = H_element
FEATURE [App::DocumentObjectGroupPython] N_element037  label="N_element : 016"  # scripted group (container) (typed FeaturePython)
  n = 1
  ref = N_element
FEATURE [App::DocumentObjectGroupPython] O_element084  label="O_element : 045"  # scripted group (container) (typed FeaturePython)
  n = 1
  ref = O_element
FEATURE [App::DocumentObjectGroupPython] G4_POLYVINYL_PYRROLIDONE  # scripted group (container) (typed FeaturePython)
  Dunit = g/cm3
  Dvalue = 1.25
  Group = -> [C_element095,H_element087,N_element037,O_element084]
  conduct = 2
  density = 1
  expand = 3
  formula = G4_POLYVINYL_PYRROLIDONE
  name = G4_POLYVINYL_PYRROLIDONE
  specific = 4
FEATURE [App::DocumentObjectGroupPython] K_element008  label="K_element : 1"  # scripted group (container) (typed FeaturePython)
  n = 1
  ref = K_element
FEATURE [App::DocumentObjectGroupPython] I_element006  label="I_element : 003"  # scripted group (container) (typed FeaturePython)
  n = 1
  ref = I_element
FEATURE [App::DocumentObjectGroupPython] G4_POTASSIUM_IODIDE  # scripted group (container) (typed FeaturePython)
  Dunit = g/cm3
  Dvalue = 3.13
  Group = -> [K_element008,I_element006]
  conduct = 2
  density = 1
  expand = 3
  formula = G4_POTASSIUM_IODIDE
  name = G4_POTASSIUM_IODIDE
  specific = 4
FEATURE [App::DocumentObjectGroupPython] K_element009  label="K_element : 2"  # scripted group (container) (typed FeaturePython)
  n = 2
  ref = K_element
FEATURE [App::DocumentObjectGroupPython] O_element085  label="O_element : 046"  # scripted group (container) (typed FeaturePython)
  n = 1
  ref = O_element
FEATURE [App::DocumentObjectGroupPython] G4_POTASSIUM_OXIDE  # scripted group (container) (typed FeaturePython)
  Dunit = g/cm3
  Dvalue = 2.32
  Group = -> [K_element009,O_element085]
  conduct = 2
  density = 1
  expand = 3
  formula = G4_POTASSIUM_OXIDE
  name = G4_POTASSIUM_OXIDE
  specific = 4
FEATURE [App::DocumentObjectGroupPython] C_element096  label="C_element : 054"  # scripted group (container) (typed FeaturePython)
  n = 3
  ref = C_element
FEATURE [App::DocumentObjectGroupPython] H_element088  label="H_element : 049"  # scripted group (container) (typed FeaturePython)
  n = 8
  ref = H_element
FEATURE [App::DocumentObjectGroupPython] G4_PROPANE  # scripted group (container) (typed FeaturePython)
  Dunit = g/cm3
  Dvalue = 0.00187939
  Group = -> [C_element096,H_element088]
  conduct = 2
  density = 1
  expand = 3
  formula = G4_PROPANE
  name = G4_PROPANE
  specific = 4
FEATURE [App::DocumentObjectGroupPython] C_element097  label="C_element : 055"  # scripted group (container) (typed FeaturePython)
  n = 3
  ref = C_element
FEATURE [App::DocumentObjectGroupPython] H_element089  label="H_element : 050"  # scripted group (container) (typed FeaturePython)
  n = 8
  ref = H_element
FEATURE [App::DocumentObjectGroupPython] G4_lPROPANE  # scripted group (container) (typed FeaturePython)
  Dunit = g/cm3
  Dvalue = 0.43
  Group = -> [C_element097,H_element089]
  conduct = 2
  density = 1
  expand = 3
  formula = G4_lPROPANE
  name = G4_lPROPANE
  specific = 4
FEATURE [App::DocumentObjectGroupPython] C_element098  label="C_element : 056"  # scripted group (container) (typed FeaturePython)
  n = 3
  ref = C_element
FEATURE [App::DocumentObjectGroupPython] H_element090  label="H_element : 051"  # scripted group (container) (typed FeaturePython)
  n = 8
  ref = H_element
FEATURE [App::DocumentObjectGroupPython] O_element086  label="O_element : 047"  # scripted group (container) (typed FeaturePython)
  n = 1
  ref = O_element
FEATURE [App::DocumentObjectGroupPython] G4_N_PROPYL_ALCOHOL  label="G4_N-PROPYL_ALCOHOL"  # scripted group (container) (typed FeaturePython)
  Dunit = g/cm3
  Dvalue = 0.8035
  Group = -> [C_element098,H_element090,O_element086]
  conduct = 2
  density = 1
  expand = 3
  formula = G4_N-PROPYL_ALCOHOL
  name = G4_N-PROPYL_ALCOHOL
  specific = 4
FEATURE [App::DocumentObjectGroupPython] C_element099  label="C_element : 057"  # scripted group (container) (typed FeaturePython)
  n = 5
  ref = C_element
FEATURE [App::DocumentObjectGroupPython] H_element091  label="H_element : 052"  # scripted group (container) (typed FeaturePython)
  n = 5
  ref = H_element
FEATURE [App::DocumentObjectGroupPython] N_element038  label="N_element : 017"  # scripted group (container) (typed FeaturePython)
  n = 1
  ref = N_element
FEATURE [App::DocumentObjectGroupPython] G4_PYRIDINE  # scripted group (container) (typed FeaturePython)
  Dunit = g/cm3
  Dvalue = 0.9819
  Group = -> [C_element099,H_element091,N_element038]
  conduct = 2
  density = 1
  expand = 3
  formula = G4_PYRIDINE
  name = G4_PYRIDINE
  specific = 4
FEATURE [App::DocumentObjectGroupPython] H_element092  label="H_element : 0.144"  # scripted group (container) (typed FeaturePython)
  n = 0.143711
FEATURE [App::DocumentObjectGroupPython] C_element100  label="C_element : 0.856"  # scripted group (container) (typed FeaturePython)
  n = 0.856289
FEATURE [App::DocumentObjectGroupPython] G4_RUBBER_BUTYL  # scripted group (container) (typed FeaturePython)
  Dunit = g/cm3
  Dvalue = 0.92
  Group = -> [H_element092,C_element100]
  conduct = 2
  density = 1
  expand = 3
  formula = G4_RUBBER_BUTYL
  name = G4_RUBBER_BUTYL
  specific = 4
FEATURE [App::DocumentObjectGroupPython] H_element093  label="H_element : 0.118"  # scripted group (container) (typed FeaturePython)
  n = 0.118371
FEATURE [App::DocumentObjectGroupPython] C_element101  label="C_element : 0.882"  # scripted group (container) (typed FeaturePython)
  n = 0.881629
FEATURE [App::DocumentObjectGroupPython] G4_RUBBER_NATURAL  # scripted group (container) (typed FeaturePython)
  Dunit = g/cm3
  Dvalue = 0.92
  Group = -> [H_element093,C_element101]
  conduct = 2
  density = 1
  expand = 3
  formula = G4_RUBBER_NATURAL
  name = G4_RUBBER_NATURAL
  specific = 4
FEATURE [App::DocumentObjectGroupPython] H_element094  label="H_element : 0.145"  # scripted group (container) (typed FeaturePython)
  n = 0.05692
FEATURE [App::DocumentObjectGroupPython] C_element102  label="C_element : 0.543"  # scripted group (container) (typed FeaturePython)
  n = 0.542646
FEATURE [App::DocumentObjectGroupPython] Cl_element021  label="Cl_element : 0.400"  # scripted group (container) (typed FeaturePython)
  n = 0.400434
FEATURE [App::DocumentObjectGroupPython] G4_RUBBER_NEOPRENE  # scripted group (container) (typed FeaturePython)
  Dunit = g/cm3
  Dvalue = 1.23
  Group = -> [H_element094,C_element102,Cl_element021]
  conduct = 2
  density = 1
  expand = 3
  formula = G4_RUBBER_NEOPRENE
  name = G4_RUBBER_NEOPRENE
  specific = 4
FEATURE [App::DocumentObjectGroupPython] Si_element006  label="Si_element : 1"  # scripted group (container) (typed FeaturePython)
  n = 1
  ref = Si_element
FEATURE [App::DocumentObjectGroupPython] O_element087  label="O_element : 048"  # scripted group (container) (typed FeaturePython)
  n = 2
  ref = O_element
FEATURE [App::DocumentObjectGroupPython] G4_SILICON_DIOXIDE  # scripted group (container) (typed FeaturePython)
  Dunit = g/cm3
  Dvalue = 2.32
  Group = -> [Si_element006,O_element087]
  conduct = 2
  density = 1
  expand = 3
  formula = G4_SILICON_DIOXIDE
  name = G4_SILICON_DIOXIDE
  specific = 4
FEATURE [App::DocumentObjectGroupPython] Ag_element002  label="Ag_element : 1"  # scripted group (container) (typed FeaturePython)
  n = 1
  ref = Ag_element
FEATURE [App::DocumentObjectGroupPython] Br_element005  label="Br_element : 003"  # scripted group (container) (typed FeaturePython)
  n = 1
  ref = Br_element
FEATURE [App::DocumentObjectGroupPython] G4_SILVER_BROMIDE  # scripted group (container) (typed FeaturePython)
  Dunit = g/cm3
  Dvalue = 6.473
  Group = -> [Ag_element002,Br_element005]
  conduct = 2
  density = 1
  expand = 3
  formula = G4_SILVER_BROMIDE
  name = G4_SILVER_BROMIDE
  specific = 4
FEATURE [App::DocumentObjectGroupPython] Ag_element003  label="Ag_element : 002"  # scripted group (container) (typed FeaturePython)
  n = 1
  ref = Ag_element
FEATURE [App::DocumentObjectGroupPython] Cl_element022  label="Cl_element : 011"  # scripted group (container) (typed FeaturePython)
  n = 1
  ref = Cl_element
FEATURE [App::DocumentObjectGroupPython] G4_SILVER_CHLORIDE  # scripted group (container) (typed FeaturePython)
  Dunit = g/cm3
  Dvalue = 5.56
  Group = -> [Ag_element003,Cl_element022]
  conduct = 2
  density = 1
  expand = 3
  formula = G4_SILVER_CHLORIDE
  name = G4_SILVER_CHLORIDE
  specific = 4
FEATURE [App::DocumentObjectGroupPython] Br_element006  label="Br_element : 0.423"  # scripted group (container) (typed FeaturePython)
  n = 0.422895
FEATURE [App::DocumentObjectGroupPython] Ag_element004  label="Ag_element : 0.574"  # scripted group (container) (typed FeaturePython)
  n = 0.573748
FEATURE [App::DocumentObjectGroupPython] I_element007  label="I_element : 0.649"  # scripted group (container) (typed FeaturePython)
  n = 0.003357
FEATURE [App::DocumentObjectGroupPython] G4_SILVER_HALIDES  # scripted group (container) (typed FeaturePython)
  Dunit = g/cm3
  Dvalue = 6.47
  Group = -> [Br_element006,Ag_element004,I_element007]
  conduct = 2
  density = 1
  expand = 3
  formula = G4_SILVER_HALIDES
  name = G4_SILVER_HALIDES
  specific = 4
FEATURE [App::DocumentObjectGroupPython] Ag_element005  label="Ag_element : 003"  # scripted group (container) (typed FeaturePython)
  n = 1
  ref = Ag_element
FEATURE [App::DocumentObjectGroupPython] I_element008  label="I_element : 004"  # scripted group (container) (typed FeaturePython)
  n = 1
  ref = I_element
FEATURE [App::DocumentObjectGroupPython] G4_SILVER_IODIDE  # scripted group (container) (typed FeaturePython)
  Dunit = g/cm3
  Dvalue = 6.01
  Group = -> [Ag_element005,I_element008]
  conduct = 2
  density = 1
  expand = 3
  formula = G4_SILVER_IODIDE
  name = G4_SILVER_IODIDE
  specific = 4
FEATURE [App::DocumentObjectGroupPython] H_element095  label="H_element : 0.100"  # scripted group (container) (typed FeaturePython)
  n = 0.1
FEATURE [App::DocumentObjectGroupPython] C_element103  label="C_element : 0.204"  # scripted group (container) (typed FeaturePython)
  n = 0.204
FEATURE [App::DocumentObjectGroupPython] N_element039  label="N_element : 0.759"  # scripted group (container) (typed FeaturePython)
  n = 0.042
FEATURE [App::DocumentObjectGroupPython] O_element088  label="O_element : 0.645"  # scripted group (container) (typed FeaturePython)
  n = 0.645
FEATURE [App::DocumentObjectGroupPython] Na_element013  label="Na_element : 0.100"  # scripted group (container) (typed FeaturePython)
  n = 0.002
FEATURE [App::DocumentObjectGroupPython] P_element009  label="P_element : 0.107"  # scripted group (container) (typed FeaturePython)
  n = 0.001
FEATURE [App::DocumentObjectGroupPython] S_element020  label="S_element : 0.021"  # scripted group (container) (typed FeaturePython)
  n = 0.002
FEATURE [App::DocumentObjectGroupPython] Cl_element023  label="Cl_element : 0.590"  # scripted group (container) (typed FeaturePython)
  n = 0.003
FEATURE [App::DocumentObjectGroupPython] K_element010  label="K_element : 0.001"  # scripted group (container) (typed FeaturePython)
  n = 0.001
FEATURE [App::DocumentObjectGroupPython] G4_SKIN_ICRP  # scripted group (container) (typed FeaturePython)
  Dunit = g/cm3
  Dvalue = 1.09
  Group = -> [H_element095,C_element103,N_element039,O_element088,Na_element013,P_element009,S_element020,Cl_element023,K_element010]
  conduct = 2
  density = 1
  expand = 3
  formula = G4_SKIN_ICRP
  name = G4_SKIN_ICRP
  specific = 4
FEATURE [App::DocumentObjectGroupPython] Na_element014  label="Na_element : 2"  # scripted group (container) (typed FeaturePython)
  n = 2
  ref = Na_element
FEATURE [App::DocumentObjectGroupPython] C_element104  label="C_element : 058"  # scripted group (container) (typed FeaturePython)
  n = 1
  ref = C_element
FEATURE [App::DocumentObjectGroupPython] O_element089  label="O_element : 049"  # scripted group (container) (typed FeaturePython)
  n = 3
  ref = O_element
FEATURE [App::DocumentObjectGroupPython] G4_SODIUM_CARBONATE  # scripted group (container) (typed FeaturePython)
  Dunit = g/cm3
  Dvalue = 2.532
  Group = -> [Na_element014,C_element104,O_element089]
  conduct = 2
  density = 1
  expand = 3
  formula = G4_SODIUM_CARBONATE
  name = G4_SODIUM_CARBONATE
  specific = 4
FEATURE [App::DocumentObjectGroupPython] Na_element015  label="Na_element : 1"  # scripted group (container) (typed FeaturePython)
  n = 1
  ref = Na_element
FEATURE [App::DocumentObjectGroupPython] I_element009  label="I_element : 005"  # scripted group (container) (typed FeaturePython)
  n = 1
  ref = I_element
FEATURE [App::DocumentObjectGroupPython] G4_SODIUM_IODIDE  # scripted group (container) (typed FeaturePython)
  Dunit = g/cm3
  Dvalue = 3.667
  Group = -> [Na_element015,I_element009]
  conduct = 2
  density = 1
  expand = 3
  formula = G4_SODIUM_IODIDE
  name = G4_SODIUM_IODIDE
  specific = 4
FEATURE [App::DocumentObjectGroupPython] Na_element016  label="Na_element : 003"  # scripted group (container) (typed FeaturePython)
  n = 2
  ref = Na_element
FEATURE [App::DocumentObjectGroupPython] O_element090  label="O_element : 050"  # scripted group (container) (typed FeaturePython)
  n = 1
  ref = O_element
FEATURE [App::DocumentObjectGroupPython] G4_SODIUM_MONOXIDE  # scripted group (container) (typed FeaturePython)
  Dunit = g/cm3
  Dvalue = 2.27
  Group = -> [Na_element016,O_element090]
  conduct = 2
  density = 1
  expand = 3
  formula = G4_SODIUM_MONOXIDE
  name = G4_SODIUM_MONOXIDE
  specific = 4
FEATURE [App::DocumentObjectGroupPython] Na_element017  label="Na_element : 004"  # scripted group (container) (typed FeaturePython)
  n = 1
  ref = Na_element
FEATURE [App::DocumentObjectGroupPython] N_element040  label="N_element : 018"  # scripted group (container) (typed FeaturePython)
  n = 1
  ref = N_element
FEATURE [App::DocumentObjectGroupPython] O_element091  label="O_element : 051"  # scripted group (container) (typed FeaturePython)
  n = 3
  ref = O_element
FEATURE [App::DocumentObjectGroupPython] G4_SODIUM_NITRATE  # scripted group (container) (typed FeaturePython)
  Dunit = g/cm3
  Dvalue = 2.261
  Group = -> [Na_element017,N_element040,O_element091]
  conduct = 2
  density = 1
  expand = 3
  formula = G4_SODIUM_NITRATE
  name = G4_SODIUM_NITRATE
  specific = 4
FEATURE [App::DocumentObjectGroupPython] C_element105  label="C_element : 059"  # scripted group (container) (typed FeaturePython)
  n = 14
  ref = C_element
FEATURE [App::DocumentObjectGroupPython] H_element096  label="H_element : 053"  # scripted group (container) (typed FeaturePython)
  n = 12
  ref = H_element
FEATURE [App::DocumentObjectGroupPython] G4_STILBENE  # scripted group (container) (typed FeaturePython)
  Dunit = g/cm3
  Dvalue = 0.9707
  Group = -> [C_element105,H_element096]
  conduct = 2
  density = 1
  expand = 3
  formula = G4_STILBENE
  name = G4_STILBENE
  specific = 4
FEATURE [App::DocumentObjectGroupPython] C_element106  label="C_element : 12"  # scripted group (container) (typed FeaturePython)
  n = 12
  ref = C_element
FEATURE [App::DocumentObjectGroupPython] H_element097  label="H_element : 22"  # scripted group (container) (typed FeaturePython)
  n = 22
  ref = H_element
FEATURE [App::DocumentObjectGroupPython] O_element092  label="O_element : 11"  # scripted group (container) (typed FeaturePython)
  n = 11
  ref = O_element
FEATURE [App::DocumentObjectGroupPython] G4_SUCROSE  # scripted group (container) (typed FeaturePython)
  Dunit = g/cm3
  Dvalue = 1.5805
  Group = -> [C_element106,H_element097,O_element092]
  conduct = 2
  density = 1
  expand = 3
  formula = G4_SUCROSE
  name = G4_SUCROSE
  specific = 4
FEATURE [App::DocumentObjectGroupPython] C_element107  label="C_element : 18"  # scripted group (container) (typed FeaturePython)
  n = 18
  ref = C_element
FEATURE [App::DocumentObjectGroupPython] H_element098  label="H_element : 054"  # scripted group (container) (typed FeaturePython)
  n = 14
  ref = H_element
FEATURE [App::DocumentObjectGroupPython] G4_TERPHENYL  # scripted group (container) (typed FeaturePython)
  Dunit = g/cm3
  Dvalue = 1.24
  Group = -> [C_element107,H_element098]
  conduct = 2
  density = 1
  expand = 3
  formula = G4_TERPHENYL
  name = G4_TERPHENYL
  specific = 4
FEATURE [App::DocumentObjectGroupPython] H_element099  label="H_element : 0.146"  # scripted group (container) (typed FeaturePython)
  n = 0.106
FEATURE [App::DocumentObjectGroupPython] C_element108  label="C_element : 0.883"  # scripted group (container) (typed FeaturePython)
  n = 0.099
FEATURE [App::DocumentObjectGroupPython] N_element041  label="N_element : 0.020"  # scripted group (container) (typed FeaturePython)
  n = 0.02
FEATURE [App::DocumentObjectGroupPython] O_element093  label="O_element : 0.766"  # scripted group (container) (typed FeaturePython)
  n = 0.766
FEATURE [App::DocumentObjectGroupPython] Na_element018  label="Na_element : 0.101"  # scripted group (container) (typed FeaturePython)
  n = 0.002
FEATURE [App::DocumentObjectGroupPython] P_element010  label="P_element : 0.108"  # scripted group (container) (typed FeaturePython)
  n = 0.001
FEATURE [App::DocumentObjectGroupPython] S_element021  label="S_element : 0.022"  # scripted group (container) (typed FeaturePython)
  n = 0.002
FEATURE [App::DocumentObjectGroupPython] Cl_element024  label="Cl_element : 0.002"  # scripted group (container) (typed FeaturePython)
  n = 0.002
FEATURE [App::DocumentObjectGroupPython] K_element011  label="K_element : 0.017"  # scripted group (container) (typed FeaturePython)
  n = 0.002
FEATURE [App::DocumentObjectGroupPython] G4_TESTIS_ICRP  # scripted group (container) (typed FeaturePython)
  Dunit = g/cm3
  Dvalue = 1.04
  Group = -> [H_element099,C_element108,N_element041,O_element093,Na_element018,P_element010,S_element021,Cl_element024,K_element011]
  conduct = 2
  density = 1
  expand = 3
  formula = G4_TESTIS_ICRP
  name = G4_TESTIS_ICRP
  specific = 4
FEATURE [App::DocumentObjectGroupPython] C_element109  label="C_element : 060"  # scripted group (container) (typed FeaturePython)
  n = 2
  ref = C_element
FEATURE [App::DocumentObjectGroupPython] Cl_element025  label="Cl_element : 012"  # scripted group (container) (typed FeaturePython)
  n = 4
  ref = Cl_element
FEATURE [App::DocumentObjectGroupPython] G4_TETRACHLOROETHYLENE  # scripted group (container) (typed FeaturePython)
  Dunit = g/cm3
  Dvalue = 1.625
  Group = -> [C_element109,Cl_element025]
  conduct = 2
  density = 1
  expand = 3
  formula = G4_TETRACHLOROETHYLENE
  name = G4_TETRACHLOROETHYLENE
  specific = 4
FEATURE [App::DocumentObjectGroupPython] Tl_element001  label="Tl_element : 1"  # scripted group (container) (typed FeaturePython)
  n = 1
  ref = Tl_element
FEATURE [App::DocumentObjectGroupPython] Cl_element026  label="Cl_element : 013"  # scripted group (container) (typed FeaturePython)
  n = 1
  ref = Cl_element
FEATURE [App::DocumentObjectGroupPython] G4_THALLIUM_CHLORIDE  # scripted group (container) (typed FeaturePython)
  Dunit = g/cm3
  Dvalue = 7.004
  Group = -> [Tl_element001,Cl_element026]
  conduct = 2
  density = 1
  expand = 3
  formula = G4_THALLIUM_CHLORIDE
  name = G4_THALLIUM_CHLORIDE
  specific = 4
FEATURE [App::DocumentObjectGroupPython] H_element100  label="H_element : 0.147"  # scripted group (container) (typed FeaturePython)
  n = 0.105
FEATURE [App::DocumentObjectGroupPython] C_element110  label="C_element : 0.256"  # scripted group (container) (typed FeaturePython)
  n = 0.256
FEATURE [App::DocumentObjectGroupPython] N_element042  label="N_element : 0.760"  # scripted group (container) (typed FeaturePython)
  n = 0.027
FEATURE [App::DocumentObjectGroupPython] O_element094  label="O_element : 0.602"  # scripted group (container) (typed FeaturePython)
  n = 0.602
FEATURE [App::DocumentObjectGroupPython] Na_element019  label="Na_element : 0.102"  # scripted group (container) (typed FeaturePython)
  n = 0.001
FEATURE [App::DocumentObjectGroupPython] P_element011  label="P_element : 0.109"  # scripted group (container) (typed FeaturePython)
  n = 0.002
FEATURE [App::DocumentObjectGroupPython] S_element022  label="S_element : 0.023"  # scripted group (container) (typed FeaturePython)
  n = 0.003
FEATURE [App::DocumentObjectGroupPython] Cl_element027  label="Cl_element : 0.591"  # scripted group (container) (typed FeaturePython)
  n = 0.002
FEATURE [App::DocumentObjectGroupPython] K_element012  label="K_element : 0.018"  # scripted group (container) (typed FeaturePython)
  n = 0.002
FEATURE [App::DocumentObjectGroupPython] G4_TISSUE_SOFT_ICRP  # scripted group (container) (typed FeaturePython)
  Dunit = g/cm3
  Dvalue = 1.03
  Group = -> [H_element100,C_element110,N_element042,O_element094,Na_element019,P_element011,S_element022,Cl_element027,K_element012]
  conduct = 2
  density = 1
  expand = 3
  formula = G4_TISSUE_SOFT_ICRP
  name = G4_TISSUE_SOFT_ICRP
  specific = 4
FEATURE [App::DocumentObjectGroupPython] H_element101  label="H_element : 0.148"  # scripted group (container) (typed FeaturePython)
  n = 0.101
FEATURE [App::DocumentObjectGroupPython] C_element111  label="C_element : 0.111"  # scripted group (container) (typed FeaturePython)
  n = 0.111
FEATURE [App::DocumentObjectGroupPython] N_element043  label="N_element : 0.026"  # scripted group (container) (typed FeaturePython)
  n = 0.026
FEATURE [App::DocumentObjectGroupPython] O_element095  label="O_element : 0.762"  # scripted group (container) (typed FeaturePython)
  n = 0.762
FEATURE [App::DocumentObjectGroupPython] G4_TISSUE_SOFT_ICRU_4  label="G4_TISSUE_SOFT_ICRU-4"  # scripted group (container) (typed FeaturePython)
  Dunit = g/cm3
  Dvalue = 1
  Group = -> [H_element101,C_element111,N_element043,O_element095]
  conduct = 2
  density = 1
  expand = 3
  formula = G4_TISSUE_SOFT_ICRU-4
  name = G4_TISSUE_SOFT_ICRU-4
  specific = 4
FEATURE [App::DocumentObjectGroupPython] H_element102  label="H_element : 0.149"  # scripted group (container) (typed FeaturePython)
  n = 0.101869
FEATURE [App::DocumentObjectGroupPython] C_element112  label="C_element : 0.456"  # scripted group (container) (typed FeaturePython)
  n = 0.456179
FEATURE [App::DocumentObjectGroupPython] N_element044  label="N_element : 0.761"  # scripted group (container) (typed FeaturePython)
  n = 0.035172
FEATURE [App::DocumentObjectGroupPython] O_element096  label="O_element : 0.407"  # scripted group (container) (typed FeaturePython)
  n = 0.40678
FEATURE [App::DocumentObjectGroupPython] G4_TISSUE_METHANE  label="G4_TISSUE-METHANE"  # scripted group (container) (typed FeaturePython)
  Dunit = g/cm3
  Dvalue = 0.00106409
  Group = -> [H_element102,C_element112,N_element044,O_element096]
  conduct = 2
  density = 1
  expand = 3
  formula = G4_TISSUE-METHANE
  name = G4_TISSUE-METHANE
  specific = 4
FEATURE [App::DocumentObjectGroupPython] H_element103  label="H_element : 0.103"  # scripted group (container) (typed FeaturePython)
  n = 0.102672
FEATURE [App::DocumentObjectGroupPython] C_element113  label="C_element : 0.569"  # scripted group (container) (typed FeaturePython)
  n = 0.56894
FEATURE [App::DocumentObjectGroupPython] N_element045  label="N_element : 0.762"  # scripted group (container) (typed FeaturePython)
  n = 0.035022
FEATURE [App::DocumentObjectGroupPython] O_element097  label="O_element : 0.293"  # scripted group (container) (typed FeaturePython)
  n = 0.293366
FEATURE [App::DocumentObjectGroupPython] G4_TISSUE_PROPANE  label="G4_TISSUE-PROPANE"  # scripted group (container) (typed FeaturePython)
  Dunit = g/cm3
  Dvalue = 0.00182628
  Group = -> [H_element103,C_element113,N_element045,O_element097]
  conduct = 2
  density = 1
  expand = 3
  formula = G4_TISSUE-PROPANE
  name = G4_TISSUE-PROPANE
  specific = 4
FEATURE [App::DocumentObjectGroupPython] Ti_element003  label="Ti_element : 1"  # scripted group (container) (typed FeaturePython)
  n = 1
  ref = Ti_element
FEATURE [App::DocumentObjectGroupPython] O_element098  label="O_element : 052"  # scripted group (container) (typed FeaturePython)
  n = 2
  ref = O_element
FEATURE [App::DocumentObjectGroupPython] G4_TITANIUM_DIOXIDE  # scripted group (container) (typed FeaturePython)
  Dunit = g/cm3
  Dvalue = 4.26
  Group = -> [Ti_element003,O_element098]
  conduct = 2
  density = 1
  expand = 3
  formula = G4_TITANIUM_DIOXIDE
  name = G4_TITANIUM_DIOXIDE
  specific = 4
FEATURE [App::DocumentObjectGroupPython] C_element114  label="C_element : 061"  # scripted group (container) (typed FeaturePython)
  n = 7
  ref = C_element
FEATURE [App::DocumentObjectGroupPython] H_element104  label="H_element : 055"  # scripted group (container) (typed FeaturePython)
  n = 8
  ref = H_element
FEATURE [App::DocumentObjectGroupPython] G4_TOLUENE  # scripted group (container) (typed FeaturePython)
  Dunit = g/cm3
  Dvalue = 0.8669
  Group = -> [C_element114,H_element104]
  conduct = 2
  density = 1
  expand = 3
  formula = G4_TOLUENE
  name = G4_TOLUENE
  specific = 4
FEATURE [App::DocumentObjectGroupPython] C_element115  label="C_element : 062"  # scripted group (container) (typed FeaturePython)
  n = 2
  ref = C_element
FEATURE [App::DocumentObjectGroupPython] H_element105  label="H_element : 056"  # scripted group (container) (typed FeaturePython)
  n = 1
  ref = H_element
FEATURE [App::DocumentObjectGroupPython] Cl_element028  label="Cl_element : 014"  # scripted group (container) (typed FeaturePython)
  n = 3
  ref = Cl_element
FEATURE [App::DocumentObjectGroupPython] G4_TRICHLOROETHYLENE  # scripted group (container) (typed FeaturePython)
  Dunit = g/cm3
  Dvalue = 1.46
  Group = -> [C_element115,H_element105,Cl_element028]
  conduct = 2
  density = 1
  expand = 3
  formula = G4_TRICHLOROETHYLENE
  name = G4_TRICHLOROETHYLENE
  specific = 4
FEATURE [App::DocumentObjectGroupPython] C_element116  label="C_element : 063"  # scripted group (container) (typed FeaturePython)
  n = 6
  ref = C_element
FEATURE [App::DocumentObjectGroupPython] H_element106  label="H_element : 15"  # scripted group (container) (typed FeaturePython)
  n = 15
  ref = H_element
FEATURE [App::DocumentObjectGroupPython] O_element099  label="O_element : 053"  # scripted group (container) (typed FeaturePython)
  n = 4
  ref = O_element
FEATURE [App::DocumentObjectGroupPython] P_element012  label="P_element : 1"  # scripted group (container) (typed FeaturePython)
  n = 1
  ref = P_element
FEATURE [App::DocumentObjectGroupPython] G4_TRIETHYL_PHOSPHATE  # scripted group (container) (typed FeaturePython)
  Dunit = g/cm3
  Dvalue = 1.07
  Group = -> [C_element116,H_element106,O_element099,P_element012]
  conduct = 2
  density = 1
  expand = 3
  formula = G4_TRIETHYL_PHOSPHATE
  name = G4_TRIETHYL_PHOSPHATE
  specific = 4
FEATURE [App::DocumentObjectGroupPython] W_element003  label="W_element : 003"  # scripted group (container) (typed FeaturePython)
  n = 1
  ref = W_element
FEATURE [App::DocumentObjectGroupPython] F_element017  label="F_element : 6"  # scripted group (container) (typed FeaturePython)
  n = 6
  ref = F_element
FEATURE [App::DocumentObjectGroupPython] G4_TUNGSTEN_HEXAFLUORIDE  # scripted group (container) (typed FeaturePython)
  Dunit = g/cm3
  Dvalue = 2.4
  Group = -> [W_element003,F_element017]
  conduct = 2
  density = 1
  expand = 3
  formula = G4_TUNGSTEN_HEXAFLUORIDE
  name = G4_TUNGSTEN_HEXAFLUORIDE
  specific = 4
FEATURE [App::DocumentObjectGroupPython] U_element001  label="U_element : 1"  # scripted group (container) (typed FeaturePython)
  n = 1
  ref = U_element
FEATURE [App::DocumentObjectGroupPython] C_element117  label="C_element : 064"  # scripted group (container) (typed FeaturePython)
  n = 2
  ref = C_element
FEATURE [App::DocumentObjectGroupPython] G4_URANIUM_DICARBIDE  # scripted group (container) (typed FeaturePython)
  Dunit = g/cm3
  Dvalue = 11.28
  Group = -> [U_element001,C_element117]
  conduct = 2
  density = 1
  expand = 3
  formula = G4_URANIUM_DICARBIDE
  name = G4_URANIUM_DICARBIDE
  specific = 4
FEATURE [App::DocumentObjectGroupPython] U_element002  label="U_element : 002"  # scripted group (container) (typed FeaturePython)
  n = 1
  ref = U_element
FEATURE [App::DocumentObjectGroupPython] C_element118  label="C_element : 065"  # scripted group (container) (typed FeaturePython)
  n = 1
  ref = C_element
FEATURE [App::DocumentObjectGroupPython] G4_URANIUM_MONOCARBIDE  # scripted group (container) (typed FeaturePython)
  Dunit = g/cm3
  Dvalue = 13.63
  Group = -> [U_element002,C_element118]
  conduct = 2
  density = 1
  expand = 3
  formula = G4_URANIUM_MONOCARBIDE
  name = G4_URANIUM_MONOCARBIDE
  specific = 4
FEATURE [App::DocumentObjectGroupPython] U_element003  label="U_element : 003"  # scripted group (container) (typed FeaturePython)
  n = 1
  ref = U_element
FEATURE [App::DocumentObjectGroupPython] O_element100  label="O_element : 054"  # scripted group (container) (typed FeaturePython)
  n = 2
  ref = O_element
FEATURE [App::DocumentObjectGroupPython] G4_URANIUM_OXIDE  # scripted group (container) (typed FeaturePython)
  Dunit = g/cm3
  Dvalue = 10.96
  Group = -> [U_element003,O_element100]
  conduct = 2
  density = 1
  expand = 3
  formula = G4_URANIUM_OXIDE
  name = G4_URANIUM_OXIDE
  specific = 4
FEATURE [App::DocumentObjectGroupPython] C_element119  label="C_element : 066"  # scripted group (container) (typed FeaturePython)
  n = 1
  ref = C_element
FEATURE [App::DocumentObjectGroupPython] H_element107  label="H_element : 057"  # scripted group (container) (typed FeaturePython)
  n = 4
  ref = H_element
FEATURE [App::DocumentObjectGroupPython] N_element046  label="N_element : 019"  # scripted group (container) (typed FeaturePython)
  n = 2
  ref = N_element
FEATURE [App::DocumentObjectGroupPython] O_element101  label="O_element : 055"  # scripted group (container) (typed FeaturePython)
  n = 1
  ref = O_element
FEATURE [App::DocumentObjectGroupPython] G4_UREA  # scripted group (container) (typed FeaturePython)
  Dunit = g/cm3
  Dvalue = 1.323
  Group = -> [C_element119,H_element107,N_element046,O_element101]
  conduct = 2
  density = 1
  expand = 3
  formula = G4_UREA
  name = G4_UREA
  specific = 4
FEATURE [App::DocumentObjectGroupPython] C_element120  label="C_element : 067"  # scripted group (container) (typed FeaturePython)
  n = 5
  ref = C_element
FEATURE [App::DocumentObjectGroupPython] H_element108  label="H_element : 058"  # scripted group (container) (typed FeaturePython)
  n = 11
  ref = H_element
FEATURE [App::DocumentObjectGroupPython] N_element047  label="N_element : 020"  # scripted group (container) (typed FeaturePython)
  n = 1
  ref = N_element
FEATURE [App::DocumentObjectGroupPython] O_element102  label="O_element : 056"  # scripted group (container) (typed FeaturePython)
  n = 2
  ref = O_element
FEATURE [App::DocumentObjectGroupPython] G4_VALINE  # scripted group (container) (typed FeaturePython)
  Dunit = g/cm3
  Dvalue = 1.23
  Group = -> [C_element120,H_element108,N_element047,O_element102]
  conduct = 2
  density = 1
  expand = 3
  formula = G4_VALINE
  name = G4_VALINE
  specific = 4
FEATURE [App::DocumentObjectGroupPython] H_element109  label="H_element : 0.009"  # scripted group (container) (typed FeaturePython)
  n = 0.009417
FEATURE [App::DocumentObjectGroupPython] C_element121  label="C_element : 0.281"  # scripted group (container) (typed FeaturePython)
  n = 0.280555
FEATURE [App::DocumentObjectGroupPython] F_element018  label="F_element : 0.710"  # scripted group (container) (typed FeaturePython)
  n = 0.710028
FEATURE [App::DocumentObjectGroupPython] G4_VITON  # scripted group (container) (typed FeaturePython)
  Dunit = g/cm3
  Dvalue = 1.8
  Group = -> [H_element109,C_element121,F_element018]
  conduct = 2
  density = 1
  expand = 3
  formula = G4_VITON
  name = G4_VITON
  specific = 4
FEATURE [App::DocumentObjectGroupPython] H_element110  label="H_element : 059"  # scripted group (container) (typed FeaturePython)
  n = 2
  ref = H_element
FEATURE [App::DocumentObjectGroupPython] O_element103  label="O_element : 057"  # scripted group (container) (typed FeaturePython)
  n = 1
  ref = O_element
FEATURE [App::DocumentObjectGroupPython] G4_WATER  # scripted group (container) (typed FeaturePython)
  Dunit = g/cm3
  Dvalue = 1
  Group = -> [H_element110,O_element103]
  conduct = 2
  density = 1
  expand = 3
  formula = G4_WATER
  name = G4_WATER
  specific = 4
FEATURE [App::DocumentObjectGroupPython] H_element111  label="H_element : 060"  # scripted group (container) (typed FeaturePython)
  n = 2
  ref = H_element
FEATURE [App::DocumentObjectGroupPython] O_element104  label="O_element : 058"  # scripted group (container) (typed FeaturePython)
  n = 1
  ref = O_element
FEATURE [App::DocumentObjectGroupPython] G4_WATER_VAPOR  # scripted group (container) (typed FeaturePython)
  Dunit = g/cm3
  Dvalue = 0.000756182
  Group = -> [H_element111,O_element104]
  conduct = 2
  density = 1
  expand = 3
  formula = G4_WATER_VAPOR
  name = G4_WATER_VAPOR
  specific = 4
FEATURE [App::DocumentObjectGroupPython] C_element122  label="C_element : 068"  # scripted group (container) (typed FeaturePython)
  n = 8
  ref = C_element
FEATURE [App::DocumentObjectGroupPython] H_element112  label="H_element : 061"  # scripted group (container) (typed FeaturePython)
  n = 10
  ref = H_element
FEATURE [App::DocumentObjectGroupPython] G4_XYLENE  # scripted group (container) (typed FeaturePython)
  Dunit = g/cm3
  Dvalue = 0.87
  Group = -> [C_element122,H_element112]
  conduct = 2
  density = 1
  expand = 3
  formula = G4_XYLENE
  name = G4_XYLENE
  specific = 4
FEATURE [App::DocumentObjectGroupPython] C_element123  label="C_element : 069"  # scripted group (container) (typed FeaturePython)
  n = 1
  ref = C_element
FEATURE [App::DocumentObjectGroupPython] G4_GRAPHITE  # scripted group (container) (typed FeaturePython)
  Dunit = g/cm3
  Dvalue = 2.21
  Group = -> [C_element123]
  conduct = 2
  density = 1
  expand = 3
  formula = G4_GRAPHITE
  name = G4_GRAPHITE
  specific = 4
FEATURE [App::DocumentObjectGroupPython] NIST  # scripted group (container) (typed FeaturePython)
  Group = -> [G4_A_150_TISSUE,G4_ACETONE,G4_ACETYLENE,G4_ADENINE,G4_ADIPOSE_TISSUE_ICRP,G4_AIR,G4_ALANINE,G4_ALUMINUM_OXIDE,G4_AMBER,G4_AMMONIA,G4_ANILINE,G4_ANTHRACENE,G4_B_100_BONE,G4_BAKELITE,G4_BARIUM_FLUORIDE,G4_BARIUM_SULFATE,G4_BENZENE,G4_BERYLLIUM_OXIDE,G4_BGO,G4_BLOOD_ICRP,G4_BONE_COMPACT_ICRU,G4_BONE_CORTICAL_ICRP,G4_BORON_CARBIDE,G4_BORON_OXIDE,G4_BRAIN_ICRP,G4_BUTANE,G4_N_BUTYL_ALCOHOL,G4_C_552,+152 more]
FEATURE [App::DocumentObjectGroupPython] H_element113  label="H_element : 062"  # scripted group (container) (typed FeaturePython)
  n = 1
  ref = H_element
FEATURE [App::DocumentObjectGroupPython] G4_H  # scripted group (container) (typed FeaturePython)
  Dunit = g/cm3
  Dvalue = 8.3748e-05
  Group = -> [H_element113]
  conduct = 2
  density = 1
  expand = 3
  formula = H
  name = G4_H
  specific = 4
FEATURE [App::DocumentObjectGroupPython] He_element001  label="He_element : 1"  # scripted group (container) (typed FeaturePython)
  n = 1
  ref = He_element
FEATURE [App::DocumentObjectGroupPython] G4_He  # scripted group (container) (typed FeaturePython)
  Dunit = g/cm3
  Dvalue = 0.000166322
  Group = -> [He_element001]
  conduct = 2
  density = 1
  expand = 3
  formula = He
  name = G4_He
  specific = 4
FEATURE [App::DocumentObjectGroupPython] Li_element008  label="Li_element : 008"  # scripted group (container) (typed FeaturePython)
  n = 1
  ref = Li_element
FEATURE [App::DocumentObjectGroupPython] G4_Li  # scripted group (container) (typed FeaturePython)
  Dunit = g/cm3
  Dvalue = 0.534
  Group = -> [Li_element008]
  conduct = 2
  density = 1
  expand = 3
  formula = Li
  name = G4_Li
  specific = 4
FEATURE [App::DocumentObjectGroupPython] Be_element002  label="Be_element : 002"  # scripted group (container) (typed FeaturePython)
  n = 1
  ref = Be_element
FEATURE [App::DocumentObjectGroupPython] G4_Be  # scripted group (container) (typed FeaturePython)
  Dunit = g/cm3
  Dvalue = 1.848
  Group = -> [Be_element002]
  conduct = 2
  density = 1
  expand = 3
  formula = Be
  name = G4_Be
  specific = 4
FEATURE [App::DocumentObjectGroupPython] B_element007  label="B_element : 007"  # scripted group (container) (typed FeaturePython)
  n = 1
  ref = B_element
FEATURE [App::DocumentObjectGroupPython] G4_B  # scripted group (container) (typed FeaturePython)
  Dunit = g/cm3
  Dvalue = 2.37
  Group = -> [B_element007]
  conduct = 2
  density = 1
  expand = 3
  formula = B
  name = G4_B
  specific = 4
FEATURE [App::DocumentObjectGroupPython] C_element124  label="C_element : 070"  # scripted group (container) (typed FeaturePython)
  n = 1
  ref = C_element
FEATURE [App::DocumentObjectGroupPython] G4_C  # scripted group (container) (typed FeaturePython)
  Dunit = g/cm3
  Dvalue = 2
  Group = -> [C_element124]
  conduct = 2
  density = 1
  expand = 3
  formula = C
  name = G4_C
  specific = 4
FEATURE [App::DocumentObjectGroupPython] N_element048  label="N_element : 021"  # scripted group (container) (typed FeaturePython)
  n = 1
  ref = N_element
FEATURE [App::DocumentObjectGroupPython] G4_N  # scripted group (container) (typed FeaturePython)
  Dunit = g/cm3
  Dvalue = 0.0011652
  Group = -> [N_element048]
  conduct = 2
  density = 1
  expand = 3
  formula = N
  name = G4_N
  specific = 4
FEATURE [App::DocumentObjectGroupPython] O_element105  label="O_element : 059"  # scripted group (container) (typed FeaturePython)
  n = 1
  ref = O_element
FEATURE [App::DocumentObjectGroupPython] G4_O  # scripted group (container) (typed FeaturePython)
  Dunit = g/cm3
  Dvalue = 0.00133151
  Group = -> [O_element105]
  conduct = 2
  density = 1
  expand = 3
  formula = O
  name = G4_O
  specific = 4
FEATURE [App::DocumentObjectGroupPython] F_element019  label="F_element : 008"  # scripted group (container) (typed FeaturePython)
  n = 1
  ref = F_element
FEATURE [App::DocumentObjectGroupPython] G4_F  # scripted group (container) (typed FeaturePython)
  Dunit = g/cm3
  Dvalue = 0.00158029
  Group = -> [F_element019]
  conduct = 2
  density = 1
  expand = 3
  formula = F
  name = G4_F
  specific = 4
FEATURE [App::DocumentObjectGroupPython] Ne_element001  label="Ne_element : 1"  # scripted group (container) (typed FeaturePython)
  n = 1
  ref = Ne_element
FEATURE [App::DocumentObjectGroupPython] G4_Ne  # scripted group (container) (typed FeaturePython)
  Dunit = g/cm3
  Dvalue = 0.000838505
  Group = -> [Ne_element001]
  conduct = 2
  density = 1
  expand = 3
  formula = Ne
  name = G4_Ne
  specific = 4
FEATURE [App::DocumentObjectGroupPython] Na_element020  label="Na_element : 005"  # scripted group (container) (typed FeaturePython)
  n = 1
  ref = Na_element
FEATURE [App::DocumentObjectGroupPython] G4_Na  # scripted group (container) (typed FeaturePython)
  Dunit = g/cm3
  Dvalue = 0.971
  Group = -> [Na_element020]
  conduct = 2
  density = 1
  expand = 3
  formula = Na
  name = G4_Na
  specific = 4
FEATURE [App::DocumentObjectGroupPython] Mg_element011  label="Mg_element : 005"  # scripted group (container) (typed FeaturePython)
  n = 1
  ref = Mg_element
FEATURE [App::DocumentObjectGroupPython] G4_Mg  # scripted group (container) (typed FeaturePython)
  Dunit = g/cm3
  Dvalue = 1.74
  Group = -> [Mg_element011]
  conduct = 2
  density = 1
  expand = 3
  formula = Mg
  name = G4_Mg
  specific = 4
FEATURE [App::DocumentObjectGroupPython] Al_element004  label="Al_element : 1"  # scripted group (container) (typed FeaturePython)
  n = 1
  ref = Al_element
FEATURE [App::DocumentObjectGroupPython] G4_Al  # scripted group (container) (typed FeaturePython)
  Dunit = g/cm3
  Dvalue = 2.699
  Group = -> [Al_element004]
  conduct = 2
  density = 1
  expand = 3
  formula = Al
  name = G4_Al
  specific = 4
FEATURE [App::DocumentObjectGroupPython] Si_element007  label="Si_element : 002"  # scripted group (container) (typed FeaturePython)
  n = 1
  ref = Si_element
FEATURE [App::DocumentObjectGroupPython] G4_Si  # scripted group (container) (typed FeaturePython)
  Dunit = g/cm3
  Dvalue = 2.33
  Group = -> [Si_element007]
  conduct = 2
  density = 1
  expand = 3
  formula = Si
  name = G4_Si
  specific = 4
FEATURE [App::DocumentObjectGroupPython] P_element013  label="P_element : 002"  # scripted group (container) (typed FeaturePython)
  n = 1
  ref = P_element
FEATURE [App::DocumentObjectGroupPython] G4_P  # scripted group (container) (typed FeaturePython)
  Dunit = g/cm3
  Dvalue = 2.2
  Group = -> [P_element013]
  conduct = 2
  density = 1
  expand = 3
  formula = P
  name = G4_P
  specific = 4
FEATURE [App::DocumentObjectGroupPython] S_element023  label="S_element : 007"  # scripted group (container) (typed FeaturePython)
  n = 1
  ref = S_element
FEATURE [App::DocumentObjectGroupPython] G4_S  # scripted group (container) (typed FeaturePython)
  Dunit = g/cm3
  Dvalue = 2
  Group = -> [S_element023]
  conduct = 2
  density = 1
  expand = 3
  formula = S
  name = G4_S
  specific = 4
FEATURE [App::DocumentObjectGroupPython] Cl_element029  label="Cl_element : 015"  # scripted group (container) (typed FeaturePython)
  n = 1
  ref = Cl_element
FEATURE [App::DocumentObjectGroupPython] G4_Cl  # scripted group (container) (typed FeaturePython)
  Dunit = g/cm3
  Dvalue = 0.00299473
  Group = -> [Cl_element029]
  conduct = 2
  density = 1
  expand = 3
  formula = Cl
  name = G4_Cl
  specific = 4
FEATURE [App::DocumentObjectGroupPython] Ar_element002  label="Ar_element : 1"  # scripted group (container) (typed FeaturePython)
  n = 1
  ref = Ar_element
FEATURE [App::DocumentObjectGroupPython] G4_Ar  # scripted group (container) (typed FeaturePython)
  Dunit = g/cm3
  Dvalue = 0.00166201
  Group = -> [Ar_element002]
  conduct = 2
  density = 1
  expand = 3
  formula = Ar
  name = G4_Ar
  specific = 4
FEATURE [App::DocumentObjectGroupPython] K_element013  label="K_element : 003"  # scripted group (container) (typed FeaturePython)
  n = 1
  ref = K_element
FEATURE [App::DocumentObjectGroupPython] G4_K  # scripted group (container) (typed FeaturePython)
  Dunit = g/cm3
  Dvalue = 0.862
  Group = -> [K_element013]
  conduct = 2
  density = 1
  expand = 3
  formula = K
  name = G4_K
  specific = 4
FEATURE [App::DocumentObjectGroupPython] Ca_element014  label="Ca_element : 007"  # scripted group (container) (typed FeaturePython)
  n = 1
  ref = Ca_element
FEATURE [App::DocumentObjectGroupPython] G4_Ca  # scripted group (container) (typed FeaturePython)
  Dunit = g/cm3
  Dvalue = 1.55
  Group = -> [Ca_element014]
  conduct = 2
  density = 1
  expand = 3
  formula = Ca
  name = G4_Ca
  specific = 4
FEATURE [App::DocumentObjectGroupPython] Sc_element001  label="Sc_element : 1"  # scripted group (container) (typed FeaturePython)
  n = 1
  ref = Sc_element
FEATURE [App::DocumentObjectGroupPython] G4_Sc  # scripted group (container) (typed FeaturePython)
  Dunit = g/cm3
  Dvalue = 2.989
  Group = -> [Sc_element001]
  conduct = 2
  density = 1
  expand = 3
  formula = Sc
  name = G4_Sc
  specific = 4
FEATURE [App::DocumentObjectGroupPython] Ti_element004  label="Ti_element : 002"  # scripted group (container) (typed FeaturePython)
  n = 1
  ref = Ti_element
FEATURE [App::DocumentObjectGroupPython] G4_Ti  # scripted group (container) (typed FeaturePython)
  Dunit = g/cm3
  Dvalue = 4.54
  Group = -> [Ti_element004]
  conduct = 2
  density = 1
  expand = 3
  formula = Ti
  name = G4_Ti
  specific = 4
FEATURE [App::DocumentObjectGroupPython] V_element001  label="V_element : 1"  # scripted group (container) (typed FeaturePython)
  n = 1
  ref = V_element
FEATURE [App::DocumentObjectGroupPython] G4_V  # scripted group (container) (typed FeaturePython)
  Dunit = g/cm3
  Dvalue = 6.11
  Group = -> [V_element001]
  conduct = 2
  density = 1
  expand = 3
  formula = V
  name = G4_V
  specific = 4
FEATURE [App::DocumentObjectGroupPython] Cr_element001  label="Cr_element : 1"  # scripted group (container) (typed FeaturePython)
  n = 1
  ref = Cr_element
FEATURE [App::DocumentObjectGroupPython] G4_Cr  # scripted group (container) (typed FeaturePython)
  Dunit = g/cm3
  Dvalue = 7.18
  Group = -> [Cr_element001]
  conduct = 2
  density = 1
  expand = 3
  formula = Cr
  name = G4_Cr
  specific = 4
FEATURE [App::DocumentObjectGroupPython] Mn_element001  label="Mn_element : 1"  # scripted group (container) (typed FeaturePython)
  n = 1
  ref = Mn_element
FEATURE [App::DocumentObjectGroupPython] G4_Mn  # scripted group (container) (typed FeaturePython)
  Dunit = g/cm3
  Dvalue = 7.44
  Group = -> [Mn_element001]
  conduct = 2
  density = 1
  expand = 3
  formula = Mn
  name = G4_Mn
  specific = 4
FEATURE [App::DocumentObjectGroupPython] Fe_element007  label="Fe_element : 004"  # scripted group (container) (typed FeaturePython)
  n = 1
  ref = Fe_element
FEATURE [App::DocumentObjectGroupPython] G4_Fe  # scripted group (container) (typed FeaturePython)
  Dunit = g/cm3
  Dvalue = 7.874
  Group = -> [Fe_element007]
  conduct = 2
  density = 1
  expand = 3
  formula = Fe
  name = G4_Fe
  specific = 4
FEATURE [App::DocumentObjectGroupPython] Co_element001  label="Co_element : 1"  # scripted group (container) (typed FeaturePython)
  n = 1
  ref = Co_element
FEATURE [App::DocumentObjectGroupPython] G4_Co  # scripted group (container) (typed FeaturePython)
  Dunit = g/cm3
  Dvalue = 8.9
  Group = -> [Co_element001]
  conduct = 2
  density = 1
  expand = 3
  formula = Co
  name = G4_Co
  specific = 4
FEATURE [App::DocumentObjectGroupPython] Ni_element001  label="Ni_element : 1"  # scripted group (container) (typed FeaturePython)
  n = 1
  ref = Ni_element
FEATURE [App::DocumentObjectGroupPython] G4_Ni  # scripted group (container) (typed FeaturePython)
  Dunit = g/cm3
  Dvalue = 8.902
  Group = -> [Ni_element001]
  conduct = 2
  density = 1
  expand = 3
  formula = Ni
  name = G4_Ni
  specific = 4
FEATURE [App::DocumentObjectGroupPython] Cu_element001  label="Cu_element : 1"  # scripted group (container) (typed FeaturePython)
  n = 1
  ref = Cu_element
FEATURE [App::DocumentObjectGroupPython] G4_Cu  # scripted group (container) (typed FeaturePython)
  Dunit = g/cm3
  Dvalue = 8.96
  Group = -> [Cu_element001]
  conduct = 2
  density = 1
  expand = 3
  formula = Cu
  name = G4_Cu
  specific = 4
FEATURE [App::DocumentObjectGroupPython] Zn_element001  label="Zn_element : 1"  # scripted group (container) (typed FeaturePython)
  n = 1
  ref = Zn_element
FEATURE [App::DocumentObjectGroupPython] G4_Zn  # scripted group (container) (typed FeaturePython)
  Dunit = g/cm3
  Dvalue = 7.133
  Group = -> [Zn_element001]
  conduct = 2
  density = 1
  expand = 3
  formula = Zn
  name = G4_Zn
  specific = 4
FEATURE [App::DocumentObjectGroupPython] Ga_element002  label="Ga_element : 002"  # scripted group (container) (typed FeaturePython)
  n = 1
  ref = Ga_element
FEATURE [App::DocumentObjectGroupPython] G4_Ga  # scripted group (container) (typed FeaturePython)
  Dunit = g/cm3
  Dvalue = 5.904
  Group = -> [Ga_element002]
  conduct = 2
  density = 1
  expand = 3
  formula = Ga
  name = G4_Ga
  specific = 4
FEATURE [App::DocumentObjectGroupPython] Ge_element002  label="Ge_element : 1"  # scripted group (container) (typed FeaturePython)
  n = 1
  ref = Ge_element
FEATURE [App::DocumentObjectGroupPython] G4_Ge  # scripted group (container) (typed FeaturePython)
  Dunit = g/cm3
  Dvalue = 5.323
  Group = -> [Ge_element002]
  conduct = 2
  density = 1
  expand = 3
  formula = Ge
  name = G4_Ge
  specific = 4
FEATURE [App::DocumentObjectGroupPython] As_element003  label="As_element : 002"  # scripted group (container) (typed FeaturePython)
  n = 1
  ref = As_element
FEATURE [App::DocumentObjectGroupPython] G4_As  # scripted group (container) (typed FeaturePython)
  Dunit = g/cm3
  Dvalue = 5.73
  Group = -> [As_element003]
  conduct = 2
  density = 1
  expand = 3
  formula = As
  name = G4_As
  specific = 4
FEATURE [App::DocumentObjectGroupPython] Se_element001  label="Se_element : 1"  # scripted group (container) (typed FeaturePython)
  n = 1
  ref = Se_element
FEATURE [App::DocumentObjectGroupPython] G4_Se  # scripted group (container) (typed FeaturePython)
  Dunit = g/cm3
  Dvalue = 4.5
  Group = -> [Se_element001]
  conduct = 2
  density = 1
  expand = 3
  formula = Se
  name = G4_Se
  specific = 4
FEATURE [App::DocumentObjectGroupPython] Br_element007  label="Br_element : 004"  # scripted group (container) (typed FeaturePython)
  n = 1
  ref = Br_element
FEATURE [App::DocumentObjectGroupPython] G4_Br  # scripted group (container) (typed FeaturePython)
  Dunit = g/cm3
  Dvalue = 0.0070721
  Group = -> [Br_element007]
  conduct = 2
  density = 1
  expand = 3
  formula = Br
  name = G4_Br
  specific = 4
FEATURE [App::DocumentObjectGroupPython] Kr_element001  label="Kr_element : 1"  # scripted group (container) (typed FeaturePython)
  n = 1
  ref = Kr_element
FEATURE [App::DocumentObjectGroupPython] G4_Kr  # scripted group (container) (typed FeaturePython)
  Dunit = g/cm3
  Dvalue = 0.00347832
  Group = -> [Kr_element001]
  conduct = 2
  density = 1
  expand = 3
  formula = Kr
  name = G4_Kr
  specific = 4
FEATURE [App::DocumentObjectGroupPython] Rb_element001  label="Rb_element : 1"  # scripted group (container) (typed FeaturePython)
  n = 1
  ref = Rb_element
FEATURE [App::DocumentObjectGroupPython] G4_Rb  # scripted group (container) (typed FeaturePython)
  Dunit = g/cm3
  Dvalue = 1.532
  Group = -> [Rb_element001]
  conduct = 2
  density = 1
  expand = 3
  formula = Rb
  name = G4_Rb
  specific = 4
FEATURE [App::DocumentObjectGroupPython] Sr_element001  label="Sr_element : 1"  # scripted group (container) (typed FeaturePython)
  n = 1
  ref = Sr_element
FEATURE [App::DocumentObjectGroupPython] G4_Sr  # scripted group (container) (typed FeaturePython)
  Dunit = g/cm3
  Dvalue = 2.54
  Group = -> [Sr_element001]
  conduct = 2
  density = 1
  expand = 3
  formula = Sr
  name = G4_Sr
  specific = 4
FEATURE [App::DocumentObjectGroupPython] Y_element001  label="Y_element : 1"  # scripted group (container) (typed FeaturePython)
  n = 1
  ref = Y_element
FEATURE [App::DocumentObjectGroupPython] G4_Y  # scripted group (container) (typed FeaturePython)
  Dunit = g/cm3
  Dvalue = 4.469
  Group = -> [Y_element001]
  conduct = 2
  density = 1
  expand = 3
  formula = Y
  name = G4_Y
  specific = 4
FEATURE [App::DocumentObjectGroupPython] Zr_element001  label="Zr_element : 1"  # scripted group (container) (typed FeaturePython)
  n = 1
  ref = Zr_element
FEATURE [App::DocumentObjectGroupPython] G4_Zr  # scripted group (container) (typed FeaturePython)
  Dunit = g/cm3
  Dvalue = 6.506
  Group = -> [Zr_element001]
  conduct = 2
  density = 1
  expand = 3
  formula = Zr
  name = G4_Zr
  specific = 4
FEATURE [App::DocumentObjectGroupPython] Nb_element001  label="Nb_element : 1"  # scripted group (container) (typed FeaturePython)
  n = 1
  ref = Nb_element
FEATURE [App::DocumentObjectGroupPython] G4_Nb  # scripted group (container) (typed FeaturePython)
  Dunit = g/cm3
  Dvalue = 8.57
  Group = -> [Nb_element001]
  conduct = 2
  density = 1
  expand = 3
  formula = Nb
  name = G4_Nb
  specific = 4
FEATURE [App::DocumentObjectGroupPython] Mo_element001  label="Mo_element : 1"  # scripted group (container) (typed FeaturePython)
  n = 1
  ref = Mo_element
FEATURE [App::DocumentObjectGroupPython] G4_Mo  # scripted group (container) (typed FeaturePython)
  Dunit = g/cm3
  Dvalue = 10.22
  Group = -> [Mo_element001]
  conduct = 2
  density = 1
  expand = 3
  formula = Mo
  name = G4_Mo
  specific = 4
FEATURE [App::DocumentObjectGroupPython] Tc_element001  label="Tc_element : 1"  # scripted group (container) (typed FeaturePython)
  n = 1
  ref = Tc_element
FEATURE [App::DocumentObjectGroupPython] G4_Tc  # scripted group (container) (typed FeaturePython)
  Dunit = g/cm3
  Dvalue = 11.5
  Group = -> [Tc_element001]
  conduct = 2
  density = 1
  expand = 3
  formula = Tc
  name = G4_Tc
  specific = 4
FEATURE [App::DocumentObjectGroupPython] Ru_element001  label="Ru_element : 1"  # scripted group (container) (typed FeaturePython)
  n = 1
  ref = Ru_element
FEATURE [App::DocumentObjectGroupPython] G4_Ru  # scripted group (container) (typed FeaturePython)
  Dunit = g/cm3
  Dvalue = 12.41
  Group = -> [Ru_element001]
  conduct = 2
  density = 1
  expand = 3
  formula = Ru
  name = G4_Ru
  specific = 4
FEATURE [App::DocumentObjectGroupPython] Rh_element001  label="Rh_element : 1"  # scripted group (container) (typed FeaturePython)
  n = 1
  ref = Rh_element
FEATURE [App::DocumentObjectGroupPython] G4_Rh  # scripted group (container) (typed FeaturePython)
  Dunit = g/cm3
  Dvalue = 12.41
  Group = -> [Rh_element001]
  conduct = 2
  density = 1
  expand = 3
  formula = Rh
  name = G4_Rh
  specific = 4
FEATURE [App::DocumentObjectGroupPython] Pd_element001  label="Pd_element : 1"  # scripted group (container) (typed FeaturePython)
  n = 1
  ref = Pd_element
FEATURE [App::DocumentObjectGroupPython] G4_Pd  # scripted group (container) (typed FeaturePython)
  Dunit = g/cm3
  Dvalue = 12.02
  Group = -> [Pd_element001]
  conduct = 2
  density = 1
  expand = 3
  formula = Pd
  name = G4_Pd
  specific = 4
FEATURE [App::DocumentObjectGroupPython] Ag_element006  label="Ag_element : 004"  # scripted group (container) (typed FeaturePython)
  n = 1
  ref = Ag_element
FEATURE [App::DocumentObjectGroupPython] G4_Ag  # scripted group (container) (typed FeaturePython)
  Dunit = g/cm3
  Dvalue = 10.5
  Group = -> [Ag_element006]
  conduct = 2
  density = 1
  expand = 3
  formula = Ag
  name = G4_Ag
  specific = 4
FEATURE [App::DocumentObjectGroupPython] Cd_element003  label="Cd_element : 003"  # scripted group (container) (typed FeaturePython)
  n = 1
  ref = Cd_element
FEATURE [App::DocumentObjectGroupPython] G4_Cd  # scripted group (container) (typed FeaturePython)
  Dunit = g/cm3
  Dvalue = 8.65
  Group = -> [Cd_element003]
  conduct = 2
  density = 1
  expand = 3
  formula = Cd
  name = G4_Cd
  specific = 4
FEATURE [App::DocumentObjectGroupPython] In_element001  label="In_element : 1"  # scripted group (container) (typed FeaturePython)
  n = 1
  ref = In_element
FEATURE [App::DocumentObjectGroupPython] G4_In  # scripted group (container) (typed FeaturePython)
  Dunit = g/cm3
  Dvalue = 7.31
  Group = -> [In_element001]
  conduct = 2
  density = 1
  expand = 3
  formula = In
  name = G4_In
  specific = 4
FEATURE [App::DocumentObjectGroupPython] Sn_element001  label="Sn_element : 1"  # scripted group (container) (typed FeaturePython)
  n = 1
  ref = Sn_element
FEATURE [App::DocumentObjectGroupPython] G4_Sn  # scripted group (container) (typed FeaturePython)
  Dunit = g/cm3
  Dvalue = 7.31
  Group = -> [Sn_element001]
  conduct = 2
  density = 1
  expand = 3
  formula = Sn
  name = G4_Sn
  specific = 4
FEATURE [App::DocumentObjectGroupPython] Sb_element001  label="Sb_element : 1"  # scripted group (container) (typed FeaturePython)
  n = 1
  ref = Sb_element
FEATURE [App::DocumentObjectGroupPython] G4_Sb  # scripted group (container) (typed FeaturePython)
  Dunit = g/cm3
  Dvalue = 6.691
  Group = -> [Sb_element001]
  conduct = 2
  density = 1
  expand = 3
  formula = Sb
  name = G4_Sb
  specific = 4
FEATURE [App::DocumentObjectGroupPython] Te_element002  label="Te_element : 002"  # scripted group (container) (typed FeaturePython)
  n = 1
  ref = Te_element
FEATURE [App::DocumentObjectGroupPython] G4_Te  # scripted group (container) (typed FeaturePython)
  Dunit = g/cm3
  Dvalue = 6.24
  Group = -> [Te_element002]
  conduct = 2
  density = 1
  expand = 3
  formula = Te
  name = G4_Te
  specific = 4
FEATURE [App::DocumentObjectGroupPython] I_element010  label="I_element : 006"  # scripted group (container) (typed FeaturePython)
  n = 1
  ref = I_element
FEATURE [App::DocumentObjectGroupPython] G4_I  # scripted group (container) (typed FeaturePython)
  Dunit = g/cm3
  Dvalue = 4.93
  Group = -> [I_element010]
  conduct = 2
  density = 1
  expand = 3
  formula = I
  name = G4_I
  specific = 4
FEATURE [App::DocumentObjectGroupPython] Xe_element001  label="Xe_element : 1"  # scripted group (container) (typed FeaturePython)
  n = 1
  ref = Xe_element
FEATURE [App::DocumentObjectGroupPython] G4_Xe  # scripted group (container) (typed FeaturePython)
  Dunit = g/cm3
  Dvalue = 0.00548536
  Group = -> [Xe_element001]
  conduct = 2
  density = 1
  expand = 3
  formula = Xe
  name = G4_Xe
  specific = 4
FEATURE [App::DocumentObjectGroupPython] Cs_element003  label="Cs_element : 003"  # scripted group (container) (typed FeaturePython)
  n = 1
  ref = Cs_element
FEATURE [App::DocumentObjectGroupPython] G4_Cs  # scripted group (container) (typed FeaturePython)
  Dunit = g/cm3
  Dvalue = 1.873
  Group = -> [Cs_element003]
  conduct = 2
  density = 1
  expand = 3
  formula = Cs
  name = G4_Cs
  specific = 4
FEATURE [App::DocumentObjectGroupPython] Ba_element003  label="Ba_element : 003"  # scripted group (container) (typed FeaturePython)
  n = 1
  ref = Ba_element
FEATURE [App::DocumentObjectGroupPython] G4_Ba  # scripted group (container) (typed FeaturePython)
  Dunit = g/cm3
  Dvalue = 3.5
  Group = -> [Ba_element003]
  conduct = 2
  density = 1
  expand = 3
  formula = Ba
  name = G4_Ba
  specific = 4
FEATURE [App::DocumentObjectGroupPython] La_element003  label="La_element : 003"  # scripted group (container) (typed FeaturePython)
  n = 1
  ref = La_element
FEATURE [App::DocumentObjectGroupPython] G4_La  # scripted group (container) (typed FeaturePython)
  Dunit = g/cm3
  Dvalue = 6.154
  Group = -> [La_element003]
  conduct = 2
  density = 1
  expand = 3
  formula = La
  name = G4_La
  specific = 4
FEATURE [App::DocumentObjectGroupPython] Ce_element002  label="Ce_element : 1"  # scripted group (container) (typed FeaturePython)
  n = 1
  ref = Ce_element
FEATURE [App::DocumentObjectGroupPython] G4_Ce  # scripted group (container) (typed FeaturePython)
  Dunit = g/cm3
  Dvalue = 6.657
  Group = -> [Ce_element002]
  conduct = 2
  density = 1
  expand = 3
  formula = Ce
  name = G4_Ce
  specific = 4
FEATURE [App::DocumentObjectGroupPython] Pr_element001  label="Pr_element : 1"  # scripted group (container) (typed FeaturePython)
  n = 1
  ref = Pr_element
FEATURE [App::DocumentObjectGroupPython] G4_Pr  # scripted group (container) (typed FeaturePython)
  Dunit = g/cm3
  Dvalue = 6.71
  Group = -> [Pr_element001]
  conduct = 2
  density = 1
  expand = 3
  formula = Pr
  name = G4_Pr
  specific = 4
FEATURE [App::DocumentObjectGroupPython] Nd_element001  label="Nd_element : 1"  # scripted group (container) (typed FeaturePython)
  n = 1
  ref = Nd_element
FEATURE [App::DocumentObjectGroupPython] G4_Nd  # scripted group (container) (typed FeaturePython)
  Dunit = g/cm3
  Dvalue = 6.9
  Group = -> [Nd_element001]
  conduct = 2
  density = 1
  expand = 3
  formula = Nd
  name = G4_Nd
  specific = 4
FEATURE [App::DocumentObjectGroupPython] Pm_element001  label="Pm_element : 1"  # scripted group (container) (typed FeaturePython)
  n = 1
  ref = Pm_element
FEATURE [App::DocumentObjectGroupPython] G4_Pm  # scripted group (container) (typed FeaturePython)
  Dunit = g/cm3
  Dvalue = 7.22
  Group = -> [Pm_element001]
  conduct = 2
  density = 1
  expand = 3
  formula = Pm
  name = G4_Pm
  specific = 4
FEATURE [App::DocumentObjectGroupPython] Sm_element001  label="Sm_element : 1"  # scripted group (container) (typed FeaturePython)
  n = 1
  ref = Sm_element
FEATURE [App::DocumentObjectGroupPython] G4_Sm  # scripted group (container) (typed FeaturePython)
  Dunit = g/cm3
  Dvalue = 7.46
  Group = -> [Sm_element001]
  conduct = 2
  density = 1
  expand = 3
  formula = Sm
  name = G4_Sm
  specific = 4
FEATURE [App::DocumentObjectGroupPython] Eu_element001  label="Eu_element : 1"  # scripted group (container) (typed FeaturePython)
  n = 1
  ref = Eu_element
FEATURE [App::DocumentObjectGroupPython] G4_Eu  # scripted group (container) (typed FeaturePython)
  Dunit = g/cm3
  Dvalue = 5.243
  Group = -> [Eu_element001]
  conduct = 2
  density = 1
  expand = 3
  formula = Eu
  name = G4_Eu
  specific = 4
FEATURE [App::DocumentObjectGroupPython] Gd_element002  label="Gd_element : 1"  # scripted group (container) (typed FeaturePython)
  n = 1
  ref = Gd_element
FEATURE [App::DocumentObjectGroupPython] G4_Gd  # scripted group (container) (typed FeaturePython)
  Dunit = g/cm3
  Dvalue = 7.9004
  Group = -> [Gd_element002]
  conduct = 2
  density = 1
  expand = 3
  formula = Gd
  name = G4_Gd
  specific = 4
FEATURE [App::DocumentObjectGroupPython] Tb_element001  label="Tb_element : 1"  # scripted group (container) (typed FeaturePython)
  n = 1
  ref = Tb_element
FEATURE [App::DocumentObjectGroupPython] G4_Tb  # scripted group (container) (typed FeaturePython)
  Dunit = g/cm3
  Dvalue = 8.229
  Group = -> [Tb_element001]
  conduct = 2
  density = 1
  expand = 3
  formula = Tb
  name = G4_Tb
  specific = 4
FEATURE [App::DocumentObjectGroupPython] Dy_element001  label="Dy_element : 1"  # scripted group (container) (typed FeaturePython)
  n = 1
  ref = Dy_element
FEATURE [App::DocumentObjectGroupPython] G4_Dy  # scripted group (container) (typed FeaturePython)
  Dunit = g/cm3
  Dvalue = 8.55
  Group = -> [Dy_element001]
  conduct = 2
  density = 1
  expand = 3
  formula = Dy
  name = G4_Dy
  specific = 4
FEATURE [App::DocumentObjectGroupPython] Ho_element001  label="Ho_element : 1"  # scripted group (container) (typed FeaturePython)
  n = 1
  ref = Ho_element
FEATURE [App::DocumentObjectGroupPython] G4_Ho  # scripted group (container) (typed FeaturePython)
  Dunit = g/cm3
  Dvalue = 8.795
  Group = -> [Ho_element001]
  conduct = 2
  density = 1
  expand = 3
  formula = Ho
  name = G4_Ho
  specific = 4
FEATURE [App::DocumentObjectGroupPython] Er_element001  label="Er_element : 1"  # scripted group (container) (typed FeaturePython)
  n = 1
  ref = Er_element
FEATURE [App::DocumentObjectGroupPython] G4_Er  # scripted group (container) (typed FeaturePython)
  Dunit = g/cm3
  Dvalue = 9.066
  Group = -> [Er_element001]
  conduct = 2
  density = 1
  expand = 3
  formula = Er
  name = G4_Er
  specific = 4
FEATURE [App::DocumentObjectGroupPython] Tm_element001  label="Tm_element : 1"  # scripted group (container) (typed FeaturePython)
  n = 1
  ref = Tm_element
FEATURE [App::DocumentObjectGroupPython] G4_Tm  # scripted group (container) (typed FeaturePython)
  Dunit = g/cm3
  Dvalue = 9.321
  Group = -> [Tm_element001]
  conduct = 2
  density = 1
  expand = 3
  formula = Tm
  name = G4_Tm
  specific = 4
FEATURE [App::DocumentObjectGroupPython] Yb_element001  label="Yb_element : 1"  # scripted group (container) (typed FeaturePython)
  n = 1
  ref = Yb_element
FEATURE [App::DocumentObjectGroupPython] G4_Yb  # scripted group (container) (typed FeaturePython)
  Dunit = g/cm3
  Dvalue = 6.73
  Group = -> [Yb_element001]
  conduct = 2
  density = 1
  expand = 3
  formula = Yb
  name = G4_Yb
  specific = 4
FEATURE [App::DocumentObjectGroupPython] Lu_element001  label="Lu_element : 1"  # scripted group (container) (typed FeaturePython)
  n = 1
  ref = Lu_element
FEATURE [App::DocumentObjectGroupPython] G4_Lu  # scripted group (container) (typed FeaturePython)
  Dunit = g/cm3
  Dvalue = 9.84
  Group = -> [Lu_element001]
  conduct = 2
  density = 1
  expand = 3
  formula = Lu
  name = G4_Lu
  specific = 4
FEATURE [App::DocumentObjectGroupPython] Hf_element001  label="Hf_element : 1"  # scripted group (container) (typed FeaturePython)
  n = 1
  ref = Hf_element
FEATURE [App::DocumentObjectGroupPython] G4_Hf  # scripted group (container) (typed FeaturePython)
  Dunit = g/cm3
  Dvalue = 13.31
  Group = -> [Hf_element001]
  conduct = 2
  density = 1
  expand = 3
  formula = Hf
  name = G4_Hf
  specific = 4
FEATURE [App::DocumentObjectGroupPython] Ta_element001  label="Ta_element : 1"  # scripted group (container) (typed FeaturePython)
  n = 1
  ref = Ta_element
FEATURE [App::DocumentObjectGroupPython] G4_Ta  # scripted group (container) (typed FeaturePython)
  Dunit = g/cm3
  Dvalue = 16.654
  Group = -> [Ta_element001]
  conduct = 2
  density = 1
  expand = 3
  formula = Ta
  name = G4_Ta
  specific = 4
FEATURE [App::DocumentObjectGroupPython] W_element004  label="W_element : 004"  # scripted group (container) (typed FeaturePython)
  n = 1
  ref = W_element
FEATURE [App::DocumentObjectGroupPython] G4_W  # scripted group (container) (typed FeaturePython)
  Dunit = g/cm3
  Dvalue = 19.3
  Group = -> [W_element004]
  conduct = 2
  density = 1
  expand = 3
  formula = W
  name = G4_W
  specific = 4
FEATURE [App::DocumentObjectGroupPython] Re_element001  label="Re_element : 1"  # scripted group (container) (typed FeaturePython)
  n = 1
  ref = Re_element
FEATURE [App::DocumentObjectGroupPython] G4_Re  # scripted group (container) (typed FeaturePython)
  Dunit = g/cm3
  Dvalue = 21.02
  Group = -> [Re_element001]
  conduct = 2
  density = 1
  expand = 3
  formula = Re
  name = G4_Re
  specific = 4
FEATURE [App::DocumentObjectGroupPython] Os_element001  label="Os_element : 1"  # scripted group (container) (typed FeaturePython)
  n = 1
  ref = Os_element
FEATURE [App::DocumentObjectGroupPython] G4_Os  # scripted group (container) (typed FeaturePython)
  Dunit = g/cm3
  Dvalue = 22.57
  Group = -> [Os_element001]
  conduct = 2
  density = 1
  expand = 3
  formula = Os
  name = G4_Os
  specific = 4
FEATURE [App::DocumentObjectGroupPython] Ir_element001  label="Ir_element : 1"  # scripted group (container) (typed FeaturePython)
  n = 1
  ref = Ir_element
FEATURE [App::DocumentObjectGroupPython] G4_Ir  # scripted group (container) (typed FeaturePython)
  Dunit = g/cm3
  Dvalue = 22.42
  Group = -> [Ir_element001]
  conduct = 2
  density = 1
  expand = 3
  formula = Ir
  name = G4_Ir
  specific = 4
FEATURE [App::DocumentObjectGroupPython] Pt_element001  label="Pt_element : 1"  # scripted group (container) (typed FeaturePython)
  n = 1
  ref = Pt_element
FEATURE [App::DocumentObjectGroupPython] G4_Pt  # scripted group (container) (typed FeaturePython)
  Dunit = g/cm3
  Dvalue = 21.45
  Group = -> [Pt_element001]
  conduct = 2
  density = 1
  expand = 3
  formula = Pt
  name = G4_Pt
  specific = 4
FEATURE [App::DocumentObjectGroupPython] Au_element001  label="Au_element : 1"  # scripted group (container) (typed FeaturePython)
  n = 1
  ref = Au_element
FEATURE [App::DocumentObjectGroupPython] G4_Au  # scripted group (container) (typed FeaturePython)
  Dunit = g/cm3
  Dvalue = 19.32
  Group = -> [Au_element001]
  conduct = 2
  density = 1
  expand = 3
  formula = Au
  name = G4_Au
  specific = 4
FEATURE [App::DocumentObjectGroupPython] Hg_element002  label="Hg_element : 002"  # scripted group (container) (typed FeaturePython)
  n = 1
  ref = Hg_element
FEATURE [App::DocumentObjectGroupPython] G4_Hg  # scripted group (container) (typed FeaturePython)
  Dunit = g/cm3
  Dvalue = 13.546
  Group = -> [Hg_element002]
  conduct = 2
  density = 1
  expand = 3
  formula = Hg
  name = G4_Hg
  specific = 4
FEATURE [App::DocumentObjectGroupPython] Tl_element002  label="Tl_element : 002"  # scripted group (container) (typed FeaturePython)
  n = 1
  ref = Tl_element
FEATURE [App::DocumentObjectGroupPython] G4_Tl  # scripted group (container) (typed FeaturePython)
  Dunit = g/cm3
  Dvalue = 11.72
  Group = -> [Tl_element002]
  conduct = 2
  density = 1
  expand = 3
  formula = Tl
  name = G4_Tl
  specific = 4
FEATURE [App::DocumentObjectGroupPython] Pb_element003  label="Pb_element : 1"  # scripted group (container) (typed FeaturePython)
  n = 1
  ref = Pb_element
FEATURE [App::DocumentObjectGroupPython] G4_Pb  # scripted group (container) (typed FeaturePython)
  Dunit = g/cm3
  Dvalue = 11.35
  Group = -> [Pb_element003]
  conduct = 2
  density = 1
  expand = 3
  formula = Pb
  name = G4_Pb
  specific = 4
FEATURE [App::DocumentObjectGroupPython] Bi_element002  label="Bi_element : 1"  # scripted group (container) (typed FeaturePython)
  n = 1
  ref = Bi_element
FEATURE [App::DocumentObjectGroupPython] G4_Bi  # scripted group (container) (typed FeaturePython)
  Dunit = g/cm3
  Dvalue = 9.747
  Group = -> [Bi_element002]
  conduct = 2
  density = 1
  expand = 3
  formula = Bi
  name = G4_Bi
  specific = 4
FEATURE [App::DocumentObjectGroupPython] Po_element001  label="Po_element : 1"  # scripted group (container) (typed FeaturePython)
  n = 1
  ref = Po_element
FEATURE [App::DocumentObjectGroupPython] G4_Po  # scripted group (container) (typed FeaturePython)
  Dunit = g/cm3
  Dvalue = 9.32
  Group = -> [Po_element001]
  conduct = 2
  density = 1
  expand = 3
  formula = Po
  name = G4_Po
  specific = 4
FEATURE [App::DocumentObjectGroupPython] At_element001  label="At_element : 1"  # scripted group (container) (typed FeaturePython)
  n = 1
  ref = At_element
FEATURE [App::DocumentObjectGroupPython] G4_At  # scripted group (container) (typed FeaturePython)
  Dunit = g/cm3
  Dvalue = 9.32
  Group = -> [At_element001]
  conduct = 2
  density = 1
  expand = 3
  formula = At
  name = G4_At
  specific = 4
FEATURE [App::DocumentObjectGroupPython] Rn_element001  label="Rn_element : 1"  # scripted group (container) (typed FeaturePython)
  n = 1
  ref = Rn_element
FEATURE [App::DocumentObjectGroupPython] G4_Rn  # scripted group (container) (typed FeaturePython)
  Dunit = g/cm3
  Dvalue = 0.00900662
  Group = -> [Rn_element001]
  conduct = 2
  density = 1
  expand = 3
  formula = Rn
  name = G4_Rn
  specific = 4
FEATURE [App::DocumentObjectGroupPython] Fr_element001  label="Fr_element : 1"  # scripted group (container) (typed FeaturePython)
  n = 1
  ref = Fr_element
FEATURE [App::DocumentObjectGroupPython] G4_Fr  # scripted group (container) (typed FeaturePython)
  Dunit = g/cm3
  Dvalue = 1
  Group = -> [Fr_element001]
  conduct = 2
  density = 1
  expand = 3
  formula = Fr
  name = G4_Fr
  specific = 4
FEATURE [App::DocumentObjectGroupPython] Ra_element001  label="Ra_element : 1"  # scripted group (container) (typed FeaturePython)
  n = 1
  ref = Ra_element
FEATURE [App::DocumentObjectGroupPython] G4_Ra  # scripted group (container) (typed FeaturePython)
  Dunit = g/cm3
  Dvalue = 5
  Group = -> [Ra_element001]
  conduct = 2
  density = 1
  expand = 3
  formula = Ra
  name = G4_Ra
  specific = 4
FEATURE [App::DocumentObjectGroupPython] Ac_element001  label="Ac_element : 1"  # scripted group (container) (typed FeaturePython)
  n = 1
  ref = Ac_element
FEATURE [App::DocumentObjectGroupPython] G4_Ac  # scripted group (container) (typed FeaturePython)
  Dunit = g/cm3
  Dvalue = 10.07
  Group = -> [Ac_element001]
  conduct = 2
  density = 1
  expand = 3
  formula = Ac
  name = G4_Ac
  specific = 4
FEATURE [App::DocumentObjectGroupPython] Th_element001  label="Th_element : 1"  # scripted group (container) (typed FeaturePython)
  n = 1
  ref = Th_element
FEATURE [App::DocumentObjectGroupPython] G4_Th  # scripted group (container) (typed FeaturePython)
  Dunit = g/cm3
  Dvalue = 11.72
  Group = -> [Th_element001]
  conduct = 2
  density = 1
  expand = 3
  formula = Th
  name = G4_Th
  specific = 4
FEATURE [App::DocumentObjectGroupPython] Pa_element001  label="Pa_element : 1"  # scripted group (container) (typed FeaturePython)
  n = 1
  ref = Pa_element
FEATURE [App::DocumentObjectGroupPython] G4_Pa  # scripted group (container) (typed FeaturePython)
  Dunit = g/cm3
  Dvalue = 15.37
  Group = -> [Pa_element001]
  conduct = 2
  density = 1
  expand = 3
  formula = Pa
  name = G4_Pa
  specific = 4
FEATURE [App::DocumentObjectGroupPython] U_element004  label="U_element : 004"  # scripted group (container) (typed FeaturePython)
  n = 1
  ref = U_element
FEATURE [App::DocumentObjectGroupPython] G4_U  # scripted group (container) (typed FeaturePython)
  Dunit = g/cm3
  Dvalue = 18.95
  Group = -> [U_element004]
  conduct = 2
  density = 1
  expand = 3
  formula = U
  name = G4_U
  specific = 4
FEATURE [App::DocumentObjectGroupPython] Np_element001  label="Np_element : 1"  # scripted group (container) (typed FeaturePython)
  n = 1
  ref = Np_element
FEATURE [App::DocumentObjectGroupPython] G4_Np  # scripted group (container) (typed FeaturePython)
  Dunit = g/cm3
  Dvalue = 20.25
  Group = -> [Np_element001]
  conduct = 2
  density = 1
  expand = 3
  formula = Np
  name = G4_Np
  specific = 4
FEATURE [App::DocumentObjectGroupPython] Pu_element002  label="Pu_element : 002"  # scripted group (container) (typed FeaturePython)
  n = 1
  ref = Pu_element
FEATURE [App::DocumentObjectGroupPython] G4_Pu  # scripted group (container) (typed FeaturePython)
  Dunit = g/cm3
  Dvalue = 19.84
  Group = -> [Pu_element002]
  conduct = 2
  density = 1
  expand = 3
  formula = Pu
  name = G4_Pu
  specific = 4
FEATURE [App::DocumentObjectGroupPython] Am_element001  label="Am_element : 1"  # scripted group (container) (typed FeaturePython)
  n = 1
  ref = Am_element
FEATURE [App::DocumentObjectGroupPython] G4_Am  # scripted group (container) (typed FeaturePython)
  Dunit = g/cm3
  Dvalue = 13.67
  Group = -> [Am_element001]
  conduct = 2
  density = 1
  expand = 3
  formula = Am
  name = G4_Am
  specific = 4
FEATURE [App::DocumentObjectGroupPython] Cm_element001  label="Cm_element : 1"  # scripted group (container) (typed FeaturePython)
  n = 1
  ref = Cm_element
FEATURE [App::DocumentObjectGroupPython] G4_Cm  # scripted group (container) (typed FeaturePython)
  Dunit = g/cm3
  Dvalue = 13.51
  Group = -> [Cm_element001]
  conduct = 2
  density = 1
  expand = 3
  formula = Cm
  name = G4_Cm
  specific = 4
FEATURE [App::DocumentObjectGroupPython] Bk_element001  label="Bk_element : 1"  # scripted group (container) (typed FeaturePython)
  n = 1
  ref = Bk_element
FEATURE [App::DocumentObjectGroupPython] G4_Bk  # scripted group (container) (typed FeaturePython)
  Dunit = g/cm3
  Dvalue = 14
  Group = -> [Bk_element001]
  conduct = 2
  density = 1
  expand = 3
  formula = Bk
  name = G4_Bk
  specific = 4
FEATURE [App::DocumentObjectGroupPython] Cf_element001  label="Cf_element : 1"  # scripted group (container) (typed FeaturePython)
  n = 1
  ref = Cf_element
FEATURE [App::DocumentObjectGroupPython] G4_Cf  # scripted group (container) (typed FeaturePython)
  Dunit = g/cm3
  Dvalue = 10
  Group = -> [Cf_element001]
  conduct = 2
  density = 1
  expand = 3
  formula = Cf
  name = G4_Cf
  specific = 4
FEATURE [App::DocumentObjectGroupPython] Element  # scripted group (container) (typed FeaturePython)
  Group = -> [G4_H,G4_He,G4_Li,G4_Be,G4_B,G4_C,G4_N,G4_O,G4_F,G4_Ne,G4_Na,G4_Mg,G4_Al,G4_Si,G4_P,G4_S,G4_Cl,G4_Ar,G4_K,G4_Ca,G4_Sc,G4_Ti,G4_V,G4_Cr,G4_Mn,G4_Fe,G4_Co,G4_Ni,G4_Cu,G4_Zn,G4_Ga,G4_Ge,G4_As,G4_Se,G4_Br,G4_Kr,G4_Rb,G4_Sr,G4_Y,G4_Zr,G4_Nb,G4_Mo,G4_Tc,G4_Ru,G4_Rh,G4_Pd,G4_Ag,G4_Cd,G4_In,G4_Sn,G4_Sb,G4_Te,G4_I,G4_Xe,G4_Cs,G4_Ba,G4_La,G4_Ce,G4_Pr,G4_Nd,G4_Pm,G4_Sm,G4_Eu,G4_Gd,G4_Tb,G4_Dy,G4_Ho,G4_Er,+30 more]
FEATURE [App::DocumentObjectGroupPython] H_element114  label="H_element : 063"  # scripted group (container) (typed FeaturePython)
  n = 2
  ref = H_element
FEATURE [App::DocumentObjectGroupPython] G4_lH2  # scripted group (container) (typed FeaturePython)
  Dunit = g/cm3
  Dvalue = 0.0708
  Group = -> [H_element114]
  conduct = 2
  density = 1
  expand = 3
  formula = G4_lH2
  name = G4_lH2
  specific = 4
FEATURE [App::DocumentObjectGroupPython] N_element049  label="N_element : 022"  # scripted group (container) (typed FeaturePython)
  n = 2
  ref = N_element
FEATURE [App::DocumentObjectGroupPython] G4_lN2  # scripted group (container) (typed FeaturePython)
  Dunit = g/cm3
  Dvalue = 0.807
  Group = -> [N_element049]
  conduct = 2
  density = 1
  expand = 3
  formula = G4_lN2
  name = G4_lN2
  specific = 4
FEATURE [App::DocumentObjectGroupPython] O_element106  label="O_element : 060"  # scripted group (container) (typed FeaturePython)
  n = 2
  ref = O_element
FEATURE [App::DocumentObjectGroupPython] G4_lO2  # scripted group (container) (typed FeaturePython)
  Dunit = g/cm3
  Dvalue = 1.141
  Group = -> [O_element106]
  conduct = 2
  density = 1
  expand = 3
  formula = G4_lO2
  name = G4_lO2
  specific = 4
FEATURE [App::DocumentObjectGroupPython] Ar  label="Ar : 1"  # scripted group (container) (typed FeaturePython)
  n = 1
  ref = Ar
FEATURE [App::DocumentObjectGroupPython] G4_lAr  # scripted group (container) (typed FeaturePython)
  Dunit = g/cm3
  Dvalue = 1.396
  Group = -> [Ar]
  conduct = 2
  density = 1
  expand = 3
  formula = G4_lAr
  name = G4_lAr
  specific = 4
FEATURE [App::DocumentObjectGroupPython] Br  label="Br : 1"  # scripted group (container) (typed FeaturePython)
  n = 1
  ref = Br
FEATURE [App::DocumentObjectGroupPython] G4_lBr  # scripted group (container) (typed FeaturePython)
  Dunit = g/cm3
  Dvalue = 3.1028
  Group = -> [Br]
  conduct = 2
  density = 1
  expand = 3
  formula = G4_lBr
  name = G4_lBr
  specific = 4
FEATURE [App::DocumentObjectGroupPython] Kr  label="Kr : 1"  # scripted group (container) (typed FeaturePython)
  n = 1
  ref = Kr
FEATURE [App::DocumentObjectGroupPython] G4_lKr  # scripted group (container) (typed FeaturePython)
  Dunit = g/cm3
  Dvalue = 2.418
  Group = -> [Kr]
  conduct = 2
  density = 1
  expand = 3
  formula = G4_lKr
  name = G4_lKr
  specific = 4
FEATURE [App::DocumentObjectGroupPython] Xe  label="Xe : 1"  # scripted group (container) (typed FeaturePython)
  n = 1
  ref = Xe
FEATURE [App::DocumentObjectGroupPython] G4_lXe  # scripted group (container) (typed FeaturePython)
  Dunit = g/cm3
  Dvalue = 2.953
  Group = -> [Xe]
  conduct = 2
  density = 1
  expand = 3
  formula = G4_lXe
  name = G4_lXe
  specific = 4
FEATURE [App::DocumentObjectGroupPython] O_element107  label="O_element : 061"  # scripted group (container) (typed FeaturePython)
  n = 4
  ref = O_element
FEATURE [App::DocumentObjectGroupPython] Pb_element004  label="Pb_element : 002"  # scripted group (container) (typed FeaturePython)
  n = 1
  ref = Pb_element
FEATURE [App::DocumentObjectGroupPython] W_element005  label="W_element : 005"  # scripted group (container) (typed FeaturePython)
  n = 1
  ref = W_element
FEATURE [App::DocumentObjectGroupPython] G4_PbWO4  # scripted group (container) (typed FeaturePython)
  Dunit = g/cm3
  Dvalue = 8.28
  Group = -> [O_element107,Pb_element004,W_element005]
  conduct = 2
  density = 1
  expand = 3
  formula = G4_PbWO4
  name = G4_PbWO4
  specific = 4
FEATURE [App::DocumentObjectGroupPython] alactic  label="alactic : 1"  # scripted group (container) (typed FeaturePython)
  n = 1
  ref = alactic
FEATURE [App::DocumentObjectGroupPython] G4_Galactic  # scripted group (container) (typed FeaturePython)
  Dunit = g/cm3
  Dvalue = 0
  Group = -> [alactic]
  conduct = 2
  density = 1
  expand = 3
  formula = G4_Galactic
  name = G4_Galactic
  specific = 4
FEATURE [App::DocumentObjectGroupPython] RAPHITE_POROUS  label="RAPHITE_POROUS : 1"  # scripted group (container) (typed FeaturePython)
  n = 1
  ref = RAPHITE_POROUS
FEATURE [App::DocumentObjectGroupPython] G4_GRAPHITE_POROUS  # scripted group (container) (typed FeaturePython)
  Dunit = g/cm3
  Dvalue = 1.7
  Group = -> [RAPHITE_POROUS]
  conduct = 2
  density = 1
  expand = 3
  formula = G4_GRAPHITE_POROUS
  name = G4_GRAPHITE_POROUS
  specific = 4
FEATURE [App::DocumentObjectGroupPython] H_element115  label="H_element : 0.150"  # scripted group (container) (typed FeaturePython)
  n = 0.080538
FEATURE [App::DocumentObjectGroupPython] C_element125  label="C_element : 0.600"  # scripted group (container) (typed FeaturePython)
  n = 0.599848
FEATURE [App::DocumentObjectGroupPython] O_element108  label="O_element : 0.320"  # scripted group (container) (typed FeaturePython)
  n = 0.319614
FEATURE [App::DocumentObjectGroupPython] G4_LUCITE  # scripted group (container) (typed FeaturePython)
  Dunit = g/cm3
  Dvalue = 1.19
  Group = -> [H_element115,C_element125,O_element108]
  conduct = 2
  density = 1
  expand = 3
  formula = G4_LUCITE
  name = G4_LUCITE
  specific = 4
FEATURE [App::DocumentObjectGroupPython] Cu_element002  label="Cu_element : 62"  # scripted group (container) (typed FeaturePython)
  n = 62
  ref = Cu_element
FEATURE [App::DocumentObjectGroupPython] Zn_element002  label="Zn_element : 35"  # scripted group (container) (typed FeaturePython)
  n = 35
  ref = Zn_element
FEATURE [App::DocumentObjectGroupPython] Pb_element005  label="Pb_element : 3"  # scripted group (container) (typed FeaturePython)
  n = 3
  ref = Pb_element
FEATURE [App::DocumentObjectGroupPython] G4_BRASS  # scripted group (container) (typed FeaturePython)
  Dunit = g/cm3
  Dvalue = 8.52
  Group = -> [Cu_element002,Zn_element002,Pb_element005]
  conduct = 2
  density = 1
  expand = 3
  formula = G4_BRASS
  name = G4_BRASS
  specific = 4
FEATURE [App::DocumentObjectGroupPython] Cu_element003  label="Cu_element : 89"  # scripted group (container) (typed FeaturePython)
  n = 89
  ref = Cu_element
FEATURE [App::DocumentObjectGroupPython] Zn_element003  label="Zn_element : 9"  # scripted group (container) (typed FeaturePython)
  n = 9
  ref = Zn_element
FEATURE [App::DocumentObjectGroupPython] Pb_element006  label="Pb_element : 2"  # scripted group (container) (typed FeaturePython)
  n = 2
  ref = Pb_element
FEATURE [App::DocumentObjectGroupPython] G4_BRONZE  # scripted group (container) (typed FeaturePython)
  Dunit = g/cm3
  Dvalue = 8.82
  Group = -> [Cu_element003,Zn_element003,Pb_element006]
  conduct = 2
  density = 1
  expand = 3
  formula = G4_BRONZE
  name = G4_BRONZE
  specific = 4
FEATURE [App::DocumentObjectGroupPython] Fe_element008  label="Fe_element : 74"  # scripted group (container) (typed FeaturePython)
  n = 74
  ref = Fe_element
FEATURE [App::DocumentObjectGroupPython] Cr_element002  label="Cr_element : 18"  # scripted group (container) (typed FeaturePython)
  n = 18
  ref = Cr_element
FEATURE [App::DocumentObjectGroupPython] Ni_element002  label="Ni_element : 8"  # scripted group (container) (typed FeaturePython)
  n = 8
  ref = Ni_element
FEATURE [App::DocumentObjectGroupPython] G4_STAINLESS_STEEL  label="G4_STAINLESS-STEEL"  # scripted group (container) (typed FeaturePython)
  Dunit = g/cm3
  Dvalue = 8
  Group = -> [Fe_element008,Cr_element002,Ni_element002]
  conduct = 2
  density = 1
  expand = 3
  formula = G4_STAINLESS-STEEL
  name = G4_STAINLESS-STEEL
  specific = 4
FEATURE [App::DocumentObjectGroupPython] H_element116  label="H_element : 064"  # scripted group (container) (typed FeaturePython)
  n = 18
  ref = H_element
FEATURE [App::DocumentObjectGroupPython] C_element126  label="C_element : 071"  # scripted group (container) (typed FeaturePython)
  n = 12
  ref = C_element
FEATURE [App::DocumentObjectGroupPython] O_element109  label="O_element : 062"  # scripted group (container) (typed FeaturePython)
  n = 7
  ref = O_element
FEATURE [App::DocumentObjectGroupPython] G4_CR39  # scripted group (container) (typed FeaturePython)
  Dunit = g/cm3
  Dvalue = 1.32
  Group = -> [H_element116,C_element126,O_element109]
  conduct = 2
  density = 1
  expand = 3
  formula = G4_CR39
  name = G4_CR39
  specific = 4
FEATURE [App::DocumentObjectGroupPython] H_element117  label="H_element : 38"  # scripted group (container) (typed FeaturePython)
  n = 38
  ref = H_element
FEATURE [App::DocumentObjectGroupPython] C_element127  label="C_element : 072"  # scripted group (container) (typed FeaturePython)
  n = 18
  ref = C_element
FEATURE [App::DocumentObjectGroupPython] O_element110  label="O_element : 063"  # scripted group (container) (typed FeaturePython)
  n = 1
  ref = O_element
FEATURE [App::DocumentObjectGroupPython] G4_OCTADECANOL  # scripted group (container) (typed FeaturePython)
  Dunit = g/cm3
  Dvalue = 0.812
  Group = -> [H_element117,C_element127,O_element110]
  conduct = 2
  density = 1
  expand = 3
  formula = G4_OCTADECANOL
  name = G4_OCTADECANOL
  specific = 4
FEATURE [App::DocumentObjectGroupPython] HEP  # scripted group (container) (typed FeaturePython)
  Group = -> [G4_lH2,G4_lN2,G4_lO2,G4_lAr,G4_lBr,G4_lKr,G4_lXe,G4_PbWO4,G4_Galactic,G4_GRAPHITE_POROUS,G4_LUCITE,G4_BRASS,G4_BRONZE,G4_STAINLESS_STEEL,G4_CR39,G4_OCTADECANOL]
FEATURE [App::DocumentObjectGroupPython] C_element128  label="C_element : 073"  # scripted group (container) (typed FeaturePython)
  n = 14
  ref = C_element
FEATURE [App::DocumentObjectGroupPython] H_element118  label="H_element : 065"  # scripted group (container) (typed FeaturePython)
  n = 10
  ref = H_element
FEATURE [App::DocumentObjectGroupPython] O_element111  label="O_element : 064"  # scripted group (container) (typed FeaturePython)
  n = 2
  ref = O_element
FEATURE [App::DocumentObjectGroupPython] N_element050  label="N_element : 023"  # scripted group (container) (typed FeaturePython)
  n = 2
  ref = N_element
FEATURE [App::DocumentObjectGroupPython] G4_KEVLAR  # scripted group (container) (typed FeaturePython)
  Dunit = g/cm3
  Dvalue = 1.44
  Group = -> [C_element128,H_element118,O_element111,N_element050]
  conduct = 2
  density = 1
  expand = 3
  formula = G4_KEVLAR
  name = G4_KEVLAR
  specific = 4
FEATURE [App::DocumentObjectGroupPython] C_element129  label="C_element : 074"  # scripted group (container) (typed FeaturePython)
  n = 10
  ref = C_element
FEATURE [App::DocumentObjectGroupPython] H_element119  label="H_element : 066"  # scripted group (container) (typed FeaturePython)
  n = 8
  ref = H_element
FEATURE [App::DocumentObjectGroupPython] O_element112  label="O_element : 065"  # scripted group (container) (typed FeaturePython)
  n = 4
  ref = O_element
FEATURE [App::DocumentObjectGroupPython] G4_DACRON  # scripted group (container) (typed FeaturePython)
  Dunit = g/cm3
  Dvalue = 1.4
  Group = -> [C_element129,H_element119,O_element112]
  conduct = 2
  density = 1
  expand = 3
  formula = G4_DACRON
  name = G4_DACRON
  specific = 4
FEATURE [App::DocumentObjectGroupPython] C_element130  label="C_element : 075"  # scripted group (container) (typed FeaturePython)
  n = 4
  ref = C_element
FEATURE [App::DocumentObjectGroupPython] H_element120  label="H_element : 067"  # scripted group (container) (typed FeaturePython)
  n = 5
  ref = H_element
FEATURE [App::DocumentObjectGroupPython] Cl_element030  label="Cl_element : 016"  # scripted group (container) (typed FeaturePython)
  n = 1
  ref = Cl_element
FEATURE [App::DocumentObjectGroupPython] G4_NEOPRENE  # scripted group (container) (typed FeaturePython)
  Dunit = g/cm3
  Dvalue = 1.23
  Group = -> [C_element130,H_element120,Cl_element030]
  conduct = 2
  density = 1
  expand = 3
  formula = G4_NEOPRENE
  name = G4_NEOPRENE
  specific = 4
FEATURE [App::DocumentObjectGroupPython] Space  # scripted group (container) (typed FeaturePython)
  Group = -> [G4_KEVLAR,G4_DACRON,G4_NEOPRENE]
FEATURE [App::DocumentObjectGroupPython] H_element121  label="H_element : 068"  # scripted group (container) (typed FeaturePython)
  n = 5
  ref = H_element
FEATURE [App::DocumentObjectGroupPython] C_element131  label="C_element : 076"  # scripted group (container) (typed FeaturePython)
  n = 4
  ref = C_element
FEATURE [App::DocumentObjectGroupPython] N_element051  label="N_element : 3"  # scripted group (container) (typed FeaturePython)
  n = 3
  ref = N_element
FEATURE [App::DocumentObjectGroupPython] O_element113  label="O_element : 066"  # scripted group (container) (typed FeaturePython)
  n = 1
  ref = O_element
FEATURE [App::DocumentObjectGroupPython] G4_CYTOSINE  # scripted group (container) (typed FeaturePython)
  Dunit = g/cm3
  Dvalue = 1.55
  Group = -> [H_element121,C_element131,N_element051,O_element113]
  conduct = 2
  density = 1
  expand = 3
  formula = G4_CYTOSINE
  name = G4_CYTOSINE
  specific = 4
FEATURE [App::DocumentObjectGroupPython] H_element122  label="H_element : 069"  # scripted group (container) (typed FeaturePython)
  n = 6
  ref = H_element
FEATURE [App::DocumentObjectGroupPython] C_element132  label="C_element : 077"  # scripted group (container) (typed FeaturePython)
  n = 5
  ref = C_element
FEATURE [App::DocumentObjectGroupPython] N_element052  label="N_element : 024"  # scripted group (container) (typed FeaturePython)
  n = 2
  ref = N_element
FEATURE [App::DocumentObjectGroupPython] O_element114  label="O_element : 067"  # scripted group (container) (typed FeaturePython)
  n = 2
  ref = O_element
FEATURE [App::DocumentObjectGroupPython] G4_THYMINE  # scripted group (container) (typed FeaturePython)
  Dunit = g/cm3
  Dvalue = 1.23
  Group = -> [H_element122,C_element132,N_element052,O_element114]
  conduct = 2
  density = 1
  expand = 3
  formula = G4_THYMINE
  name = G4_THYMINE
  specific = 4
FEATURE [App::DocumentObjectGroupPython] H_element123  label="H_element : 070"  # scripted group (container) (typed FeaturePython)
  n = 4
  ref = H_element
FEATURE [App::DocumentObjectGroupPython] C_element133  label="C_element : 078"  # scripted group (container) (typed FeaturePython)
  n = 4
  ref = C_element
FEATURE [App::DocumentObjectGroupPython] N_element053  label="N_element : 025"  # scripted group (container) (typed FeaturePython)
  n = 2
  ref = N_element
FEATURE [App::DocumentObjectGroupPython] O_element115  label="O_element : 068"  # scripted group (container) (typed FeaturePython)
  n = 2
  ref = O_element
FEATURE [App::DocumentObjectGroupPython] G4_URACIL  # scripted group (container) (typed FeaturePython)
  Dunit = g/cm3
  Dvalue = 1.32
  Group = -> [H_element123,C_element133,N_element053,O_element115]
  conduct = 2
  density = 1
  expand = 3
  formula = G4_URACIL
  name = G4_URACIL
  specific = 4
FEATURE [App::DocumentObjectGroupPython] H_element124  label="H_element : 071"  # scripted group (container) (typed FeaturePython)
  n = 4
  ref = H_element
FEATURE [App::DocumentObjectGroupPython] C_element134  label="C_element : 079"  # scripted group (container) (typed FeaturePython)
  n = 5
  ref = C_element
FEATURE [App::DocumentObjectGroupPython] N_element054  label="N_element : 026"  # scripted group (container) (typed FeaturePython)
  n = 5
  ref = N_element
FEATURE [App::DocumentObjectGroupPython] G4_DNA_ADENINE  # scripted group (container) (typed FeaturePython)
  Dunit = g/cm3
  Dvalue = 1
  Group = -> [H_element124,C_element134,N_element054]
  conduct = 2
  density = 1
  expand = 3
  formula = G4_DNA_ADENINE
  name = G4_DNA_ADENINE
  specific = 4
FEATURE [App::DocumentObjectGroupPython] H_element125  label="H_element : 072"  # scripted group (container) (typed FeaturePython)
  n = 4
  ref = H_element
FEATURE [App::DocumentObjectGroupPython] C_element135  label="C_element : 080"  # scripted group (container) (typed FeaturePython)
  n = 5
  ref = C_element
FEATURE [App::DocumentObjectGroupPython] N_element055  label="N_element : 027"  # scripted group (container) (typed FeaturePython)
  n = 5
  ref = N_element
FEATURE [App::DocumentObjectGroupPython] O_element116  label="O_element : 069"  # scripted group (container) (typed FeaturePython)
  n = 1
  ref = O_element
FEATURE [App::DocumentObjectGroupPython] G4_DNA_GUANINE  # scripted group (container) (typed FeaturePython)
  Dunit = g/cm3
  Dvalue = 1
  Group = -> [H_element125,C_element135,N_element055,O_element116]
  conduct = 2
  density = 1
  expand = 3
  formula = G4_DNA_GUANINE
  name = G4_DNA_GUANINE
  specific = 4
FEATURE [App::DocumentObjectGroupPython] H_element126  label="H_element : 073"  # scripted group (container) (typed FeaturePython)
  n = 4
  ref = H_element
FEATURE [App::DocumentObjectGroupPython] C_element136  label="C_element : 081"  # scripted group (container) (typed FeaturePython)
  n = 4
  ref = C_element
FEATURE [App::DocumentObjectGroupPython] N_element056  label="N_element : 028"  # scripted group (container) (typed FeaturePython)
  n = 3
  ref = N_element
FEATURE [App::DocumentObjectGroupPython] O_element117  label="O_element : 070"  # scripted group (container) (typed FeaturePython)
  n = 1
  ref = O_element
FEATURE [App::DocumentObjectGroupPython] G4_DNA_CYTOSINE  # scripted group (container) (typed FeaturePython)
  Dunit = g/cm3
  Dvalue = 1
  Group = -> [H_element126,C_element136,N_element056,O_element117]
  conduct = 2
  density = 1
  expand = 3
  formula = G4_DNA_CYTOSINE
  name = G4_DNA_CYTOSINE
  specific = 4
FEATURE [App::DocumentObjectGroupPython] H_element127  label="H_element : 074"  # scripted group (container) (typed FeaturePython)
  n = 5
  ref = H_element
FEATURE [App::DocumentObjectGroupPython] C_element137  label="C_element : 082"  # scripted group (container) (typed FeaturePython)
  n = 5
  ref = C_element
FEATURE [App::DocumentObjectGroupPython] N_element057  label="N_element : 029"  # scripted group (container) (typed FeaturePython)
  n = 2
  ref = N_element
FEATURE [App::DocumentObjectGroupPython] O_element118  label="O_element : 071"  # scripted group (container) (typed FeaturePython)
  n = 2
  ref = O_element
FEATURE [App::DocumentObjectGroupPython] G4_DNA_THYMINE  # scripted group (container) (typed FeaturePython)
  Dunit = g/cm3
  Dvalue = 1
  Group = -> [H_element127,C_element137,N_element057,O_element118]
  conduct = 2
  density = 1
  expand = 3
  formula = G4_DNA_THYMINE
  name = G4_DNA_THYMINE
  specific = 4
FEATURE [App::DocumentObjectGroupPython] H_element128  label="H_element : 075"  # scripted group (container) (typed FeaturePython)
  n = 3
  ref = H_element
FEATURE [App::DocumentObjectGroupPython] C_element138  label="C_element : 083"  # scripted group (container) (typed FeaturePython)
  n = 4
  ref = C_element
FEATURE [App::DocumentObjectGroupPython] N_element058  label="N_element : 030"  # scripted group (container) (typed FeaturePython)
  n = 2
  ref = N_element
FEATURE [App::DocumentObjectGroupPython] O_element119  label="O_element : 072"  # scripted group (container) (typed FeaturePython)
  n = 2
  ref = O_element
FEATURE [App::DocumentObjectGroupPython] G4_DNA_URACIL  # scripted group (container) (typed FeaturePython)
  Dunit = g/cm3
  Dvalue = 1
  Group = -> [H_element128,C_element138,N_element058,O_element119]
  conduct = 2
  density = 1
  expand = 3
  formula = G4_DNA_URACIL
  name = G4_DNA_URACIL
  specific = 4
FEATURE [App::DocumentObjectGroupPython] H_element129  label="H_element : 076"  # scripted group (container) (typed FeaturePython)
  n = 10
  ref = H_element
FEATURE [App::DocumentObjectGroupPython] C_element139  label="C_element : 084"  # scripted group (container) (typed FeaturePython)
  n = 10
  ref = C_element
FEATURE [App::DocumentObjectGroupPython] N_element059  label="N_element : 031"  # scripted group (container) (typed FeaturePython)
  n = 5
  ref = N_element
FEATURE [App::DocumentObjectGroupPython] O_element120  label="O_element : 073"  # scripted group (container) (typed FeaturePython)
  n = 4
  ref = O_element
FEATURE [App::DocumentObjectGroupPython] G4_DNA_ADENOSINE  # scripted group (container) (typed FeaturePython)
  Dunit = g/cm3
  Dvalue = 1
  Group = -> [H_element129,C_element139,N_element059,O_element120]
  conduct = 2
  density = 1
  expand = 3
  formula = G4_DNA_ADENOSINE
  name = G4_DNA_ADENOSINE
  specific = 4
FEATURE [App::DocumentObjectGroupPython] H_element130  label="H_element : 077"  # scripted group (container) (typed FeaturePython)
  n = 10
  ref = H_element
FEATURE [App::DocumentObjectGroupPython] C_element140  label="C_element : 085"  # scripted group (container) (typed FeaturePython)
  n = 10
  ref = C_element
FEATURE [App::DocumentObjectGroupPython] N_element060  label="N_element : 032"  # scripted group (container) (typed FeaturePython)
  n = 5
  ref = N_element
FEATURE [App::DocumentObjectGroupPython] O_element121  label="O_element : 074"  # scripted group (container) (typed FeaturePython)
  n = 5
  ref = O_element
FEATURE [App::DocumentObjectGroupPython] G4_DNA_GUANOSINE  # scripted group (container) (typed FeaturePython)
  Dunit = g/cm3
  Dvalue = 1
  Group = -> [H_element130,C_element140,N_element060,O_element121]
  conduct = 2
  density = 1
  expand = 3
  formula = G4_DNA_GUANOSINE
  name = G4_DNA_GUANOSINE
  specific = 4
FEATURE [App::DocumentObjectGroupPython] H_element131  label="H_element : 078"  # scripted group (container) (typed FeaturePython)
  n = 10
  ref = H_element
FEATURE [App::DocumentObjectGroupPython] C_element141  label="C_element : 086"  # scripted group (container) (typed FeaturePython)
  n = 9
  ref = C_element
FEATURE [App::DocumentObjectGroupPython] N_element061  label="N_element : 033"  # scripted group (container) (typed FeaturePython)
  n = 3
  ref = N_element
FEATURE [App::DocumentObjectGroupPython] O_element122  label="O_element : 075"  # scripted group (container) (typed FeaturePython)
  n = 5
  ref = O_element
FEATURE [App::DocumentObjectGroupPython] G4_DNA_CYTIDINE  # scripted group (container) (typed FeaturePython)
  Dunit = g/cm3
  Dvalue = 1
  Group = -> [H_element131,C_element141,N_element061,O_element122]
  conduct = 2
  density = 1
  expand = 3
  formula = G4_DNA_CYTIDINE
  name = G4_DNA_CYTIDINE
  specific = 4
FEATURE [App::DocumentObjectGroupPython] H_element132  label="H_element : 079"  # scripted group (container) (typed FeaturePython)
  n = 9
  ref = H_element
FEATURE [App::DocumentObjectGroupPython] C_element142  label="C_element : 087"  # scripted group (container) (typed FeaturePython)
  n = 9
  ref = C_element
FEATURE [App::DocumentObjectGroupPython] N_element062  label="N_element : 034"  # scripted group (container) (typed FeaturePython)
  n = 2
  ref = N_element
FEATURE [App::DocumentObjectGroupPython] O_element123  label="O_element : 076"  # scripted group (container) (typed FeaturePython)
  n = 6
  ref = O_element
FEATURE [App::DocumentObjectGroupPython] G4_DNA_URIDINE  # scripted group (container) (typed FeaturePython)
  Dunit = g/cm3
  Dvalue = 1
  Group = -> [H_element132,C_element142,N_element062,O_element123]
  conduct = 2
  density = 1
  expand = 3
  formula = G4_DNA_URIDINE
  name = G4_DNA_URIDINE
  specific = 4
FEATURE [App::DocumentObjectGroupPython] H_element133  label="H_element : 080"  # scripted group (container) (typed FeaturePython)
  n = 11
  ref = H_element
FEATURE [App::DocumentObjectGroupPython] C_element143  label="C_element : 088"  # scripted group (container) (typed FeaturePython)
  n = 10
  ref = C_element
FEATURE [App::DocumentObjectGroupPython] N_element063  label="N_element : 035"  # scripted group (container) (typed FeaturePython)
  n = 2
  ref = N_element
FEATURE [App::DocumentObjectGroupPython] O_element124  label="O_element : 077"  # scripted group (container) (typed FeaturePython)
  n = 6
  ref = O_element
FEATURE [App::DocumentObjectGroupPython] G4_DNA_METHYLURIDINE  # scripted group (container) (typed FeaturePython)
  Dunit = g/cm3
  Dvalue = 1
  Group = -> [H_element133,C_element143,N_element063,O_element124]
  conduct = 2
  density = 1
  expand = 3
  formula = G4_DNA_METHYLURIDINE
  name = G4_DNA_METHYLURIDINE
  specific = 4
FEATURE [App::DocumentObjectGroupPython] P_element014  label="P_element : 003"  # scripted group (container) (typed FeaturePython)
  n = 1
  ref = P_element
FEATURE [App::DocumentObjectGroupPython] O_element125  label="O_element : 078"  # scripted group (container) (typed FeaturePython)
  n = 3
  ref = O_element
FEATURE [App::DocumentObjectGroupPython] G4_DNA_MONOPHOSPHATE  # scripted group (container) (typed FeaturePython)
  Dunit = g/cm3
  Dvalue = 1
  Group = -> [P_element014,O_element125]
  conduct = 2
  density = 1
  expand = 3
  formula = G4_DNA_MONOPHOSPHATE
  name = G4_DNA_MONOPHOSPHATE
  specific = 4
FEATURE [App::DocumentObjectGroupPython] H_element134  label="H_element : 081"  # scripted group (container) (typed FeaturePython)
  n = 10
  ref = H_element
FEATURE [App::DocumentObjectGroupPython] C_element144  label="C_element : 089"  # scripted group (container) (typed FeaturePython)
  n = 10
  ref = C_element
FEATURE [App::DocumentObjectGroupPython] N_element064  label="N_element : 036"  # scripted group (container) (typed FeaturePython)
  n = 5
  ref = N_element
FEATURE [App::DocumentObjectGroupPython] O_element126  label="O_element : 079"  # scripted group (container) (typed FeaturePython)
  n = 7
  ref = O_element
FEATURE [App::DocumentObjectGroupPython] P_element015  label="P_element : 004"  # scripted group (container) (typed FeaturePython)
  n = 1
  ref = P_element
FEATURE [App::DocumentObjectGroupPython] G4_DNA_A  # scripted group (container) (typed FeaturePython)
  Dunit = g/cm3
  Dvalue = 1
  Group = -> [H_element134,C_element144,N_element064,O_element126,P_element015]
  conduct = 2
  density = 1
  expand = 3
  formula = G4_DNA_A
  name = G4_DNA_A
  specific = 4
FEATURE [App::DocumentObjectGroupPython] H_element135  label="H_element : 082"  # scripted group (container) (typed FeaturePython)
  n = 10
  ref = H_element
FEATURE [App::DocumentObjectGroupPython] C_element145  label="C_element : 090"  # scripted group (container) (typed FeaturePython)
  n = 10
  ref = C_element
FEATURE [App::DocumentObjectGroupPython] N_element065  label="N_element : 037"  # scripted group (container) (typed FeaturePython)
  n = 5
  ref = N_element
FEATURE [App::DocumentObjectGroupPython] O_element127  label="O_element : 8"  # scripted group (container) (typed FeaturePython)
  n = 8
  ref = O_element
FEATURE [App::DocumentObjectGroupPython] P_element016  label="P_element : 005"  # scripted group (container) (typed FeaturePython)
  n = 1
  ref = P_element
FEATURE [App::DocumentObjectGroupPython] G4_DNA_G  # scripted group (container) (typed FeaturePython)
  Dunit = g/cm3
  Dvalue = 1
  Group = -> [H_element135,C_element145,N_element065,O_element127,P_element016]
  conduct = 2
  density = 1
  expand = 3
  formula = G4_DNA_G
  name = G4_DNA_G
  specific = 4
FEATURE [App::DocumentObjectGroupPython] H_element136  label="H_element : 083"  # scripted group (container) (typed FeaturePython)
  n = 10
  ref = H_element
FEATURE [App::DocumentObjectGroupPython] C_element146  label="C_element : 091"  # scripted group (container) (typed FeaturePython)
  n = 9
  ref = C_element
FEATURE [App::DocumentObjectGroupPython] N_element066  label="N_element : 038"  # scripted group (container) (typed FeaturePython)
  n = 3
  ref = N_element
FEATURE [App::DocumentObjectGroupPython] O_element128  label="O_element : 080"  # scripted group (container) (typed FeaturePython)
  n = 8
  ref = O_element
FEATURE [App::DocumentObjectGroupPython] P_element017  label="P_element : 006"  # scripted group (container) (typed FeaturePython)
  n = 1
  ref = P_element
FEATURE [App::DocumentObjectGroupPython] G4_DNA_C  # scripted group (container) (typed FeaturePython)
  Dunit = g/cm3
  Dvalue = 1
  Group = -> [H_element136,C_element146,N_element066,O_element128,P_element017]
  conduct = 2
  density = 1
  expand = 3
  formula = G4_DNA_C
  name = G4_DNA_C
  specific = 4
FEATURE [App::DocumentObjectGroupPython] H_element137  label="H_element : 084"  # scripted group (container) (typed FeaturePython)
  n = 9
  ref = H_element
FEATURE [App::DocumentObjectGroupPython] C_element147  label="C_element : 092"  # scripted group (container) (typed FeaturePython)
  n = 9
  ref = C_element
FEATURE [App::DocumentObjectGroupPython] N_element067  label="N_element : 039"  # scripted group (container) (typed FeaturePython)
  n = 2
  ref = N_element
FEATURE [App::DocumentObjectGroupPython] O_element129  label="O_element : 9"  # scripted group (container) (typed FeaturePython)
  n = 9
  ref = O_element
FEATURE [App::DocumentObjectGroupPython] P_element018  label="P_element : 007"  # scripted group (container) (typed FeaturePython)
  n = 1
  ref = P_element
FEATURE [App::DocumentObjectGroupPython] G4_DNA_U  # scripted group (container) (typed FeaturePython)
  Dunit = g/cm3
  Dvalue = 1
  Group = -> [H_element137,C_element147,N_element067,O_element129,P_element018]
  conduct = 2
  density = 1
  expand = 3
  formula = G4_DNA_U
  name = G4_DNA_U
  specific = 4
FEATURE [App::DocumentObjectGroupPython] H_element138  label="H_element : 085"  # scripted group (container) (typed FeaturePython)
  n = 11
  ref = H_element
FEATURE [App::DocumentObjectGroupPython] C_element148  label="C_element : 093"  # scripted group (container) (typed FeaturePython)
  n = 10
  ref = C_element
FEATURE [App::DocumentObjectGroupPython] N_element068  label="N_element : 040"  # scripted group (container) (typed FeaturePython)
  n = 2
  ref = N_element
FEATURE [App::DocumentObjectGroupPython] O_element130  label="O_element : 081"  # scripted group (container) (typed FeaturePython)
  n = 9
  ref = O_element
FEATURE [App::DocumentObjectGroupPython] P_element019  label="P_element : 008"  # scripted group (container) (typed FeaturePython)
  n = 1
  ref = P_element
FEATURE [App::DocumentObjectGroupPython] G4_DNA_MU  # scripted group (container) (typed FeaturePython)
  Dunit = g/cm3
  Dvalue = 1
  Group = -> [H_element138,C_element148,N_element068,O_element130,P_element019]
  conduct = 2
  density = 1
  expand = 3
  formula = G4_DNA_MU
  name = G4_DNA_MU
  specific = 4
FEATURE [App::DocumentObjectGroupPython] BioChemical  # scripted group (container) (typed FeaturePython)
  Group = -> [G4_CYTOSINE,G4_THYMINE,G4_URACIL,G4_DNA_ADENINE,G4_DNA_GUANINE,G4_DNA_CYTOSINE,G4_DNA_THYMINE,G4_DNA_URACIL,G4_DNA_ADENOSINE,G4_DNA_GUANOSINE,G4_DNA_CYTIDINE,G4_DNA_URIDINE,G4_DNA_METHYLURIDINE,G4_DNA_MONOPHOSPHATE,G4_DNA_A,G4_DNA_G,G4_DNA_C,G4_DNA_U,G4_DNA_MU]
FEATURE [App::DocumentObjectGroupPython] G4Materials  # scripted group (container) (typed FeaturePython)
  Group = -> [NIST,Element,HEP,Space,BioChemical]
  version = 1
FEATURE [App::DocumentObjectGroupPython] Geant4  # scripted group (container) (typed FeaturePython)
  Group = -> [G4Isotopes,G4Elements,G4Materials]
FEATURE [App::DocumentObjectGroupPython] Materials  # scripted group (container) (typed FeaturePython)
  Group = -> [Geant4]
FEATURE [Part::FeaturePython] GDMLBox_WorldBox  # WARN: FeaturePython — macro-defined, semantics opaque (R4)
  lunit = 2
  material = 7
  x = 65
  y = 64.21
  z = 117
FEATURE [Part::Helix] Helix
  Angle = 0
  AttacherType = Attacher::AttachEngine3D
  Height = 40
  Length = 337.482
  LocalCoord = 0
  Pitch = 15
  Radius = 20
  SegmentLength = 0
  Style = 1
FEATURE [Part::FeaturePython] GDMLBox_Box  # WARN: FeaturePython — macro-defined, semantics opaque (R4)
  lunit = 2
  material = 0
  x = 10
  y = 10
  z = 10
FEATURE [Part::Cone] Cone001
  Angle = 360
  AttacherType = Attacher::AttachEngine3D
  Height = 4
  Radius1 = 0
  Radius2 = 2
FEATURE [App::Part] Part001  label="LV_Cone"
  Group = -> [Cone001]
  Origin = -> Origin003
  Placement = pos=(0,0,0.5) rot=(0,0,1;0rad)
FEATURE [Part::FeaturePython] GDMLSphere  # WARN: FeaturePython — macro-defined, semantics opaque (R4)
  aunit = 1
  deltaphi = 360
  deltatheta = 180
  lunit = 2
  material = 0
  rmax = 2
  rmin = 0
  startphi = 0
  starttheta = 0
FEATURE [App::Part] LV_Sphere
  Group = -> [GDMLSphere]
  Origin = -> Origin004
  Placement = pos=(0,0,-2) rot=(0,0,1;0rad)
  SkinSurface = 0
FEATURE [App::Part] LV_Box  label="Container"
  Group = -> [GDMLBox_Box,Part001,LV_Sphere]
  Origin = -> Origin002
FEATURE [Part::FeaturePython] PathArray  # WARN: FeaturePython — macro-defined, semantics opaque (R4)
  Align = false
  AlignMode = 0
  Base = -> LV_Box
  Count = 10
  EndOffset = 0
  ExtraTranslation = (0,0,0)
  ForceVertical = false
  Fuse = false
  PathObject = -> Helix
  StartOffset = 0
  TangentVector = (1,0,0)
  VerticalVector = (0,0,1)
FEATURE [App::Part] Part
  Group = -> [PathArray]
  Origin = -> Origin001
FEATURE [App::Part] worldVOL
  Group = -> [GDMLBox_WorldBox,Part]
  Origin = -> Origin
